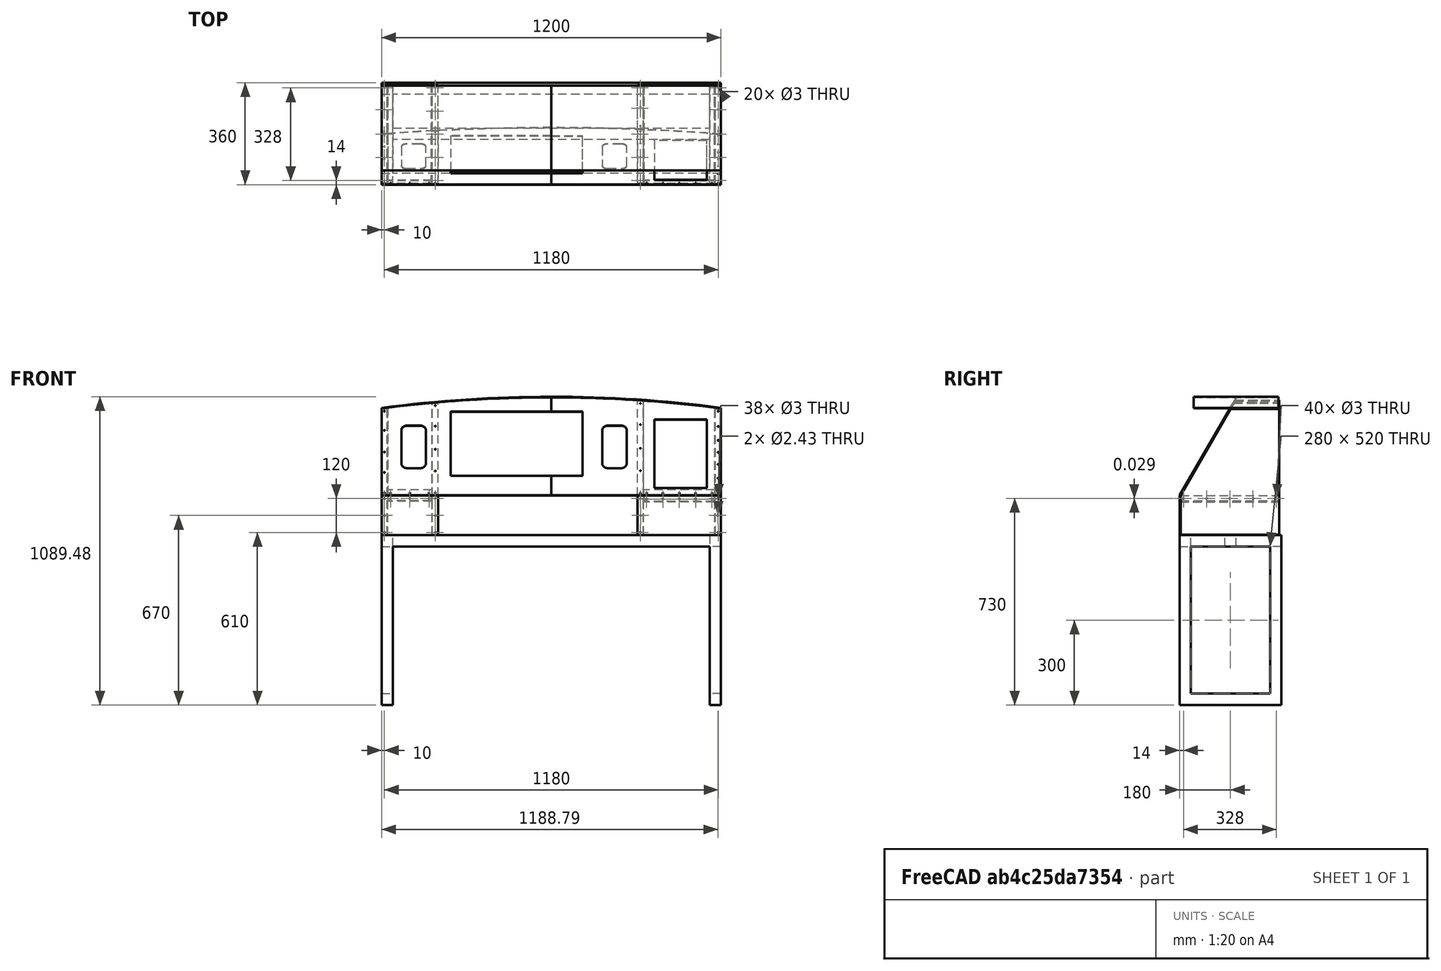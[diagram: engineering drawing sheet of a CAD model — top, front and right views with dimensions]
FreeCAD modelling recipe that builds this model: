
FCSTD DOCUMENT  (FreeCAD 1.0R39109 (Git))
Label: RecubrimientoSuperior
License: All rights reserved
LicenseURL: https://en.wikipedia.org/wiki/All_rights_reserved
objects: Sketcher::SketchObject×66, PartDesign::Pocket×43, PartDesign::Pad×23, PartDesign::SubShapeBinder×21, PartDesign::Body×13, PartDesign::Plane×3, App::DocumentObjectGroup×3, App::Part×3, Part::Part2DObjectPython×1
note: 368 computed .brp shape members not serialized (recipe doc carries the construction recipe); baked Part::Feature solids carry a one-line shape summary decoded from their .brp

FEATURE [Sketcher::SketchObject] Sketch
  ArcFitTolerance = 1e-06
  AttachmentSupport = -> [YZ_Plane001]
  FullyConstrained = true
  MakeInternals = false
  MapMode = 5
  Placement = pos=(0,0,0) rot=(0.57735,0.57735,0.57735;2.0944rad)
  sketch-geometry (4):
    g0: LineSegment StartX=2 StartY=0 StartZ=0 EndX=2 EndY=140 EndZ=0
    g1: LineSegment StartX=0 StartY=140 StartZ=0 EndX=0 EndY=0 EndZ=0
    g2: LineSegment StartX=0 StartY=0 StartZ=0 EndX=2 EndY=0 EndZ=0
    g3: LineSegment StartX=0 StartY=140 StartZ=0 EndX=2 EndY=140 EndZ=0
  constraints (11):
    c: Vertical(g0)
    c: Vertical(g1)
    c: Distance(g0,g1) = 2
    c: Distance(g1,g1) = 140
    c: Coincident(g1,g2)
    c: Coincident(g1,g-1)
    c: Coincident(g0,g2)
    c: PointOnObject(g0,g-1)
    c: Coincident(g3,g1)
    c: Coincident(g3,g0)
    c: Horizontal(g3)
FEATURE [PartDesign::Pad] Pad
  Direction = (1,0,0)
  Length = 200
  Length2 = 10
  Placement = pos=(0,0,0) rot=(1,1,1;2.0944rad)
  Profile = -> Sketch
  ReferenceAxis = -> Sketch [N_Axis]
  Refine = true
  Suppressed = false
  Type = 0
FEATURE [Sketcher::SketchObject] Sketch005
  ArcFitTolerance = 1e-06
  AttachmentSupport = -> [YZ_Plane002]
  FullyConstrained = true
  MakeInternals = false
  MapMode = 5
  Placement = pos=(0,0,0) rot=(0.57735,0.57735,0.57735;2.0944rad)
  sketch-geometry (4):
    g0: LineSegment StartX=0 StartY=0 StartZ=0 EndX=0 EndY=140 EndZ=0
    g1: LineSegment StartX=0 StartY=0 StartZ=0 EndX=2 EndY=0 EndZ=0
    g2: LineSegment StartX=2 StartY=0 StartZ=0 EndX=2 EndY=140 EndZ=0
    g3: LineSegment StartX=0 StartY=140 StartZ=0 EndX=2 EndY=140 EndZ=0
  constraints (11):
    c: Distance(g0) = 140
    c: Coincident(g0,g-1)
    c: PointOnObject(g0,g-2)
    c: Distance(g1) = 2
    c: Coincident(g1,g0)
    c: Vertical(g2)
    c: Coincident(g3,g0)
    c: Coincident(g3,g2)
    c: Horizontal(g3)
    c: Coincident(g2,g1)
    c: Horizontal(g1)
FEATURE [PartDesign::Pad] Pad002
  Direction = (1,0,0)
  Length = 295
  Length2 = 10
  Placement = pos=(0,0,0) rot=(1,1,1;2.0944rad)
  Profile = -> Sketch005
  ReferenceAxis = -> Sketch005 [N_Axis]
  Refine = true
  Suppressed = false
  Type = 0
FEATURE [Sketcher::SketchObject] Sketch009
  ArcFitTolerance = 1e-06
  AttachmentSupport = -> [XZ_Plane003]
  FullyConstrained = false
  MakeInternals = false
  MapMode = 5
  Placement = pos=(0,0,0) rot=(1,0,0;1.5708rad)
  sketch-geometry (31):
    g0: LineSegment StartX=-300 StartY=-200 StartZ=0 EndX=300 EndY=-200 EndZ=0
    g1: LineSegment StartX=300 StartY=-200 StartZ=0 EndX=300 EndY=-120 EndZ=0
    g2: LineSegment StartX=-300 StartY=154.794 StartZ=0 EndX=-300 EndY=-200 EndZ=0
    g3: GeomPoint [constr] X=0 Y=0 Z=0
    g4: LineSegment StartX=-230 StartY=65.1308 StartZ=0 EndX=-230 EndY=-68.8692 EndZ=0
    g5: LineSegment StartX=-210 StartY=-88.8692 StartZ=0 EndX=-163 EndY=-88.8692 EndZ=0
    g6: LineSegment StartX=-143 StartY=-68.8692 StartZ=0 EndX=-143 EndY=65.1308 EndZ=0
    g7: LineSegment StartX=-163 StartY=85.1308 StartZ=0 EndX=-210 EndY=85.1308 EndZ=0
    g8: ArcOfCircle CenterX=-210 CenterY=65.1308 CenterZ=0 NormalX=0 NormalY=0 NormalZ=1 AngleXU=0 Radius=20 StartAngle=1.5708 EndAngle=3.14159
    g9: ArcOfCircle CenterX=-210 CenterY=-68.8692 CenterZ=0 NormalX=0 NormalY=0 NormalZ=1 AngleXU=0 Radius=20 StartAngle=3.14159 EndAngle=4.71239
    g10: ArcOfCircle CenterX=-163 CenterY=-68.8692 CenterZ=0 NormalX=0 NormalY=0 NormalZ=1 AngleXU=0 Radius=20 StartAngle=4.71239 EndAngle=6.28319
    g11: ArcOfCircle CenterX=-163 CenterY=65.1308 CenterZ=0 NormalX=0 NormalY=0 NormalZ=1 AngleXU=0 Radius=20 StartAngle=0 EndAngle=1.5708
    g12: GeomPoint [constr] X=-230 Y=85.1308 Z=0
    g13: GeomPoint [constr] X=-143 Y=-88.8692 Z=0
    g14: LineSegment [constr] StartX=-300 StartY=-120 StartZ=0 EndX=-55 EndY=-120 EndZ=0
    g15: LineSegment [constr] StartX=-55 StartY=-200 StartZ=0 EndX=-55 EndY=-120 EndZ=0
    g16: LineSegment StartX=-55 StartY=-120 StartZ=0 EndX=300 EndY=-120 EndZ=0
    g17: LineSegment StartX=300 StartY=142 StartZ=0 EndX=-55 EndY=142 EndZ=0
    g18: LineSegment StartX=-55 StartY=142 StartZ=0 EndX=-55 EndY=-120 EndZ=0
    g19: LineSegment [constr] StartX=-300 StartY=150 StartZ=0 EndX=-300 EndY=105.005 EndZ=0
    g20: LineSegment [constr] StartX=-300.037 StartY=80 StartZ=0 EndX=-234.617 EndY=80 EndZ=0
    g21: LineSegment [constr] StartX=-234.617 StartY=80 StartZ=0 EndX=-234.617 EndY=175 EndZ=0
    g22: LineSegment [constr] StartX=-234.617 StartY=175 StartZ=0 EndX=-300 EndY=150 EndZ=0
    g23: LineSegment StartX=300 StartY=142 StartZ=0 EndX=300 EndY=200 EndZ=0
    g24: LineSegment [constr] StartX=122.5 StartY=-120 StartZ=0 EndX=122.5 EndY=-200 EndZ=0
    g25: LineSegment [constr] StartX=-300 StartY=154.794 StartZ=0 EndX=900 EndY=154.794 EndZ=0
    g26: ArcOfCircle CenterX=299.932 CenterY=-3803.45 CenterZ=0 NormalX=0 NormalY=0 NormalZ=1 AngleXU=0 Radius=4003.45 StartAngle=1.57078 EndAngle=1.72122
    g27: LineSegment [constr] StartX=-230 StartY=65.1308 StartZ=0 EndX=-143 EndY=65.1308 EndZ=0
    g28: LineSegment [constr] StartX=-230 StartY=-68.8692 StartZ=0 EndX=-143 EndY=-68.8692 EndZ=0
    g29: LineSegment [constr] StartX=-186.5 StartY=-68.8692 StartZ=0 EndX=-186.5 EndY=126.261 EndZ=0
    g30: LineSegment [constr] StartX=-300 StartY=15.0643 StartZ=0 EndX=-230 EndY=15.0643 EndZ=0
  constraints (78):
    c: Coincident(g0,g1)
    c: Coincident(g2,g0)
    c: Horizontal(g0)
    c: Vertical(g1)
    c: Vertical(g2)
    c: Symmetric(g23,g0,g3)
    c: Distance(g1,g2) = 600
    c: Distance(g0,g19) = 350
    c: Coincident(g3,g-1)
    c: Tangent(g4,g8) = -1.5708
    c: Tangent(g4,g9) = -1.5708
    c: Tangent(g5,g9) = -1.5708
    c: Tangent(g5,g10) = -1.5708
    c: Tangent(g6,g10) = -1.5708
    c: Tangent(g6,g11) = -1.5708
    c: Tangent(g7,g11) = -1.5708
    c: Tangent(g7,g8) = -1.5708
    c: Vertical(g4)
    c: Vertical(g6)
    c: Horizontal(g5)
    c: Horizontal(g7)
    c: Equal(g8,g9)
    c: Equal(g9,g10)
    c: Equal(g10,g11)
    c: PointOnObject(g12,g4)
    c: PointOnObject(g12,g7)
    c: PointOnObject(g13,g5)
    c: PointOnObject(g13,g6)
    c: Radius(g9) = 20
    c: Distance(g14) = 245
    c: PointOnObject(g14,g2)
    c: Horizontal(g14)
    c: Distance(g15) = 80
    c: PointOnObject(g15,g0)
    c: Vertical(g15)
    c: Coincident(g14,g15)
    c: Coincident(g17,g18)
    c: Coincident(g18,g16)
    c: Horizontal(g16)
    c: Horizontal(g17)
    c: Vertical(g18)
    c: Distance(g16,g17) = 262
    c: Coincident(g16,g14)
    c: Coincident(g20,g21)
    c: Coincident(g21,g22)
    c: Coincident(g22,g19)
    c: Vertical(g19)
    c: Vertical(g21)
    c: Horizontal(g20)
    c: Distance(g19,g21) = 70
    c: Distance(g20,g22) = 70
    c: PointOnObject(g17,g23)
    c: Coincident(g1,g16)
    c: PointOnObject(g23,g17)
    c: Symmetric(g16,g16,g24)
    c: PointOnObject(g24,g0)
    c: Vertical(g24)
    c: Vertical(g23)
    c: Distance(g25) = 1200
    c: PointOnObject(g25,g19)
    c: Horizontal(g25)
    c: Coincident(g26,g25)
    c: Coincident(g2,g25)
    c: Coincident(g23,g26)
    c: DistanceY(g0,g23) = 400
    c: Coincident(g27,g4)
    c: Coincident(g27,g6)
    c: Coincident(g28,g4)
    c: Coincident(g28,g6)
    c: Symmetric(g28,g28,g29)
    c: Vertical(g29)
    c: Distance(g30) = 70
    c: PointOnObject(g30,g2)
    c: Horizontal(g30)
    c: DistanceY(g5,g7) = 174
    c: DistanceX(g4,g6) = 87
    c: DistanceX(g17,g17) = 355
    c: PointOnObject(g30,g4)
FEATURE [PartDesign::SubShapeBinder] Binder
  BindCopyOnChange = 0
  BindMode = 2
  ClaimChildren = false
  Context = -> Part [Body003.Binder.]
  Fuse = false
  MakeFace = true
  OffsetFill = false
  OffsetIntersection = false
  OffsetJoinType = 0
  OffsetOpenResult = false
  PartialLoad = false
  Refine = true
  Relative = true
  _Version = 2
FEATURE [PartDesign::Pad] Pad003
  Direction = (0,-1,2e-16)
  Length = 2
  Length2 = 10
  Placement = pos=(0,0,0) rot=(1,0,0;1.5708rad)
  Profile = -> Sketch009
  ReferenceAxis = -> Sketch009 [N_Axis]
  Refine = true
  Reversed = true
  Suppressed = false
  Type = 0
FEATURE [Sketcher::SketchObject] Sketch012
  ArcFitTolerance = 1e-06
  AttachmentSupport = -> [Binder]
  ExternalGeometry = -> [Binder]
  FullyConstrained = true
  MakeInternals = false
  MapMode = 5
  Placement = pos=(0,86.1695,-49.75) rot=(1,0,0;1.0472rad)
  sketch-geometry (24):
    g0: LineSegment StartX=300 StartY=-176 StartZ=0 EndX=900 EndY=-176 EndZ=0
    g1: LineSegment StartX=900 StartY=-176 StartZ=0 EndX=900 EndY=178.794 EndZ=0
    g2: LineSegment StartX=300 StartY=-96 StartZ=0 EndX=410 EndY=-96 EndZ=0
    g3: LineSegment StartX=410 StartY=-96 StartZ=0 EndX=410 EndY=166 EndZ=0
    g4: LineSegment StartX=300 StartY=166 StartZ=0 EndX=410 EndY=166 EndZ=0
    g5: LineSegment [constr] StartX=-300 StartY=178.794 StartZ=0 EndX=900 EndY=178.794 EndZ=0
    g6: ArcOfCircle CenterX=299.932 CenterY=-3779.45 CenterZ=0 NormalX=0 NormalY=0 NormalZ=1 AngleXU=0 Radius=4003.47 StartAngle=1.42034 EndAngle=1.57078
    g7: LineSegment StartX=300 StartY=-96 StartZ=0 EndX=300 EndY=-176 EndZ=0
    g8: LineSegment StartX=500 StartY=-64.8692 StartZ=0 EndX=547 EndY=-64.8692 EndZ=0
    g9: LineSegment StartX=567 StartY=-44.8692 StartZ=0 EndX=567 EndY=89.1308 EndZ=0
    g10: LineSegment StartX=547 StartY=109.131 StartZ=0 EndX=500 EndY=109.131 EndZ=0
    g11: LineSegment StartX=480 StartY=89.1308 StartZ=0 EndX=480 EndY=-44.8692 EndZ=0
    g12: ArcOfCircle CenterX=500 CenterY=-44.8692 CenterZ=0 NormalX=0 NormalY=0 NormalZ=1 AngleXU=0 Radius=20 StartAngle=3.14159 EndAngle=4.71239
    g13: ArcOfCircle CenterX=547 CenterY=-44.8692 CenterZ=0 NormalX=0 NormalY=0 NormalZ=1 AngleXU=0 Radius=20 StartAngle=4.71239 EndAngle=6.28319
    g14: ArcOfCircle CenterX=547 CenterY=89.1308 CenterZ=0 NormalX=0 NormalY=0 NormalZ=1 AngleXU=0 Radius=20 StartAngle=0 EndAngle=1.5708
    g15: ArcOfCircle CenterX=500 CenterY=89.1308 CenterZ=0 NormalX=0 NormalY=0 NormalZ=1 AngleXU=0 Radius=20 StartAngle=1.5708 EndAngle=3.14159
    g16: GeomPoint [constr] X=480 Y=-64.8692 Z=0
    g17: GeomPoint [constr] X=567 Y=109.131 Z=0
    g18: LineSegment [constr] StartX=-143 StartY=-44.8692 StartZ=0 EndX=480 EndY=-44.8692 EndZ=0
    g19: LineSegment StartX=665 StartY=-146 StartZ=0 EndX=850 EndY=-146 EndZ=0
    g20: LineSegment StartX=850 StartY=-146 StartZ=0 EndX=850 EndY=134 EndZ=0
    g21: LineSegment StartX=850 StartY=134 StartZ=0 EndX=665 EndY=134 EndZ=0
    g22: LineSegment StartX=665 StartY=134 StartZ=0 EndX=665 EndY=-146 EndZ=0
    g23: LineSegment StartX=300 StartY=224.02 StartZ=0 EndX=300 EndY=166 EndZ=0
  constraints (61):
    c: Coincident(g0,g-3)
    c: Horizontal(g0)
    c: Coincident(g1,g0)
    c: Vertical(g1)
    c: Coincident(g2,g-7)
    c: Horizontal(g2)
    c: Coincident(g3,g2)
    c: Vertical(g3)
    c: Coincident(g4,g-5)
    c: Horizontal(g4)
    c: Coincident(g3,g4)
    c: DistanceX(g0,g0) = 600
    c: Coincident(g5,g-6)
    c: Coincident(g5,g1)
    c: Horizontal(g5)
    c: Coincident(g6,g-6)
    c: Coincident(g6,g1)
    c: Coincident(g7,g2)
    c: Coincident(g7,g0)
    c: DistanceX(g4,g4) = 110
    c: Tangent(g8,g12) = -1.5708
    c: Tangent(g8,g13) = -1.5708
    c: Tangent(g9,g13) = -1.5708
    c: Tangent(g9,g14) = -1.5708
    c: Tangent(g10,g14) = -1.5708
    c: Tangent(g10,g15) = -1.5708
    c: Tangent(g11,g15) = -1.5708
    c: Tangent(g11,g12) = -1.5708
    c: Horizontal(g8)
    c: Horizontal(g10)
    c: Vertical(g9)
    c: Vertical(g11)
    c: Equal(g12,g13)
    c: Equal(g13,g14)
    c: Equal(g14,g15)
    c: PointOnObject(g16,g8)
    c: PointOnObject(g16,g11)
    c: PointOnObject(g17,g9)
    c: PointOnObject(g17,g10)
    c: Equal(g15,g-8)
    c: Equal(g-10,g10)
    c: Equal(g-9,g11)
    c: Coincident(g18,g-9)
    c: Coincident(g18,g11)
    c: Horizontal(g18)
    c: DistanceX(g3,g11) = 70
    c: Coincident(g19,g20)
    c: Coincident(g20,g21)
    c: Coincident(g21,g22)
    c: Coincident(g22,g19)
    c: Horizontal(g19)
    c: Horizontal(g21)
    c: Vertical(g20)
    c: Vertical(g22)
    c: DistanceY(g22,g22) = 280
    c: DistanceX(g21,g21) = 185
    c: DistanceY(g0,g19) = 30
    c: DistanceX(g20,g1) = 50
    c: Coincident(g23,g6)
    c: Coincident(g23,g4)
    c: Vertical(g23)
FEATURE [PartDesign::Pad] Pad004
  Direction = (0,-0.866025,0.5)
  Length = 2
  Length2 = 10
  Profile = -> Sketch012
  ReferenceAxis = -> Sketch012 [N_Axis]
  Refine = true
  Reversed = true
  Suppressed = false
  Type = 0
FEATURE [PartDesign::SubShapeBinder] Binder002
  BindCopyOnChange = 0
  BindMode = 2
  ClaimChildren = false
  Context = -> Part [Body005.Binder002.]
  Fuse = false
  MakeFace = true
  OffsetFill = false
  OffsetIntersection = false
  OffsetJoinType = 0
  OffsetOpenResult = false
  PartialLoad = false
  Refine = true
  Relative = true
  _Version = 2
FEATURE [PartDesign::Plane] DatumPlane001
  AttachmentSupport = -> [XZ_Plane006,Binder002]
  Length = 664.107
  MapMode = 53
  Placement = pos=(0,-71.8202,-1.59e-14) rot=(1,0,0;1.5708rad)
  ResizeMode = 0
  Width = 235.347
FEATURE [Sketcher::SketchObject] Sketch014
  ArcFitTolerance = 1e-06
  AttachmentSupport = -> [DatumPlane001]
  ExternalGeometry = -> [Binder002]
  FullyConstrained = false
  MakeInternals = false
  MapMode = 5
  Placement = pos=(0,-71.8202,-1.59e-14) rot=(1,0,0;1.5708rad)
  sketch-geometry (4):
    g0: ArcOfCircle CenterX=299.094 CenterY=-4459.19 CenterZ=0 NormalX=0 NormalY=0 NormalZ=1 AngleXU=0 Radius=4603.43 StartAngle=1.5706 EndAngle=1.70131
    g1: LineSegment StartX=300 StartY=144.24 StartZ=0 EndX=300 EndY=146.24 EndZ=0
    g2: LineSegment StartX=-300 StartY=105.09 StartZ=0 EndX=-300 EndY=107.09 EndZ=0
    g3: ArcOfCircle CenterX=299.093 CenterY=-4457.17 CenterZ=0 NormalX=0 NormalY=0 NormalZ=1 AngleXU=0 Radius=4603.41 StartAngle=1.5706 EndAngle=1.70131
  constraints (10):
    c: Coincident(g0,g-5)
    c: Coincident(g0,g-4)
    c: Distance(g1) = 2
    c: Coincident(g1,g0)
    c: Vertical(g1)
    c: Distance(g2) = 2
    c: Coincident(g3,g2)
    c: Vertical(g2)
    c: Coincident(g3,g1)
    c: Coincident(g2,g0)
FEATURE [PartDesign::Pad] Pad005
  Direction = (0,-1,2e-16)
  Length = 300
  Length2 = 10
  Midplane = true
  Placement = pos=(0,-71.8202,-1.59e-14) rot=(1,0,0;1.5708rad)
  Profile = -> Sketch014
  ReferenceAxis = -> Sketch014 [N_Axis]
  Refine = true
  Suppressed = false
  Type = 0
FEATURE [PartDesign::Plane] DatumPlane002  label="Plano de refencia "
  AttachmentSupport = -> [Pad005]
  Length = 216.57
  MapMode = 5
  Placement = pos=(300,-71.8202,-1.59e-14) rot=(0.707107,0,0.707107;3.14159rad)
  ResizeMode = 0
  Width = 345.331
FEATURE [PartDesign::Body] Body005  label="LaminaSprPt1"
  AllowCompound = false
  Group = -> [Binder002,DatumPlane001,Sketch014,Pad005,DatumPlane002]
  Origin = -> Origin006
  Placement = pos=(0,270,0) rot=(0,0,1;0rad)
  Tip = -> Pad005
FEATURE [PartDesign::Plane] CopyDatumPlane001
  Length = 1867.38
  Placement = pos=(0,198.18,0) rot=(1,0,0;1.5708rad)
  ResizeMode = 0
  Width = 292.292
FEATURE [PartDesign::SubShapeBinder] Binder003
  BindCopyOnChange = 0
  BindMode = 2
  ClaimChildren = false
  Context = -> Part [Body006.Binder003.]
  Fuse = false
  MakeFace = true
  OffsetFill = false
  OffsetIntersection = false
  OffsetJoinType = 0
  OffsetOpenResult = false
  PartialLoad = false
  Refine = true
  Relative = true
  _Version = 2
FEATURE [Sketcher::SketchObject] Sketch015
  ArcFitTolerance = 1e-06
  AttachmentSupport = -> [CopyDatumPlane001]
  ExternalGeometry = -> [Binder003]
  FullyConstrained = false
  MakeInternals = false
  MapMode = 5
  Placement = pos=(0,198.18,0) rot=(1,0,0;1.5708rad)
  sketch-geometry (4):
    g0: ArcOfCircle CenterX=-1712.36 CenterY=-4462.69 CenterZ=0 NormalX=0 NormalY=0 NormalZ=1 AngleXU=0 Radius=4346.96 StartAngle=1.43642 EndAngle=1.57485
    g1: LineSegment StartX=-1130 StartY=-154.91 StartZ=0 EndX=-1130 EndY=-152.91 EndZ=0
    g2: ArcOfCircle CenterX=-1712.37 CenterY=-4460.9 CenterZ=0 NormalX=0 NormalY=0 NormalZ=1 AngleXU=0 Radius=4347.18 StartAngle=1.43643 EndAngle=1.57485
    g3: LineSegment StartX=-1730 StartY=-113.76 StartZ=0 EndX=-1730 EndY=-115.76 EndZ=0
  constraints (10):
    c: Coincident(g0,g-5)
    c: Coincident(g0,g-4)
    c: Distance(g1) = 2
    c: Coincident(g1,g0)
    c: Vertical(g1)
    c: Coincident(g3,g2)
    c: Coincident(g3,g0)
    c: Vertical(g3)
    c: Coincident(g2,g1)
    c: DistanceY(g3,g3) = 2
FEATURE [PartDesign::Pad] Pad006
  Direction = (0,-1,2e-16)
  Length = 300
  Length2 = 10
  Midplane = true
  Placement = pos=(0,198.18,0) rot=(1,0,0;1.5708rad)
  Profile = -> Sketch015
  ReferenceAxis = -> Sketch015 [N_Axis]
  Refine = true
  Suppressed = false
  Type = 0
FEATURE [PartDesign::Body] Body006  label="LaminaSprPt2"
  AllowCompound = false
  Group = -> [CopyDatumPlane001,Sketch015,Binder003,Pad006]
  Origin = -> Origin007
  Placement = pos=(2030,0,260) rot=(0,0,1;0rad)
  Tip = -> Pad006
FEATURE [Sketcher::SketchObject] Sketch019
  ArcFitTolerance = 1e-06
  AttachmentSupport = -> [Pad002]
  ExternalGeometry = -> [Pad002]
  FullyConstrained = false
  MakeInternals = false
  MapMode = 5
  Placement = pos=(0,0,0) rot=(0.57735,0.57735,-0.57735;2.0944rad)
  sketch-geometry (26):
    g0: LineSegment [constr] StartX=-3.28e-14 StartY=295 StartZ=0 EndX=-10 EndY=295 EndZ=0
    g1: LineSegment [constr] StartX=-10 StartY=295 StartZ=0 EndX=-10 EndY=285 EndZ=0
    g2: LineSegment [constr] StartX=-10 StartY=285 StartZ=0 EndX=-3.2e-14 EndY=285 EndZ=0
    g3: LineSegment [constr] StartX=-3.28e-14 StartY=285 StartZ=0 EndX=-3.28e-14 EndY=295 EndZ=0
    g4: LineSegment [constr] StartX=-140 StartY=295 StartZ=0 EndX=-140 EndY=285 EndZ=0
    g5: LineSegment [constr] StartX=-140 StartY=285 StartZ=0 EndX=-130 EndY=285 EndZ=0
    g6: LineSegment [constr] StartX=-130 StartY=285 StartZ=0 EndX=-130 EndY=295 EndZ=0
    g7: LineSegment [constr] StartX=-130 StartY=295 StartZ=0 EndX=-140 EndY=295 EndZ=0
    g8: LineSegment [constr] StartX=-70 StartY=295 StartZ=0 EndX=-70 EndY=0 EndZ=0
    g9: LineSegment [constr] StartX=0 StartY=147.5 StartZ=0 EndX=-140 EndY=147.5 EndZ=0
    g10: Circle CenterX=-130 CenterY=285 CenterZ=0 NormalX=0 NormalY=0 NormalZ=1 AngleXU=0 Radius=1.5
    g11: Circle CenterX=-10 CenterY=285 CenterZ=0 NormalX=0 NormalY=0 NormalZ=1 AngleXU=0 Radius=1.5
    g12: LineSegment [constr] StartX=-10 StartY=285 StartZ=0 EndX=-130 EndY=285 EndZ=0
    g13: Circle CenterX=-70 CenterY=283.786 CenterZ=0 NormalX=0 NormalY=0 NormalZ=1 AngleXU=0 Radius=1.21447
    g14: LineSegment [constr] StartX=0 StartY=0 StartZ=0 EndX=0 EndY=10 EndZ=0
    g15: LineSegment [constr] StartX=0 StartY=10 StartZ=0 EndX=-10 EndY=10 EndZ=0
    g16: LineSegment [constr] StartX=-10 StartY=10 StartZ=0 EndX=-10 EndY=0 EndZ=0
    g17: LineSegment [constr] StartX=-10 StartY=0 StartZ=0 EndX=0 EndY=0 EndZ=0
    g18: LineSegment [constr] StartX=-140 StartY=0 StartZ=0 EndX=-130 EndY=0 EndZ=0
    g19: LineSegment [constr] StartX=-130 StartY=0 StartZ=0 EndX=-130 EndY=10 EndZ=0
    g20: LineSegment [constr] StartX=-130 StartY=10 StartZ=0 EndX=-140 EndY=10 EndZ=0
    g21: LineSegment [constr] StartX=-140 StartY=10 StartZ=0 EndX=-140 EndY=0 EndZ=0
    g22: LineSegment [constr] StartX=-130 StartY=9.85879 StartZ=0 EndX=-10 EndY=9.85879 EndZ=0
    g23: Circle CenterX=-10 CenterY=10 CenterZ=0 NormalX=0 NormalY=0 NormalZ=1 AngleXU=0 Radius=1.5
    g24: Circle CenterX=-70 CenterY=11.3588 CenterZ=0 NormalX=0 NormalY=0 NormalZ=1 AngleXU=0 Radius=1.5
    g25: Circle CenterX=-130 CenterY=10 CenterZ=0 NormalX=0 NormalY=0 NormalZ=1 AngleXU=0 Radius=1.5
  constraints (56):
    c: Coincident(g0,g1)
    c: Coincident(g1,g2)
    c: Coincident(g2,g3)
    c: Coincident(g3,g0)
    c: Horizontal(g0)
    c: Horizontal(g2)
    c: Vertical(g1)
    c: Vertical(g3)
    c: Distance(g1,g3) = 10
    c: Distance(g0,g2) = 10
    c: Coincident(g0,g-3)
    c: Coincident(g4,g5)
    c: Coincident(g5,g6)
    c: Coincident(g6,g7)
    c: Coincident(g7,g4)
    c: Vertical(g4)
    c: Vertical(g6)
    c: Horizontal(g5)
    c: Horizontal(g7)
    c: Distance(g4,g6) = 10
    c: Distance(g5,g7) = 10
    c: Coincident(g4,g-4)
    c: PointOnObject(g8,g-1)
    c: Vertical(g8)
    c: Symmetric(g-6,g-6,g9)
    c: Symmetric(g-7,g-7,g9)
    c: Coincident(g11,g1)
    c: Coincident(g12,g1)
    c: Coincident(g12,g10)
    c: Horizontal(g12)
    c: Tangent(g13,g12)
    c: Coincident(g14,g15)
    c: Coincident(g15,g16)
    c: Coincident(g16,g17)
    c: Coincident(g17,g14)
    c: Vertical(g14)
    c: Vertical(g16)
    c: Horizontal(g15)
    c: Horizontal(g17)
    c: Distance(g14,g16) = 10
    c: Distance(g15,g17) = 10
    c: Coincident(g14,g-1)
    c: Coincident(g18,g19)
    c: Coincident(g19,g20)
    c: Coincident(g20,g21)
    c: Coincident(g21,g18)
    c: Horizontal(g18)
    c: Horizontal(g20)
    c: Vertical(g19)
    c: Vertical(g21)
    c: Distance(g19,g21) = 10
    c: Distance(g18,g20) = 10
    c: Coincident(g18,g-7)
    c: Diameter(g24) = 3
    c: PointOnObject(g24,g8)
    c: Tangent(g24,g22)
FEATURE [PartDesign::Pocket] Pocket008
  BaseFeature = -> Pad002
  Direction = (0,1,0)
  Length = 5
  Length2 = 5
  Placement = pos=(0,0,0) rot=(1,1,1;2.0944rad)
  Profile = -> Sketch019
  ReferenceAxis = -> Sketch019 [N_Axis]
  Refine = true
  Suppressed = false
  Type = 0
FEATURE [PartDesign::SubShapeBinder] Binder004
  BindCopyOnChange = 0
  BindMode = 2
  ClaimChildren = false
  Context = -> Part [Body004.Binder004.]
  Fuse = false
  MakeFace = true
  OffsetFill = false
  OffsetIntersection = false
  OffsetJoinType = 0
  OffsetOpenResult = false
  PartialLoad = false
  Refine = true
  Relative = true
  _Version = 2
FEATURE [Sketcher::SketchObject] Sketch020
  ArcFitTolerance = 1e-06
  AttachmentSupport = -> [Binder004]
  ExternalGeometry = -> [Binder004]
  FullyConstrained = false
  MakeInternals = false
  MapMode = 5
  Placement = pos=(-9e-16,-4.1,0) rot=(0,0.707107,0.707107;3.14159rad)
  sketch-geometry (10):
    g0: LineSegment [constr] StartX=-1180 StartY=-343.2 StartZ=0 EndX=-1160 EndY=-343.2 EndZ=0
    g1: LineSegment StartX=-1160 StartY=-341.2 StartZ=0 EndX=-1160 EndY=106.007 EndZ=0
    g2: LineSegment StartX=-1160 StartY=-343.2 StartZ=0 EndX=-1158 EndY=-343.2 EndZ=0
    g3: LineSegment StartX=-1158 StartY=-343.2 StartZ=0 EndX=-1158 EndY=108.007 EndZ=0
    g4: LineSegment StartX=-1158 StartY=108.007 StartZ=0 EndX=-1180 EndY=105.09 EndZ=0
    g5: LineSegment StartX=-1180 StartY=105.09 StartZ=0 EndX=-1180 EndY=103.09 EndZ=0
    g6: LineSegment StartX=-1180 StartY=103.09 StartZ=0 EndX=-1160 EndY=106.007 EndZ=0
    g7: LineSegment StartX=-1160 StartY=-343.2 StartZ=0 EndX=-1180 EndY=-343.2 EndZ=0
    g8: LineSegment StartX=-1180 StartY=-343.2 StartZ=0 EndX=-1180 EndY=-341.2 EndZ=0
    g9: LineSegment StartX=-1180 StartY=-341.2 StartZ=0 EndX=-1160 EndY=-341.2 EndZ=0
  constraints (26):
    c: Distance(g0) = 20
    c: Coincident(g0,g-3)
    c: Horizontal(g0)
    c: Vertical(g1)
    c: Distance(g2) = 2
    c: Coincident(g2,g0)
    c: Horizontal(g2)
    c: Coincident(g3,g2)
    c: PointOnObject(g3,g-5)
    c: Vertical(g3)
    c: Coincident(g4,g3)
    c: Coincident(g4,g-5)
    c: Distance(g5) = 2
    c: Coincident(g5,g4)
    c: Vertical(g5)
    c: Coincident(g6,g5)
    c: Coincident(g1,g6)
    c: DistanceY(g1,g3) = 2
    c: Coincident(g7,g0)
    c: Coincident(g7,g0)
    c: Distance(g8) = 2
    c: Coincident(g8,g0)
    c: Vertical(g8)
    c: Coincident(g9,g8)
    c: Horizontal(g9)
    c: Coincident(g1,g9)
FEATURE [PartDesign::Pad] Pad007
  Direction = (0,1,-2e-16)
  Length = 350
  Length2 = 10
  Profile = -> Sketch020
  ReferenceAxis = -> Sketch020 [N_Axis]
  Refine = true
  Suppressed = false
  Type = 0
FEATURE [Sketcher::SketchObject] Sketch021
  ArcFitTolerance = 1e-06
  AttachmentSupport = -> [Pad007]
  ExternalGeometry = -> [Binder004,Pad007]
  FullyConstrained = false
  MakeInternals = false
  MapMode = 5
  Placement = pos=(1160,0,0) rot=(0.57735,0.57735,0.57735;2.0944rad)
  sketch-geometry (3):
    g0: LineSegment StartX=-4.1 StartY=-203.2 StartZ=0 EndX=175.575 EndY=108.007 EndZ=0
    g1: LineSegment StartX=-4.1 StartY=108.007 StartZ=0 EndX=-4.1 EndY=-203.2 EndZ=0
    g2: LineSegment StartX=-4.1 StartY=108.007 StartZ=0 EndX=175.575 EndY=108.007 EndZ=0
  constraints (6):
    c: Angle(g-1,g0) = 1.0472
    c: Coincident(g0,g-4)
    c: Coincident(g1,g-5)
    c: Coincident(g1,g0)
    c: Coincident(g2,g1)
    c: Coincident(g0,g2)
FEATURE [PartDesign::Pocket] Pocket009
  BaseFeature = -> Pad007
  Direction = (-1,0,0)
  Length = 5
  Length2 = 5
  Midplane = true
  Profile = -> Sketch021
  ReferenceAxis = -> Sketch021 [N_Axis]
  Refine = true
  Suppressed = false
  Type = 1
FEATURE [Sketcher::SketchObject] Sketch022
  ArcFitTolerance = 1e-06
  AttachmentSupport = -> [Pocket009]
  ExternalGeometry = -> [Pocket009]
  FullyConstrained = true
  MakeInternals = false
  MapMode = 5
  Placement = pos=(1160,0,0) rot=(0.57735,0.57735,0.57735;2.0944rad)
  sketch-geometry (7):
    g0: LineSegment StartX=-4.1 StartY=-341.2 StartZ=0 EndX=-2.1 EndY=-341.2 EndZ=0
    g1: LineSegment StartX=-4.1 StartY=-341.2 StartZ=0 EndX=-4.1 EndY=-203.2 EndZ=0
    g2: LineSegment StartX=-4.1 StartY=-203.2 StartZ=0 EndX=172.736 EndY=103.09 EndZ=0
    g3: LineSegment StartX=-2.1 StartY=-341.2 StartZ=0 EndX=-2.1 EndY=-203.2 EndZ=0
    g4: LineSegment [constr] StartX=-4.1 StartY=-203.2 StartZ=0 EndX=-2.1 EndY=-203.2 EndZ=0
    g5: LineSegment StartX=-2.1 StartY=-203.2 StartZ=0 EndX=174.736 EndY=103.09 EndZ=0
    g6: LineSegment StartX=172.736 StartY=103.09 StartZ=0 EndX=174.736 EndY=103.09 EndZ=0
  constraints (17):
    c: Distance(g0) = 2
    c: Coincident(g0,g-5)
    c: Horizontal(g0)
    c: Coincident(g1,g0)
    c: Coincident(g1,g-5)
    c: Coincident(g2,g1)
    c: Coincident(g2,g-3)
    c: Coincident(g3,g0)
    c: Vertical(g3)
    c: Coincident(g4,g1)
    c: Coincident(g4,g3)
    c: Horizontal(g4)
    c: PointOnObject(g5,g-3)
    c: Coincident(g6,g2)
    c: Coincident(g6,g5)
    c: DistanceX(g6,g6) = 2
    c: Coincident(g5,g3)
FEATURE [PartDesign::Pad] Pad008
  BaseFeature = -> Pocket009
  Direction = (1,0,0)
  Length = 20
  Length2 = 10
  Profile = -> Sketch022
  ReferenceAxis = -> Sketch022 [N_Axis]
  Refine = true
  Suppressed = false
  Type = 0
FEATURE [Sketcher::SketchObject] Sketch023
  ArcFitTolerance = 1e-06
  AttachmentSupport = -> [Binder004]
  ExternalGeometry = -> [Binder004]
  FullyConstrained = true
  MakeInternals = false
  MapMode = 5
  Placement = pos=(-9e-16,-4.1,0) rot=(0,0.707107,0.707107;3.14159rad)
  sketch-geometry (3):
    g0: Circle CenterX=-1170 CenterY=-333.2 CenterZ=0 NormalX=0 NormalY=0 NormalZ=1 AngleXU=0 Radius=1.5
    g1: Circle CenterX=-1168.79 CenterY=-273.2 CenterZ=0 NormalX=0 NormalY=0 NormalZ=1 AngleXU=0 Radius=1.21447
    g2: Circle CenterX=-1170 CenterY=-213.2 CenterZ=0 NormalX=0 NormalY=0 NormalZ=1 AngleXU=0 Radius=1.5
  constraints (6):
    c: Coincident(g0,g-5)
    c: Equal(g0,g-5)
    c: Coincident(g1,g-4)
    c: Equal(g1,g-4)
    c: Coincident(g2,g-3)
    c: Equal(g2,g-3)
FEATURE [PartDesign::Pocket] Pocket010
  BaseFeature = -> Pad008
  Direction = (0,-1,2e-16)
  Length = 3
  Length2 = 5
  Profile = -> Sketch023
  ReferenceAxis = -> Sketch023 [N_Axis]
  Refine = true
  Reversed = true
  Suppressed = false
  Type = 0
FEATURE [Sketcher::SketchObject] Sketch024
  ArcFitTolerance = 1e-06
  AttachmentSupport = -> [Pocket010]
  ExternalGeometry = -> [Pocket010]
  FullyConstrained = false
  MakeInternals = false
  MapMode = 5
  Placement = pos=(-3.912e-13,84.9131,-49.0246) rot=(1,0,0;1.0472rad)
  sketch-geometry (45):
    g0: LineSegment [constr] StartX=1170 StartY=-186.687 StartZ=0 EndX=1180 EndY=-186.687 EndZ=0
    g1: LineSegment [constr] StartX=1170 StartY=-186.687 StartZ=0 EndX=1160 EndY=-186.687 EndZ=0
    g2: LineSegment [constr] StartX=1160 StartY=-186.687 StartZ=0 EndX=1160 EndY=175.647 EndZ=0
    g3: LineSegment [constr] StartX=1170 StartY=-186.687 StartZ=0 EndX=1170 EndY=-178.026 EndZ=0
    g4: LineSegment [constr] StartX=1170 StartY=-178.026 StartZ=0 EndX=1170 EndY=173.112 EndZ=0
    g5: LineSegment [constr] StartX=1170 StartY=173.112 StartZ=0 EndX=1170 EndY=153.112 EndZ=0
    g6: LineSegment [constr] StartX=1170 StartY=-178.06 StartZ=0 EndX=1180 EndY=-178.06 EndZ=0
    g7: LineSegment [constr] StartX=1180 StartY=-178.06 StartZ=0 EndX=1180 EndY=-168.06 EndZ=0
    g8: LineSegment [constr] StartX=1180 StartY=-168.06 StartZ=0 EndX=1170 EndY=-168.06 EndZ=0
    g9: LineSegment [constr] StartX=1170 StartY=-168.06 StartZ=0 EndX=1170 EndY=-178.06 EndZ=0
    g10: Circle CenterX=1170 CenterY=-168.06 CenterZ=0 NormalX=0 NormalY=0 NormalZ=1 AngleXU=0 Radius=1.5
    g11: LineSegment [constr] StartX=1170 StartY=-2.45712 StartZ=0 EndX=1180 EndY=-2.45712 EndZ=0
    g12: LineSegment [constr] StartX=1180 StartY=-2.45712 StartZ=0 EndX=1180 EndY=7.54288 EndZ=0
    g13: LineSegment [constr] StartX=1180 StartY=7.54288 StartZ=0 EndX=1170 EndY=7.54288 EndZ=0
    g14: LineSegment [constr] StartX=1170 StartY=7.54288 StartZ=0 EndX=1170 EndY=-2.45712 EndZ=0
    g15: Circle CenterX=1170 CenterY=-2.45712 CenterZ=0 NormalX=0 NormalY=0 NormalZ=1 AngleXU=0 Radius=1.5
    g16: LineSegment [constr] StartX=1170 StartY=173.112 StartZ=0 EndX=1170 EndY=163.112 EndZ=0
    g17: LineSegment [constr] StartX=1170 StartY=163.112 StartZ=0 EndX=1180 EndY=163.112 EndZ=0
    g18: LineSegment [constr] StartX=1180 StartY=163.112 StartZ=0 EndX=1180 EndY=173.112 EndZ=0
    g19: LineSegment [constr] StartX=1180 StartY=173.112 StartZ=0 EndX=1170 EndY=173.112 EndZ=0
    g20: Circle CenterX=1170 CenterY=165.291 CenterZ=0 NormalX=0 NormalY=0 NormalZ=1 AngleXU=0 Radius=1.5
    g21: LineSegment [constr] StartX=1297.09 StartY=68.0791 StartZ=0 EndX=1297.09 EndY=-37.9114 EndZ=0
    g22: LineSegment [constr] StartX=1297.09 StartY=15.0839 StartZ=0 EndX=1329.21 EndY=15.0839 EndZ=0
    g23: LineSegment [constr] StartX=1297.09 StartY=41.8939 StartZ=0 EndX=1329.2 EndY=41.8939 EndZ=0
    g24: LineSegment [constr] StartX=1297.09 StartY=-11.7261 StartZ=0 EndX=1329.2 EndY=-11.7261 EndZ=0
    g25: LineSegment [constr] StartX=1170 StartY=113.145 StartZ=0 EndX=1170 EndY=103.145 EndZ=0
    g26: LineSegment [constr] StartX=1170 StartY=103.145 StartZ=0 EndX=1180 EndY=103.145 EndZ=0
    g27: LineSegment [constr] StartX=1180 StartY=103.145 StartZ=0 EndX=1180 EndY=113.145 EndZ=0
    g28: LineSegment [constr] StartX=1180 StartY=113.145 StartZ=0 EndX=1170 EndY=113.145 EndZ=0
    g29: LineSegment [constr] StartX=1170 StartY=-51.3242 StartZ=0 EndX=1170 EndY=-61.3242 EndZ=0
    g30: LineSegment [constr] StartX=1170 StartY=-61.3242 StartZ=0 EndX=1180 EndY=-61.3242 EndZ=0
    g31: LineSegment [constr] StartX=1180 StartY=-61.3242 StartZ=0 EndX=1180 EndY=-51.3242 EndZ=0
    g32: LineSegment [constr] StartX=1180 StartY=-51.3242 StartZ=0 EndX=1170 EndY=-51.3242 EndZ=0
    g33: LineSegment [constr] StartX=1170 StartY=-118.06 StartZ=0 EndX=1180 EndY=-118.06 EndZ=0
    g34: LineSegment [constr] StartX=1180 StartY=-118.06 StartZ=0 EndX=1180 EndY=-108.06 EndZ=0
    g35: LineSegment [constr] StartX=1180 StartY=-108.06 StartZ=0 EndX=1170 EndY=-108.06 EndZ=0
    g36: LineSegment [constr] StartX=1170 StartY=-108.06 StartZ=0 EndX=1170 EndY=-118.06 EndZ=0
    g37: LineSegment [constr] StartX=1170 StartY=56.41 StartZ=0 EndX=1170 EndY=46.41 EndZ=0
    g38: LineSegment [constr] StartX=1170 StartY=46.41 StartZ=0 EndX=1180 EndY=46.41 EndZ=0
    g39: LineSegment [constr] StartX=1180 StartY=46.41 StartZ=0 EndX=1180 EndY=56.41 EndZ=0
    g40: LineSegment [constr] StartX=1180 StartY=56.41 StartZ=0 EndX=1170 EndY=56.41 EndZ=0
    g41: Circle CenterX=1170 CenterY=-108.06 CenterZ=0 NormalX=0 NormalY=0 NormalZ=1 AngleXU=0 Radius=1.5
    g42: Circle CenterX=1170 CenterY=-51.4132 CenterZ=0 NormalX=0 NormalY=0 NormalZ=1 AngleXU=0 Radius=1.5
    g43: Circle CenterX=1170 CenterY=46.41 CenterZ=0 NormalX=0 NormalY=0 NormalZ=1 AngleXU=0 Radius=1.5
    g44: Circle CenterX=1170 CenterY=103.145 CenterZ=0 NormalX=0 NormalY=0 NormalZ=1 AngleXU=0 Radius=1.5
  constraints (120):
    c: Coincident(g0,g-3)
    c: PointOnObject(g0,g-6)
    c: Horizontal(g0)
    c: Distance(g1) = 10
    c: Coincident(g1,g0)
    c: Horizontal(g1)
    c: Coincident(g2,g1)
    c: PointOnObject(g2,g-5)
    c: Vertical(g2)
    c: Coincident(g3,g0)
    c: PointOnObject(g3,g-4)
    c: Vertical(g3)
    c: Coincident(g4,g3)
    c: Vertical(g4)
    c: Distance(g5) = 20
    c: Coincident(g5,g4)
    c: PointOnObject(g5,g4)
    c: Coincident(g6,g7)
    c: Coincident(g7,g8)
    c: Coincident(g8,g9)
    c: Coincident(g9,g6)
    c: Horizontal(g6)
    c: Horizontal(g8)
    c: Vertical(g7)
    c: Vertical(g9)
    c: Distance(g7,g9) = 10
    c: Distance(g6,g8) = 10
    c: PointOnObject(g6,g3)
    c: Diameter(g10) = 3
    c: Coincident(g10,g8)
    c: Coincident(g11,g12)
    c: Coincident(g12,g13)
    c: Coincident(g13,g14)
    c: Coincident(g14,g11)
    c: Horizontal(g11)
    c: Horizontal(g13)
    c: Vertical(g12)
    c: Vertical(g14)
    c: Distance(g12,g14) = 10
    c: Distance(g11,g13) = 10
    c: Symmetric(g4,g4,g11)
    c: Diameter(g15) = 3
    c: Symmetric(g4,g4,g15)
    c: Coincident(g16,g17)
    c: Coincident(g17,g18)
    c: Coincident(g18,g19)
    c: Coincident(g19,g16)
    c: Vertical(g16)
    c: Vertical(g18)
    c: Horizontal(g17)
    c: Horizontal(g19)
    c: Distance(g16,g18) = 10
    c: Distance(g17,g19) = 10
    c: Coincident(g16,g4)
    c: Diameter(g20) = 3
    c: PointOnObject(g20,g4)
    c: Vertical(g21)
    c: Symmetric(g21,g21,g22)
    c: Horizontal(g22)
    c: PointOnObject(g23,g21)
    c: Horizontal(g23)
    c: PointOnObject(g24,g21)
    c: Horizontal(g24)
    c: Symmetric(g23,g24,g22)
    c: DistanceY(g22,g23) = 26.81
    c: Coincident(g25,g26)
    c: Coincident(g26,g27)
    c: Coincident(g27,g28)
    c: Coincident(g28,g25)
    c: Vertical(g25)
    c: Vertical(g27)
    c: Horizontal(g26)
    c: Horizontal(g28)
    c: Distance(g25,g27) = 10
    c: Distance(g26,g28) = 10
    c: PointOnObject(g25,g4)
    c: Coincident(g29,g30)
    c: Coincident(g30,g31)
    c: Coincident(g31,g32)
    c: Coincident(g32,g29)
    c: Vertical(g29)
    c: Vertical(g31)
    c: Horizontal(g30)
    c: Horizontal(g32)
    c: Distance(g29,g31) = 10
    c: Distance(g30,g32) = 10
    c: PointOnObject(g29,g4)
    c: Coincident(g33,g34)
    c: Coincident(g34,g35)
    c: Coincident(g35,g36)
    c: Coincident(g36,g33)
    c: Horizontal(g33)
    c: Horizontal(g35)
    c: Vertical(g34)
    c: Vertical(g36)
    c: Distance(g34,g36) = 10
    c: Distance(g33,g35) = 10
    c: Coincident(g37,g38)
    c: Coincident(g38,g39)
    c: Coincident(g39,g40)
    c: Coincident(g40,g37)
    c: Vertical(g37)
    c: Vertical(g39)
    c: Horizontal(g38)
    c: Horizontal(g40)
    c: Distance(g37,g39) = 10
    c: Distance(g38,g40) = 10
    c: Block(g11)
    c: Symmetric(g37,g29,g11)
    c: Symmetric(g35,g25,g11)
    c: Block(g8)
    c: DistanceY(g7,g33) = 50
    c: Diameter(g41) = 3
    c: Coincident(g41,g35)
    c: Diameter(g42) = 3
    c: PointOnObject(g42,g4)
    c: Diameter(g43) = 3
    c: Coincident(g43,g37)
    c: Diameter(g44) = 3
    c: Coincident(g44,g25)
FEATURE [PartDesign::Pocket] Pocket011
  BaseFeature = -> Pocket010
  Direction = (-4e-15,0.866026,-0.5)
  Length = 5
  Length2 = 5
  Profile = -> Sketch024
  ReferenceAxis = -> Sketch024 [N_Axis]
  Refine = true
  Suppressed = false
  Type = 0
FEATURE [Sketcher::SketchObject] Sketch025
  ArcFitTolerance = 1e-06
  AttachmentSupport = -> [Pocket011]
  ExternalGeometry = -> [Pocket011]
  FullyConstrained = true
  MakeInternals = false
  MapMode = 5
  Placement = pos=(34.0789,5.7e-14,257.027) rot=(0,1,0;0.13182rad)
  sketch-geometry (17):
    g0: LineSegment [constr] StartX=1155.95 StartY=345.9 StartZ=0 EndX=1145.95 EndY=345.9 EndZ=0
    g1: LineSegment [constr] StartX=1145.95 StartY=345.9 StartZ=0 EndX=1145.95 EndY=335.9 EndZ=0
    g2: LineSegment [constr] StartX=1145.95 StartY=335.9 StartZ=0 EndX=1155.95 EndY=335.9 EndZ=0
    g3: LineSegment [constr] StartX=1155.95 StartY=335.9 StartZ=0 EndX=1155.95 EndY=345.9 EndZ=0
    g4: LineSegment [constr] StartX=1155.95 StartY=173.891 StartZ=0 EndX=1155.95 EndY=183.891 EndZ=0
    g5: LineSegment [constr] StartX=1155.95 StartY=183.891 StartZ=0 EndX=1145.95 EndY=183.891 EndZ=0
    g6: LineSegment [constr] StartX=1145.95 StartY=183.891 StartZ=0 EndX=1145.95 EndY=173.891 EndZ=0
    g7: LineSegment [constr] StartX=1145.95 StartY=173.891 StartZ=0 EndX=1155.95 EndY=173.891 EndZ=0
    g8: LineSegment [constr] StartX=1155.95 StartY=259.896 StartZ=0 EndX=1155.95 EndY=269.896 EndZ=0
    g9: LineSegment [constr] StartX=1155.95 StartY=269.896 StartZ=0 EndX=1145.95 EndY=269.896 EndZ=0
    g10: LineSegment [constr] StartX=1145.95 StartY=269.896 StartZ=0 EndX=1145.95 EndY=259.896 EndZ=0
    g11: LineSegment [constr] StartX=1145.95 StartY=259.896 StartZ=0 EndX=1155.95 EndY=259.896 EndZ=0
    g12: LineSegment [constr] StartX=1145.95 StartY=335.9 StartZ=0 EndX=1145.95 EndY=269.896 EndZ=0
    g13: LineSegment [constr] StartX=1145.95 StartY=259.896 StartZ=0 EndX=1145.95 EndY=183.891 EndZ=0
    g14: Circle CenterX=1145.95 CenterY=183.891 CenterZ=0 NormalX=0 NormalY=0 NormalZ=1 AngleXU=0 Radius=1.5
    g15: Circle CenterX=1145.95 CenterY=259.896 CenterZ=0 NormalX=0 NormalY=0 NormalZ=1 AngleXU=0 Radius=1.5
    g16: Circle CenterX=1145.95 CenterY=335.9 CenterZ=0 NormalX=0 NormalY=0 NormalZ=1 AngleXU=0 Radius=1.5
  constraints (43):
    c: Coincident(g0,g1)
    c: Coincident(g1,g2)
    c: Coincident(g2,g3)
    c: Coincident(g3,g0)
    c: Horizontal(g0)
    c: Horizontal(g2)
    c: Vertical(g1)
    c: Vertical(g3)
    c: Distance(g1,g3) = 10
    c: Distance(g0,g2) = 10
    c: Coincident(g0,g-4)
    c: Coincident(g4,g5)
    c: Coincident(g5,g6)
    c: Coincident(g6,g7)
    c: Coincident(g7,g4)
    c: Vertical(g4)
    c: Vertical(g6)
    c: Horizontal(g5)
    c: Horizontal(g7)
    c: Distance(g4,g6) = 10
    c: Distance(g5,g7) = 10
    c: Coincident(g4,g-3)
    c: Coincident(g8,g9)
    c: Coincident(g9,g10)
    c: Coincident(g10,g11)
    c: Coincident(g11,g8)
    c: Vertical(g8)
    c: Vertical(g10)
    c: Horizontal(g9)
    c: Horizontal(g11)
    c: Distance(g8,g10) = 10
    c: Distance(g9,g11) = 10
    c: Symmetric(g-3,g-3,g8)
    c: Coincident(g12,g1)
    c: Coincident(g12,g9)
    c: Coincident(g13,g10)
    c: Coincident(g13,g5)
    c: Diameter(g14) = 3
    c: Coincident(g14,g5)
    c: Diameter(g15) = 3
    c: Coincident(g15,g10)
    c: Diameter(g16) = 3
    c: Coincident(g16,g1)
FEATURE [PartDesign::Pocket] Pocket012
  BaseFeature = -> Pocket011
  Direction = (-0.131439,0,-0.991324)
  Length = 5
  Length2 = 5
  Profile = -> Sketch025
  ReferenceAxis = -> Sketch025 [N_Axis]
  Refine = true
  Suppressed = false
  Type = 0
FEATURE [Sketcher::SketchObject] Sketch026
  ArcFitTolerance = 1e-06
  AttachmentSupport = -> [Pocket012]
  ExternalGeometry = -> [Pocket012]
  FullyConstrained = false
  MakeInternals = false
  MapMode = 5
  Placement = pos=(0,-7.51e-14,-341.2) rot=(0,0,1;0rad)
  sketch-geometry (27):
    g0: LineSegment [constr] StartX=1180 StartY=345.9 StartZ=0 EndX=1170 EndY=345.9 EndZ=0
    g1: LineSegment [constr] StartX=1170 StartY=345.9 StartZ=0 EndX=1170 EndY=335.9 EndZ=0
    g2: LineSegment [constr] StartX=1170 StartY=335.9 StartZ=0 EndX=1180 EndY=335.9 EndZ=0
    g3: LineSegment [constr] StartX=1180 StartY=335.9 StartZ=0 EndX=1180 EndY=345.9 EndZ=0
    g4: LineSegment [constr] StartX=1180 StartY=-2.1 StartZ=0 EndX=1180 EndY=7.9 EndZ=0
    g5: LineSegment [constr] StartX=1180 StartY=7.9 StartZ=0 EndX=1170 EndY=7.9 EndZ=0
    g6: LineSegment [constr] StartX=1170 StartY=7.9 StartZ=0 EndX=1170 EndY=-2.1 EndZ=0
    g7: LineSegment [constr] StartX=1170 StartY=-2.1 StartZ=0 EndX=1180 EndY=-2.1 EndZ=0
    g8: LineSegment [constr] StartX=1180 StartY=171.9 StartZ=0 EndX=1180 EndY=181.9 EndZ=0
    g9: LineSegment [constr] StartX=1180 StartY=181.9 StartZ=0 EndX=1170 EndY=181.9 EndZ=0
    g10: LineSegment [constr] StartX=1170 StartY=181.9 StartZ=0 EndX=1170 EndY=171.9 EndZ=0
    g11: LineSegment [constr] StartX=1170 StartY=171.9 StartZ=0 EndX=1180 EndY=171.9 EndZ=0
    g12: LineSegment [constr] StartX=1170 StartY=181.9 StartZ=0 EndX=1170 EndY=335.9 EndZ=0
    g13: LineSegment [constr] StartX=1170 StartY=258.9 StartZ=0 EndX=1180 EndY=258.9 EndZ=0
    g14: LineSegment [constr] StartX=1180 StartY=258.9 StartZ=0 EndX=1180 EndY=268.9 EndZ=0
    g15: LineSegment [constr] StartX=1180 StartY=268.9 StartZ=0 EndX=1170 EndY=268.9 EndZ=0
    g16: LineSegment [constr] StartX=1170 StartY=268.9 StartZ=0 EndX=1170 EndY=258.9 EndZ=0
    g17: LineSegment [constr] StartX=1170 StartY=171.9 StartZ=0 EndX=1170 EndY=7.9 EndZ=0
    g18: LineSegment [constr] StartX=1170 StartY=89.9 StartZ=0 EndX=1180 EndY=89.9 EndZ=0
    g19: LineSegment [constr] StartX=1180 StartY=89.9 StartZ=0 EndX=1180 EndY=99.9 EndZ=0
    g20: LineSegment [constr] StartX=1180 StartY=99.9 StartZ=0 EndX=1170 EndY=99.9 EndZ=0
    g21: LineSegment [constr] StartX=1170 StartY=99.9 StartZ=0 EndX=1170 EndY=89.9 EndZ=0
    g22: Circle CenterX=1170 CenterY=335.9 CenterZ=0 NormalX=0 NormalY=0 NormalZ=1 AngleXU=0 Radius=1.5
    g23: Circle CenterX=1170 CenterY=258.9 CenterZ=0 NormalX=0 NormalY=0 NormalZ=1 AngleXU=0 Radius=1.5
    g24: Circle CenterX=1170 CenterY=171.9 CenterZ=0 NormalX=0 NormalY=0 NormalZ=1 AngleXU=0 Radius=1.5
    g25: Circle CenterX=1170 CenterY=89.9 CenterZ=0 NormalX=0 NormalY=0 NormalZ=1 AngleXU=0 Radius=1.5
    g26: Circle CenterX=1170 CenterY=7.9 CenterZ=0 NormalX=0 NormalY=0 NormalZ=1 AngleXU=0 Radius=1.5
  constraints (59):
    c: Coincident(g0,g1)
    c: Coincident(g1,g2)
    c: Coincident(g2,g3)
    c: Coincident(g3,g0)
    c: Horizontal(g0)
    c: Horizontal(g2)
    c: Vertical(g1)
    c: Vertical(g3)
    c: Distance(g1,g3) = 10
    c: Distance(g0,g2) = 10
    c: Coincident(g0,g-3)
    c: Coincident(g4,g5)
    c: Coincident(g5,g6)
    c: Coincident(g6,g7)
    c: Coincident(g7,g4)
    c: Vertical(g4)
    c: Vertical(g6)
    c: Horizontal(g5)
    c: Horizontal(g7)
    c: Distance(g4,g6) = 10
    c: Distance(g5,g7) = 10
    c: Coincident(g4,g-3)
    c: Coincident(g8,g9)
    c: Coincident(g9,g10)
    c: Coincident(g10,g11)
    c: Coincident(g11,g8)
    c: Vertical(g8)
    c: Vertical(g10)
    c: Horizontal(g9)
    c: Horizontal(g11)
    c: Distance(g8,g10) = 10
    c: Distance(g9,g11) = 10
    c: Symmetric(g-3,g-3,g8)
    c: Coincident(g12,g9)
    c: Coincident(g12,g1)
    c: Coincident(g13,g14)
    c: Coincident(g14,g15)
    c: Coincident(g15,g16)
    c: Coincident(g16,g13)
    c: Horizontal(g13)
    c: Horizontal(g15)
    c: Vertical(g14)
    c: Vertical(g16)
    c: Distance(g13,g15) = 10
    c: Symmetric(g12,g12,g13)
    c: PointOnObject(g14,g-3)
    c: Coincident(g17,g10)
    c: Coincident(g17,g5)
    c: Coincident(g18,g19)
    c: Coincident(g19,g20)
    c: Coincident(g20,g21)
    c: Coincident(g21,g18)
    c: Horizontal(g18)
    c: Horizontal(g20)
    c: Vertical(g19)
    c: Vertical(g21)
    c: Distance(g18,g20) = 10
    c: Symmetric(g17,g17,g18)
    c: PointOnObject(g19,g-3)
FEATURE [PartDesign::Pocket] Pocket013
  BaseFeature = -> Pocket012
  Direction = (0,0,-1)
  Length = 5
  Length2 = 5
  Profile = -> Sketch026
  ReferenceAxis = -> Sketch026 [N_Axis]
  Refine = true
  Suppressed = false
  Type = 0
FEATURE [PartDesign::SubShapeBinder] Binder005
  BindCopyOnChange = 0
  BindMode = 2
  ClaimChildren = false
  Context = -> Part [Body003.Binder005.]
  Fuse = false
  MakeFace = true
  OffsetFill = false
  OffsetIntersection = false
  OffsetJoinType = 0
  OffsetOpenResult = false
  PartialLoad = false
  Refine = true
  Relative = true
  _Version = 2
FEATURE [Sketcher::SketchObject] Sketch027
  ArcFitTolerance = 1e-06
  AttachmentSupport = -> [Pad004]
  ExternalGeometry = -> [Binder005]
  FullyConstrained = false
  MakeInternals = false
  MapMode = 5
  Placement = pos=(0,87.9016,-50.75) rot=(0,0.866025,0.5;3.14159rad)
  sketch-geometry (7):
    g0: Circle CenterX=-890 CenterY=167.291 CenterZ=0 NormalX=0 NormalY=0 NormalZ=1 AngleXU=0 Radius=1.5
    g1: Circle CenterX=-890 CenterY=105.145 CenterZ=0 NormalX=0 NormalY=0 NormalZ=1 AngleXU=0 Radius=1.5
    g2: Circle CenterX=-890 CenterY=48.4101 CenterZ=0 NormalX=0 NormalY=0 NormalZ=1 AngleXU=0 Radius=1.5
    g3: Circle CenterX=-890 CenterY=-0.457073 CenterZ=0 NormalX=0 NormalY=0 NormalZ=1 AngleXU=0 Radius=1.5
    g4: Circle CenterX=-890 CenterY=-49.4131 CenterZ=0 NormalX=0 NormalY=0 NormalZ=1 AngleXU=0 Radius=1.5
    g5: Circle CenterX=-890 CenterY=-106.06 CenterZ=0 NormalX=0 NormalY=0 NormalZ=1 AngleXU=0 Radius=1.5
    g6: Circle CenterX=-890 CenterY=-166.06 CenterZ=0 NormalX=0 NormalY=0 NormalZ=1 AngleXU=0 Radius=1.5
  constraints (7):
    c: Coincident(g0,g-3)
    c: Coincident(g1,g-4)
    c: Coincident(g2,g-5)
    c: Coincident(g3,g-6)
    c: Coincident(g4,g-7)
    c: Coincident(g5,g-8)
    c: Coincident(g6,g-9)
FEATURE [PartDesign::Pocket] Pocket014
  BaseFeature = -> Pad004
  Direction = (0,-0.866025,0.5)
  Length = 5
  Length2 = 5
  Profile = -> Sketch027
  ReferenceAxis = -> Sketch027 [N_Axis]
  Refine = true
  Suppressed = false
  Type = 0
FEATURE [PartDesign::SubShapeBinder] Binder006
  BindCopyOnChange = 0
  BindMode = 2
  ClaimChildren = false
  Context = -> Part [Body007.Binder006.]
  Fuse = false
  MakeFace = true
  OffsetFill = false
  OffsetIntersection = false
  OffsetJoinType = 0
  OffsetOpenResult = false
  PartialLoad = false
  Refine = true
  Relative = true
  _Version = 2
FEATURE [Sketcher::SketchObject] Sketch028
  ArcFitTolerance = 1e-06
  AttachmentSupport = -> [Binder006]
  ExternalGeometry = -> [Binder006]
  FullyConstrained = true
  MakeInternals = false
  MapMode = 5
  Placement = pos=(0,-0.1,0) rot=(0,0.707107,0.707107;3.14159rad)
  sketch-geometry (8):
    g0: LineSegment StartX=-627 StartY=-343.2 StartZ=0 EndX=-627 EndY=133.254 EndZ=0
    g1: LineSegment StartX=-625 StartY=-341.2 StartZ=0 EndX=-625 EndY=131.254 EndZ=0
    g2: LineSegment StartX=-627 StartY=133.254 StartZ=0 EndX=-605.052 EndY=134.764 EndZ=0
    g3: LineSegment StartX=-605.052 StartY=134.764 StartZ=0 EndX=-605.052 EndY=132.764 EndZ=0
    g4: LineSegment StartX=-605.052 StartY=132.764 StartZ=0 EndX=-625 EndY=131.254 EndZ=0
    g5: LineSegment StartX=-605 StartY=-343.2 StartZ=0 EndX=-627 EndY=-343.2 EndZ=0
    g6: LineSegment StartX=-605 StartY=-343.2 StartZ=0 EndX=-605 EndY=-341.2 EndZ=0
    g7: LineSegment StartX=-605 StartY=-341.2 StartZ=0 EndX=-625 EndY=-341.2 EndZ=0
  constraints (23):
    c: Vertical(g0)
    c: Vertical(g1)
    c: PointOnObject(g0,g-4)
    c: Distance(g2) = 22
    c: Coincident(g2,g0)
    c: PointOnObject(g2,g-4)
    c: Distance(g3) = 2
    c: Coincident(g3,g2)
    c: Vertical(g3)
    c: Coincident(g4,g3)
    c: Coincident(g1,g4)
    c: DistanceY(g1,g0) = 2
    c: Coincident(g5,g-3)
    c: Horizontal(g5)
    c: Distance(g6) = 2
    c: Coincident(g6,g5)
    c: Vertical(g6)
    c: Coincident(g7,g6)
    c: Horizontal(g7)
    c: Coincident(g7,g1)
    c: Coincident(g5,g0)
    c: DistanceX(g0,g1) = 2
    c: DistanceX(g7,g7) = 20
FEATURE [PartDesign::Pad] Pad009
  Direction = (0,1,-2e-16)
  Length = 350
  Length2 = 10
  Profile = -> Sketch028
  ReferenceAxis = -> Sketch028 [N_Axis]
  Refine = true
  Suppressed = false
  Type = 0
FEATURE [Sketcher::SketchObject] Sketch029
  ArcFitTolerance = 1e-06
  AttachmentSupport = -> [Pad009]
  ExternalGeometry = -> [Binder006,Pad009]
  FullyConstrained = true
  MakeInternals = false
  MapMode = 5
  Placement = pos=(627,0,0) rot=(0.57735,0.57735,0.57735;2.0944rad)
  sketch-geometry (3):
    g0: LineSegment StartX=-0.1 StartY=-203.2 StartZ=0 EndX=195.023 EndY=134.764 EndZ=0
    g1: LineSegment StartX=195.023 StartY=134.764 StartZ=0 EndX=-0.1 EndY=134.764 EndZ=0
    g2: LineSegment StartX=-0.1 StartY=134.764 StartZ=0 EndX=-0.1 EndY=-203.2 EndZ=0
  constraints (8):
    c: Angle(g-1,g0) = 1.0472
    c: Coincident(g0,g-3)
    c: PointOnObject(g0,g-4)
    c: Coincident(g1,g0)
    c: Horizontal(g1)
    c: Coincident(g2,g1)
    c: Coincident(g2,g0)
    c: Vertical(g2)
FEATURE [PartDesign::Pocket] Pocket015
  BaseFeature = -> Pad009
  Direction = (-1,0,0)
  Length = 5
  Length2 = 5
  Profile = -> Sketch029
  ReferenceAxis = -> Sketch029 [N_Axis]
  Refine = true
  Suppressed = false
  Type = 1
FEATURE [Sketcher::SketchObject] Sketch030
  ArcFitTolerance = 1e-06
  AttachmentSupport = -> [Pocket015]
  ExternalGeometry = -> [Pocket015]
  FullyConstrained = true
  MakeInternals = false
  MapMode = 5
  Placement = pos=(625,0,0) rot=(0.57735,-0.57735,-0.57735;2.0944rad)
  sketch-geometry (7):
    g0: LineSegment StartX=0.1 StartY=-341.2 StartZ=0 EndX=0.1 EndY=-203.2 EndZ=0
    g1: LineSegment StartX=0.1 StartY=-203.2 StartZ=0 EndX=-192.997 EndY=131.254 EndZ=0
    g2: LineSegment StartX=-192.997 StartY=131.254 StartZ=0 EndX=-194.997 EndY=131.254 EndZ=0
    g3: LineSegment StartX=-194.997 StartY=131.254 StartZ=0 EndX=-1.9 EndY=-203.2 EndZ=0
    g4: LineSegment StartX=0.1 StartY=-341.2 StartZ=0 EndX=-1.9 EndY=-341.2 EndZ=0
    g5: LineSegment StartX=-1.9 StartY=-341.2 StartZ=0 EndX=-1.9 EndY=-203.2 EndZ=0
    g6: LineSegment [constr] StartX=-1.9 StartY=-203.2 StartZ=0 EndX=0.1 EndY=-203.2 EndZ=0
  constraints (17):
    c: Coincident(g0,g-3)
    c: Coincident(g0,g-4)
    c: Coincident(g1,g0)
    c: Coincident(g1,g-4)
    c: Distance(g2) = 2
    c: Coincident(g2,g1)
    c: Horizontal(g2)
    c: Coincident(g3,g2)
    c: Distance(g4) = 2
    c: Coincident(g4,g0)
    c: Horizontal(g4)
    c: Coincident(g5,g4)
    c: Coincident(g5,g3)
    c: Vertical(g5)
    c: Coincident(g6,g3)
    c: Coincident(g6,g0)
    c: Horizontal(g6)
FEATURE [PartDesign::Pad] Pad010
  BaseFeature = -> Pocket015
  Direction = (-1,0,0)
  Length = 20
  Length2 = 10
  Profile = -> Sketch030
  ReferenceAxis = -> Sketch030 [N_Axis]
  Refine = true
  Suppressed = false
  Type = 0
FEATURE [Sketcher::SketchObject] Sketch031
  ArcFitTolerance = 1e-06
  AttachmentSupport = -> [Binder006]
  ExternalGeometry = -> [Binder006]
  FullyConstrained = true
  MakeInternals = false
  MapMode = 5
  Placement = pos=(0,-0.1,0) rot=(0,0.707107,0.707107;3.14159rad)
  sketch-geometry (3):
    g0: Circle CenterX=-615 CenterY=-213.2 CenterZ=0 NormalX=0 NormalY=0 NormalZ=1 AngleXU=0 Radius=1.5
    g1: Circle CenterX=-616.359 CenterY=-273.2 CenterZ=0 NormalX=0 NormalY=0 NormalZ=1 AngleXU=0 Radius=1.5
    g2: Circle CenterX=-615 CenterY=-333.2 CenterZ=0 NormalX=0 NormalY=0 NormalZ=1 AngleXU=0 Radius=1.5
  constraints (6):
    c: Coincident(g0,g-3)
    c: Equal(g0,g-3)
    c: Coincident(g1,g-4)
    c: Equal(g1,g-4)
    c: Coincident(g2,g-5)
    c: Equal(g2,g-5)
FEATURE [PartDesign::Pocket] Pocket016
  BaseFeature = -> Pad010
  Direction = (0,-1,2e-16)
  Length = 5
  Length2 = 5
  Profile = -> Sketch031
  ReferenceAxis = -> Sketch031 [N_Axis]
  Refine = true
  Reversed = true
  Suppressed = false
  Type = 0
FEATURE [Sketcher::SketchObject] Sketch032
  ArcFitTolerance = 1e-06
  AttachmentSupport = -> [Pocket016]
  ExternalGeometry = -> [Pocket016]
  FullyConstrained = false
  MakeInternals = false
  MapMode = 5
  Placement = pos=(1.797e-13,87.9131,-50.7566) rot=(1,0,0;1.0472rad)
  sketch-geometry (26):
    g0: LineSegment [constr] StartX=605 StartY=-176.026 StartZ=0 EndX=615 EndY=-176.026 EndZ=0
    g1: LineSegment [constr] StartX=615 StartY=-176.026 StartZ=0 EndX=615 EndY=-166.026 EndZ=0
    g2: LineSegment [constr] StartX=615 StartY=-166.026 StartZ=0 EndX=605 EndY=-166.026 EndZ=0
    g3: LineSegment [constr] StartX=605 StartY=-166.026 StartZ=0 EndX=605 EndY=-176.026 EndZ=0
    g4: LineSegment [constr] StartX=605 StartY=210.167 StartZ=0 EndX=605 EndY=200.167 EndZ=0
    g5: LineSegment [constr] StartX=605 StartY=200.167 StartZ=0 EndX=615 EndY=200.167 EndZ=0
    g6: LineSegment [constr] StartX=615 StartY=200.167 StartZ=0 EndX=615 EndY=210.167 EndZ=0
    g7: LineSegment [constr] StartX=615 StartY=210.167 StartZ=0 EndX=605 EndY=210.167 EndZ=0
    g8: LineSegment [constr] StartX=605 StartY=17.0704 StartZ=0 EndX=615 EndY=17.0704 EndZ=0
    g9: LineSegment [constr] StartX=615 StartY=17.0704 StartZ=0 EndX=615 EndY=27.0704 EndZ=0
    g10: LineSegment [constr] StartX=615 StartY=27.0704 StartZ=0 EndX=605 EndY=27.0704 EndZ=0
    g11: LineSegment [constr] StartX=605 StartY=27.0704 StartZ=0 EndX=605 EndY=17.0704 EndZ=0
    g12: LineSegment [constr] StartX=615 StartY=-74.478 StartZ=0 EndX=605 EndY=-74.478 EndZ=0
    g13: LineSegment [constr] StartX=615 StartY=113.619 StartZ=0 EndX=615 EndY=123.619 EndZ=0
    g14: LineSegment [constr] StartX=615 StartY=123.619 StartZ=0 EndX=605 EndY=123.619 EndZ=0
    g15: LineSegment [constr] StartX=605 StartY=123.619 StartZ=0 EndX=605 EndY=113.619 EndZ=0
    g16: LineSegment [constr] StartX=605 StartY=113.619 StartZ=0 EndX=615 EndY=113.619 EndZ=0
    g17: LineSegment [constr] StartX=615 StartY=113.619 StartZ=0 EndX=615 EndY=200.167 EndZ=0
    g18: LineSegment [constr] StartX=615 StartY=113.619 StartZ=0 EndX=615 EndY=17.0704 EndZ=0
    g19: LineSegment [constr] StartX=615 StartY=-166.026 StartZ=0 EndX=615 EndY=-74.478 EndZ=0
    g20: LineSegment [constr] StartX=615 StartY=17.0704 StartZ=0 EndX=615 EndY=-74.478 EndZ=0
    g21: Circle CenterX=615 CenterY=-166.026 CenterZ=0 NormalX=0 NormalY=0 NormalZ=1 AngleXU=0 Radius=1.5
    g22: Circle CenterX=615 CenterY=17.0704 CenterZ=0 NormalX=0 NormalY=0 NormalZ=1 AngleXU=0 Radius=1.5
    g23: Circle CenterX=615 CenterY=113.619 CenterZ=0 NormalX=0 NormalY=0 NormalZ=1 AngleXU=0 Radius=1.5
    g24: Circle CenterX=615 CenterY=200.167 CenterZ=0 NormalX=0 NormalY=0 NormalZ=1 AngleXU=0 Radius=1.5
    g25: Circle CenterX=615 CenterY=-74.478 CenterZ=0 NormalX=0 NormalY=0 NormalZ=1 AngleXU=0 Radius=1.5
FEATURE [PartDesign::Pocket] Pocket017
  BaseFeature = -> Pocket016
  Direction = (1.3e-15,0.866026,-0.5)
  Length = 5
  Length2 = 5
  Profile = -> Sketch032
  ReferenceAxis = -> Sketch032 [N_Axis]
  Refine = true
  Suppressed = false
  Type = 0
FEATURE [Sketcher::SketchObject] Sketch033
  ArcFitTolerance = 1e-06
  AttachmentSupport = -> [Pocket017]
  ExternalGeometry = -> [Pocket017]
  FullyConstrained = false
  MakeInternals = false
  MapMode = 5
  Placement = pos=(0,-7.51e-14,-341.2) rot=(0,0,1;0rad)
  sketch-geometry (28):
    g0: LineSegment [constr] StartX=615 StartY=349.9 StartZ=0 EndX=615 EndY=1.9 EndZ=0
    g1: LineSegment [constr] StartX=615 StartY=175.9 StartZ=0 EndX=605 EndY=175.9 EndZ=0
    g2: LineSegment [constr] StartX=605 StartY=175.9 StartZ=0 EndX=605 EndY=185.9 EndZ=0
    g3: LineSegment [constr] StartX=605 StartY=185.9 StartZ=0 EndX=615 EndY=185.9 EndZ=0
    g4: LineSegment [constr] StartX=615 StartY=185.9 StartZ=0 EndX=615 EndY=175.9 EndZ=0
    g5: LineSegment [constr] StartX=605 StartY=185.9 StartZ=0 EndX=605 EndY=349.9 EndZ=0
    g6: LineSegment [constr] StartX=605 StartY=267.9 StartZ=0 EndX=615 EndY=267.9 EndZ=0
    g7: LineSegment [constr] StartX=615 StartY=267.9 StartZ=0 EndX=615 EndY=277.9 EndZ=0
    g8: LineSegment [constr] StartX=615 StartY=277.9 StartZ=0 EndX=605 EndY=277.9 EndZ=0
    g9: LineSegment [constr] StartX=605 StartY=277.9 StartZ=0 EndX=605 EndY=267.9 EndZ=0
    g10: LineSegment [constr] StartX=605 StartY=349.9 StartZ=0 EndX=605 EndY=339.9 EndZ=0
    g11: LineSegment [constr] StartX=605 StartY=339.9 StartZ=0 EndX=615 EndY=339.9 EndZ=0
    g12: LineSegment [constr] StartX=615 StartY=339.9 StartZ=0 EndX=615 EndY=349.9 EndZ=0
    g13: LineSegment [constr] StartX=615 StartY=349.9 StartZ=0 EndX=605 EndY=349.9 EndZ=0
    g14: LineSegment [constr] StartX=615 StartY=1.9 StartZ=0 EndX=615 EndY=11.9 EndZ=0
    g15: LineSegment [constr] StartX=615 StartY=11.9 StartZ=0 EndX=605 EndY=11.9 EndZ=0
    g16: LineSegment [constr] StartX=605 StartY=11.9 StartZ=0 EndX=605 EndY=1.9 EndZ=0
    g17: LineSegment [constr] StartX=605 StartY=1.9 StartZ=0 EndX=615 EndY=1.9 EndZ=0
    g18: LineSegment [constr] StartX=605 StartY=175.9 StartZ=0 EndX=605 EndY=11.9 EndZ=0
    g19: LineSegment [constr] StartX=605 StartY=93.9 StartZ=0 EndX=615 EndY=93.9 EndZ=0
    g20: LineSegment [constr] StartX=615 StartY=93.9 StartZ=0 EndX=615 EndY=103.9 EndZ=0
    g21: LineSegment [constr] StartX=615 StartY=103.9 StartZ=0 EndX=605 EndY=103.9 EndZ=0
    g22: LineSegment [constr] StartX=605 StartY=103.9 StartZ=0 EndX=605 EndY=93.9 EndZ=0
    g23: Circle CenterX=615 CenterY=11.9 CenterZ=0 NormalX=0 NormalY=0 NormalZ=1 AngleXU=0 Radius=1.5
    g24: Circle CenterX=615 CenterY=93.9 CenterZ=0 NormalX=0 NormalY=0 NormalZ=1 AngleXU=0 Radius=1.5
    g25: Circle CenterX=615 CenterY=175.9 CenterZ=0 NormalX=0 NormalY=0 NormalZ=1 AngleXU=0 Radius=1.5
    g26: Circle CenterX=615 CenterY=267.9 CenterZ=0 NormalX=0 NormalY=0 NormalZ=1 AngleXU=0 Radius=1.5
    g27: Circle CenterX=615 CenterY=339.9 CenterZ=0 NormalX=0 NormalY=0 NormalZ=1 AngleXU=0 Radius=1.5
  constraints (59):
    c: Symmetric(g-4,g-4,g0)
    c: Symmetric(g-3,g-3,g0)
    c: Coincident(g1,g2)
    c: Coincident(g2,g3)
    c: Coincident(g3,g4)
    c: Coincident(g4,g1)
    c: Horizontal(g1)
    c: Horizontal(g3)
    c: Vertical(g2)
    c: Vertical(g4)
    c: Symmetric(g0,g0,g1)
    c: DistanceY(g2,g2) = 10
    c: DistanceX(g3,g3) = 10
    c: Coincident(g5,g2)
    c: Coincident(g5,g-4)
    c: Coincident(g6,g7)
    c: Coincident(g7,g8)
    c: Coincident(g8,g9)
    c: Coincident(g9,g6)
    c: Horizontal(g6)
    c: Horizontal(g8)
    c: Vertical(g7)
    c: Vertical(g9)
    c: Distance(g6,g8) = 10
    c: Symmetric(g5,g5,g6)
    c: Coincident(g10,g11)
    c: Coincident(g11,g12)
    c: Coincident(g12,g13)
    c: Coincident(g13,g10)
    c: Vertical(g10)
    c: Vertical(g12)
    c: Horizontal(g11)
    c: Horizontal(g13)
    c: Distance(g11,g13) = 10
    c: Coincident(g10,g5)
    c: Coincident(g14,g15)
    c: Coincident(g15,g16)
    c: Coincident(g16,g17)
    c: Coincident(g17,g14)
    c: Vertical(g14)
    c: Vertical(g16)
    c: Horizontal(g15)
    c: Horizontal(g17)
    c: Distance(g14,g16) = 10
    c: Distance(g15,g17) = 10
    c: Coincident(g14,g0)
    c: Coincident(g18,g1)
    c: Coincident(g18,g15)
    c: Coincident(g19,g20)
    c: Coincident(g20,g21)
    c: Coincident(g21,g22)
    c: Coincident(g22,g19)
    c: Horizontal(g19)
    c: Horizontal(g21)
    c: Vertical(g20)
    c: Vertical(g22)
    c: Distance(g19,g21) = 10
    c: Symmetric(g18,g18,g19)
    c: Coincident(g25,g1)
FEATURE [PartDesign::SubShapeBinder] Binder007
  BindCopyOnChange = 0
  BindMode = 2
  ClaimChildren = false
  Context = -> Part [Body003.Binder007.]
  Fuse = false
  MakeFace = true
  OffsetFill = false
  OffsetIntersection = false
  OffsetJoinType = 0
  OffsetOpenResult = false
  PartialLoad = false
  Refine = true
  Relative = true
  _Version = 2
FEATURE [Sketcher::SketchObject] Sketch034
  ArcFitTolerance = 1e-06
  AttachmentSupport = -> [Binder007]
  ExternalGeometry = -> [Binder007]
  FullyConstrained = true
  MakeInternals = false
  MapMode = 5
  Placement = pos=(1.797e-13,87.9131,-50.7566) rot=(1,0,0;1.0472rad)
  sketch-geometry (5):
    g0: Circle CenterX=615 CenterY=-166.026 CenterZ=0 NormalX=0 NormalY=0 NormalZ=1 AngleXU=0 Radius=1.5
    g1: Circle CenterX=615 CenterY=-74.478 CenterZ=0 NormalX=0 NormalY=0 NormalZ=1 AngleXU=0 Radius=1.5
    g2: Circle CenterX=615 CenterY=17.0704 CenterZ=0 NormalX=0 NormalY=0 NormalZ=1 AngleXU=0 Radius=1.5
    g3: Circle CenterX=615 CenterY=113.619 CenterZ=0 NormalX=0 NormalY=0 NormalZ=1 AngleXU=0 Radius=1.5
    g4: Circle CenterX=615 CenterY=200.167 CenterZ=0 NormalX=0 NormalY=0 NormalZ=1 AngleXU=0 Radius=1.5
  constraints (10):
    c: Coincident(g0,g-7)
    c: Equal(g0,g-7)
    c: Coincident(g1,g-6)
    c: Equal(g1,g-6)
    c: Coincident(g2,g-5)
    c: Equal(g2,g-5)
    c: Coincident(g3,g-4)
    c: Equal(g3,g-4)
    c: Coincident(g4,g-3)
    c: Equal(g4,g-3)
FEATURE [PartDesign::Pocket] Pocket019
  BaseFeature = -> Pocket014
  Direction = (1.3e-15,0.866026,-0.5)
  Length = 5
  Length2 = 5
  Profile = -> Sketch034
  ReferenceAxis = -> Sketch034 [N_Axis]
  Refine = true
  Reversed = true
  Suppressed = false
  Type = 0
FEATURE [PartDesign::Pocket] Pocket018
  BaseFeature = -> Pocket017
  Direction = (0,0,-1)
  Length = 5
  Length2 = 5
  Profile = -> Sketch033
  ReferenceAxis = -> Sketch033 [N_Axis]
  Refine = true
  Suppressed = false
  Type = 0
FEATURE [Sketcher::SketchObject] Sketch035
  ArcFitTolerance = 1e-06
  AttachmentSupport = -> [Pocket018]
  ExternalGeometry = -> [Pocket018]
  FullyConstrained = false
  MakeInternals = false
  MapMode = 5
  Placement = pos=(12.0795,3.87e-14,175.563) rot=(0,1,0;0.068696rad)
  sketch-geometry (16):
    g0: LineSegment [constr] StartX=594.374 StartY=195.023 StartZ=0 EndX=604.374 EndY=195.023 EndZ=0
    g1: LineSegment [constr] StartX=604.374 StartY=195.023 StartZ=0 EndX=604.374 EndY=205.023 EndZ=0
    g2: LineSegment [constr] StartX=604.374 StartY=205.023 StartZ=0 EndX=594.374 EndY=205.023 EndZ=0
    g3: LineSegment [constr] StartX=594.374 StartY=205.023 StartZ=0 EndX=594.374 EndY=195.023 EndZ=0
    g4: LineSegment [constr] StartX=594.374 StartY=349.9 StartZ=0 EndX=594.374 EndY=339.9 EndZ=0
    g5: LineSegment [constr] StartX=594.374 StartY=339.9 StartZ=0 EndX=604.374 EndY=339.9 EndZ=0
    g6: LineSegment [constr] StartX=604.374 StartY=339.9 StartZ=0 EndX=604.374 EndY=349.9 EndZ=0
    g7: LineSegment [constr] StartX=604.374 StartY=349.9 StartZ=0 EndX=594.374 EndY=349.9 EndZ=0
    g8: LineSegment [constr] StartX=604.374 StartY=339.9 StartZ=0 EndX=604.374 EndY=205.023 EndZ=0
    g9: LineSegment [constr] StartX=604.374 StartY=272.462 StartZ=0 EndX=604.374 EndY=282.462 EndZ=0
    g10: LineSegment [constr] StartX=604.374 StartY=282.462 StartZ=0 EndX=594.374 EndY=282.462 EndZ=0
    g11: LineSegment [constr] StartX=594.374 StartY=282.462 StartZ=0 EndX=594.374 EndY=272.462 EndZ=0
    g12: LineSegment [constr] StartX=594.374 StartY=272.462 StartZ=0 EndX=604.374 EndY=272.462 EndZ=0
    g13: Circle CenterX=604.374 CenterY=272.462 CenterZ=0 NormalX=0 NormalY=0 NormalZ=1 AngleXU=0 Radius=1.5
    g14: Circle CenterX=604.374 CenterY=339.9 CenterZ=0 NormalX=0 NormalY=0 NormalZ=1 AngleXU=0 Radius=1.5
    g15: Circle CenterX=604.374 CenterY=205.023 CenterZ=0 NormalX=0 NormalY=0 NormalZ=1 AngleXU=0 Radius=1.5
  constraints (40):
    c: Coincident(g0,g1)
    c: Coincident(g1,g2)
    c: Coincident(g2,g3)
    c: Coincident(g3,g0)
    c: Horizontal(g0)
    c: Horizontal(g2)
    c: Vertical(g1)
    c: Vertical(g3)
    c: Distance(g1,g3) = 10
    c: Distance(g0,g2) = 10
    c: Coincident(g0,g-5)
    c: Coincident(g4,g5)
    c: Coincident(g5,g6)
    c: Coincident(g6,g7)
    c: Coincident(g7,g4)
    c: Vertical(g4)
    c: Vertical(g6)
    c: Horizontal(g5)
    c: Horizontal(g7)
    c: Distance(g4,g6) = 10
    c: Distance(g5,g7) = 10
    c: Coincident(g4,g-6)
    c: Coincident(g8,g5)
    c: Coincident(g8,g1)
    c: Coincident(g9,g10)
    c: Coincident(g10,g11)
    c: Coincident(g11,g12)
    c: Coincident(g12,g9)
    c: Vertical(g9)
    c: Vertical(g11)
    c: Horizontal(g10)
    c: Horizontal(g12)
    c: Distance(g9,g11) = 10
    c: Distance(g10,g12) = 10
    c: Symmetric(g8,g8,g9)
    c: Diameter(g13) = 3
    c: Coincident(g13,g9)
    c: Diameter(g14) = 3
    c: Coincident(g14,g5)
    c: Coincident(g15,g1)
FEATURE [PartDesign::Pocket] Pocket020
  BaseFeature = -> Pocket018
  Direction = (-0.0686421,0,-0.997641)
  Length = 5
  Length2 = 5
  Profile = -> Sketch035
  ReferenceAxis = -> Sketch035 [N_Axis]
  Refine = true
  Suppressed = false
  Type = 0
FEATURE [PartDesign::SubShapeBinder] Binder010  label="Binder009"
  BindCopyOnChange = 0
  BindMode = 2
  ClaimChildren = false
  Context = -> Part [Body008.Binder009.]
  Fuse = false
  MakeFace = true
  OffsetFill = false
  OffsetIntersection = false
  OffsetJoinType = 0
  OffsetOpenResult = false
  PartialLoad = false
  Refine = true
  Relative = true
  _Version = 2
FEATURE [Sketcher::SketchObject] Sketch036
  ArcFitTolerance = 1e-06
  AttachmentSupport = -> [Binder010]
  ExternalGeometry = -> [Binder010]
  FullyConstrained = false
  MakeInternals = false
  MapMode = 5
  Placement = pos=(0,-0.1,0) rot=(0,0.707107,0.707107;3.14159rad)
  sketch-geometry (8):
    g0: LineSegment [constr] StartX=-627 StartY=-239.145 StartZ=0 EndX=-627 EndY=-203.17 EndZ=0
    g1: LineSegment [constr] StartX=-627 StartY=-203.17 StartZ=0 EndX=-655.447 EndY=-203.17 EndZ=0
    g2: LineSegment [constr] StartX=-878 StartY=-203.17 StartZ=0 EndX=-878 EndY=-225.17 EndZ=0
    g3: LineSegment [constr] StartX=-878 StartY=-203.17 StartZ=0 EndX=-789.259 EndY=-203.17 EndZ=0
    g4: LineSegment StartX=-878 StartY=-225.17 StartZ=0 EndX=-627 EndY=-225.17 EndZ=0
    g5: LineSegment StartX=-878 StartY=-183.17 StartZ=0 EndX=-627 EndY=-183.17 EndZ=0
    g6: LineSegment StartX=-627 StartY=-225.17 StartZ=0 EndX=-627 EndY=-183.17 EndZ=0
    g7: LineSegment StartX=-878 StartY=-183.17 StartZ=0 EndX=-878 EndY=-225.17 EndZ=0
  constraints (17):
    c: Coincident(g3,g2)
    c: DistanceY(g2,g2) = 22
    c: PointOnObject(g2,g-3)
    c: PointOnObject(g3,g-4)
    c: Horizontal(g3)
    c: Vertical(g2)
    c: Coincident(g4,g2)
    c: PointOnObject(g4,g0)
    c: Horizontal(g4)
    c: PointOnObject(g5,g-3)
    c: PointOnObject(g5,g-5)
    c: Horizontal(g5)
    c: Coincident(g6,g4)
    c: Coincident(g6,g5)
    c: Vertical(g6)
    c: Coincident(g7,g5)
    c: Coincident(g7,g2)
FEATURE [PartDesign::Pad] Pad011
  Direction = (0,1,-2e-16)
  Length = 350
  Length2 = 10
  Profile = -> Sketch036
  ReferenceAxis = -> Sketch036 [N_Axis]
  Refine = true
  Suppressed = false
  Type = 0
FEATURE [Sketcher::SketchObject] Sketch037
  ArcFitTolerance = 1e-06
  AttachmentSupport = -> [Pad011]
  ExternalGeometry = -> [Pad011,Binder010]
  FullyConstrained = false
  MakeInternals = false
  MapMode = 5
  Placement = pos=(878,0,0) rot=(0.57735,0.57735,0.57735;2.0944rad)
  sketch-geometry (3):
    g0: LineSegment StartX=-0.1 StartY=-183.17 StartZ=0 EndX=11.464 EndY=-183.17 EndZ=0
    g1: LineSegment StartX=-0.1 StartY=-203.2 StartZ=0 EndX=-0.1 EndY=-183.17 EndZ=0
    g2: LineSegment StartX=-0.1 StartY=-203.2 StartZ=0 EndX=11.464 EndY=-183.17 EndZ=0
  constraints (6):
    c: Coincident(g0,g-3)
    c: PointOnObject(g0,g-3)
    c: Coincident(g1,g-4)
    c: Coincident(g1,g0)
    c: Coincident(g2,g1)
    c: PointOnObject(g2,g0)
FEATURE [PartDesign::Pocket] Pocket021
  BaseFeature = -> Pad011
  Direction = (-1,0,0)
  Length = 5
  Length2 = 5
  Profile = -> Sketch037
  ReferenceAxis = -> Sketch037 [N_Axis]
  Refine = true
  Suppressed = false
  Type = 1
FEATURE [Sketcher::SketchObject] Sketch038
  ArcFitTolerance = 1e-06
  AttachmentSupport = -> [Pocket021]
  ExternalGeometry = -> [Pocket021]
  FullyConstrained = false
  MakeInternals = false
  MapMode = 5
  Placement = pos=(878,0,0) rot=(0.57735,0.57735,0.57735;2.0944rad)
  sketch-geometry (6):
    g0: LineSegment StartX=13.464 StartY=-183.17 StartZ=0 EndX=1.9 EndY=-203.2 EndZ=0
    g1: LineSegment StartX=1.9 StartY=-203.2 StartZ=0 EndX=1.9 EndY=-223.17 EndZ=0
    g2: LineSegment StartX=1.9 StartY=-223.17 StartZ=0 EndX=349.9 EndY=-223.17 EndZ=0
    g3: LineSegment [constr] StartX=1.9 StartY=-203.2 StartZ=0 EndX=-0.1 EndY=-203.2 EndZ=0
    g4: LineSegment StartX=349.9 StartY=-223.17 StartZ=0 EndX=349.9 EndY=-183.17 EndZ=0
    g5: LineSegment StartX=349.9 StartY=-183.17 StartZ=0 EndX=13.464 EndY=-183.17 EndZ=0
  constraints (15):
    c: Coincident(g1,g0)
    c: Vertical(g1)
    c: Coincident(g2,g1)
    c: Horizontal(g2)
    c: Coincident(g3,g0)
    c: Horizontal(g3)
    c: DistanceX(g3,g3) = 2
    c: DistanceX(g-3,g0) = 2
    c: DistanceY(g-4,g1) = 2
    c: Coincident(g4,g2)
    c: Coincident(g4,g-5)
    c: Vertical(g4)
    c: Coincident(g5,g4)
    c: Coincident(g5,g0)
    c: Horizontal(g5)
FEATURE [PartDesign::Pocket] Pocket022
  BaseFeature = -> Pocket021
  Direction = (-1,0,0)
  Length = 5
  Length2 = 5
  Profile = -> Sketch038
  ReferenceAxis = -> Sketch038 [N_Axis]
  Refine = true
  Suppressed = false
  Type = 1
FEATURE [Sketcher::SketchObject] Sketch039
  ArcFitTolerance = 1e-06
  AttachmentSupport = -> [Pocket022]
  ExternalGeometry = -> [Pocket022]
  FullyConstrained = false
  MakeInternals = false
  MapMode = 5
  Placement = pos=(0,0,-223.17) rot=(0,0,1;0rad)
  sketch-geometry (16):
    g0: LineSegment StartX=878 StartY=349.9 StartZ=0 EndX=876 EndY=349.9 EndZ=0
    g1: LineSegment StartX=878 StartY=1.9 StartZ=0 EndX=878 EndY=349.9 EndZ=0
    g2: LineSegment StartX=627 StartY=349.9 StartZ=0 EndX=627 EndY=1.9 EndZ=0
    g3: LineSegment StartX=627 StartY=349.9 StartZ=0 EndX=629 EndY=349.9 EndZ=0
    g4: LineSegment [constr] StartX=627 StartY=1.9 StartZ=0 EndX=629 EndY=1.9 EndZ=0
    g5: LineSegment [constr] StartX=629 StartY=1.9 StartZ=0 EndX=629 EndY=3.9 EndZ=0
    g6: LineSegment [constr] StartX=629 StartY=3.9 StartZ=0 EndX=627 EndY=3.9 EndZ=0
    g7: LineSegment [constr] StartX=627 StartY=3.9 StartZ=0 EndX=627 EndY=1.9 EndZ=0
    g8: LineSegment [constr] StartX=878 StartY=1.9 StartZ=0 EndX=878 EndY=3.9 EndZ=0
    g9: LineSegment [constr] StartX=878 StartY=3.9 StartZ=0 EndX=876 EndY=3.9 EndZ=0
    g10: LineSegment [constr] StartX=876 StartY=3.9 StartZ=0 EndX=876 EndY=1.9 EndZ=0
    g11: LineSegment [constr] StartX=876 StartY=1.9 StartZ=0 EndX=878 EndY=1.9 EndZ=0
    g12: LineSegment StartX=627 StartY=1.9 StartZ=0 EndX=629 EndY=1.9 EndZ=0
    g13: LineSegment StartX=629 StartY=1.9 StartZ=0 EndX=629 EndY=349.9 EndZ=0
    g14: LineSegment StartX=878 StartY=1.9 StartZ=0 EndX=876 EndY=1.9 EndZ=0
    g15: LineSegment StartX=876 StartY=1.9 StartZ=0 EndX=876 EndY=349.9 EndZ=0
  constraints (37):
    c: Distance(g0) = 2
    c: Coincident(g0,g-4)
    c: Horizontal(g0)
    c: Coincident(g1,g-5)
    c: Coincident(g1,g0)
    c: Coincident(g2,g-3)
    c: Distance(g3) = 2
    c: Coincident(g3,g2)
    c: Horizontal(g3)
    c: Coincident(g4,g5)
    c: Coincident(g5,g6)
    c: Coincident(g6,g7)
    c: Coincident(g7,g4)
    c: Horizontal(g4)
    c: Horizontal(g6)
    c: Vertical(g7)
    c: Distance(g4,g6) = 2
    c: Coincident(g8,g9)
    c: Coincident(g9,g10)
    c: Coincident(g10,g11)
    c: Coincident(g11,g8)
    c: Vertical(g8)
    c: Vertical(g10)
    c: Horizontal(g9)
    c: Horizontal(g11)
    c: Distance(g8,g10) = 2
    c: Coincident(g8,g1)
    c: Coincident(g12,g2)
    c: Coincident(g12,g4)
    c: Horizontal(g12)
    c: Coincident(g13,g4)
    c: Coincident(g13,g3)
    c: Vertical(g13)
    c: Coincident(g14,g1)
    c: Coincident(g14,g10)
    c: Coincident(g15,g10)
    c: Coincident(g15,g0)
FEATURE [PartDesign::Pad] Pad012
  BaseFeature = -> Pocket022
  Direction = (0,0,1)
  Length = 20
  Length2 = 10
  Profile = -> Sketch039
  ReferenceAxis = -> Sketch039 [N_Axis]
  Refine = true
  Suppressed = false
  Type = 0
FEATURE [Sketcher::SketchObject] Sketch040
  ArcFitTolerance = 1e-06
  AttachmentSupport = -> [Pad]
  ExternalGeometry = -> [Pad]
  FullyConstrained = false
  MakeInternals = false
  MapMode = 5
  Placement = pos=(0,0,0) rot=(0.57735,0.57735,-0.57735;2.0944rad)
  sketch-geometry (32):
    g0: LineSegment [constr] StartX=-140 StartY=0 StartZ=0 EndX=0 EndY=0 EndZ=0
    g1: LineSegment [constr] StartX=-140 StartY=200 StartZ=0 EndX=0 EndY=200 EndZ=0
    g2: LineSegment [constr] StartX=0 StartY=0 StartZ=0 EndX=0 EndY=10 EndZ=0
    g3: LineSegment [constr] StartX=0 StartY=10 StartZ=0 EndX=-10 EndY=10 EndZ=0
    g4: LineSegment [constr] StartX=-10 StartY=10 StartZ=0 EndX=-10 EndY=0 EndZ=0
    g5: LineSegment [constr] StartX=-10 StartY=0 StartZ=0 EndX=0 EndY=0 EndZ=0
    g6: LineSegment [constr] StartX=-140 StartY=0 StartZ=0 EndX=-130 EndY=0 EndZ=0
    g7: LineSegment [constr] StartX=-130 StartY=0 StartZ=0 EndX=-130 EndY=10 EndZ=0
    g8: LineSegment [constr] StartX=-130 StartY=10 StartZ=0 EndX=-140 EndY=10 EndZ=0
    g9: LineSegment [constr] StartX=-140 StartY=10 StartZ=0 EndX=-140 EndY=0 EndZ=0
    g10: LineSegment [constr] StartX=-140 StartY=200 StartZ=0 EndX=-140 EndY=190 EndZ=0
    g11: LineSegment [constr] StartX=-140 StartY=190 StartZ=0 EndX=-130 EndY=190 EndZ=0
    g12: LineSegment [constr] StartX=-130 StartY=190 StartZ=0 EndX=-130 EndY=200 EndZ=0
    g13: LineSegment [constr] StartX=-130 StartY=200 StartZ=0 EndX=-140 EndY=200 EndZ=0
    g14: LineSegment [constr] StartX=0 StartY=200 StartZ=0 EndX=-10 EndY=200 EndZ=0
    g15: LineSegment [constr] StartX=-10 StartY=200 StartZ=0 EndX=-10 EndY=190 EndZ=0
    g16: LineSegment [constr] StartX=-10 StartY=190 StartZ=0 EndX=0 EndY=190 EndZ=0
    g17: LineSegment [constr] StartX=0 StartY=190 StartZ=0 EndX=0 EndY=200 EndZ=0
    g18: LineSegment [constr] StartX=-70 StartY=200 StartZ=0 EndX=-80 EndY=200 EndZ=0
    g19: LineSegment [constr] StartX=-80 StartY=200 StartZ=0 EndX=-80 EndY=190 EndZ=0
    g20: LineSegment [constr] StartX=-80 StartY=190 StartZ=0 EndX=-70 EndY=190 EndZ=0
    g21: LineSegment [constr] StartX=-70 StartY=190 StartZ=0 EndX=-70 EndY=200 EndZ=0
    g22: LineSegment [constr] StartX=-70 StartY=0 StartZ=0 EndX=-70 EndY=10 EndZ=0
    g23: LineSegment [constr] StartX=-70 StartY=10 StartZ=0 EndX=-80 EndY=10 EndZ=0
    g24: LineSegment [constr] StartX=-80 StartY=10 StartZ=0 EndX=-80 EndY=0 EndZ=0
    g25: LineSegment [constr] StartX=-80 StartY=0 StartZ=0 EndX=-70 EndY=0 EndZ=0
    g26: Circle CenterX=-130 CenterY=190 CenterZ=0 NormalX=0 NormalY=0 NormalZ=1 AngleXU=0 Radius=1.5
    g27: Circle CenterX=-70 CenterY=190 CenterZ=0 NormalX=0 NormalY=0 NormalZ=1 AngleXU=0 Radius=1.5
    g28: Circle CenterX=-10 CenterY=190 CenterZ=0 NormalX=0 NormalY=0 NormalZ=1 AngleXU=0 Radius=1.5
    g29: Circle CenterX=-10 CenterY=10 CenterZ=0 NormalX=0 NormalY=0 NormalZ=1 AngleXU=0 Radius=1.5
    g30: Circle CenterX=-70 CenterY=10 CenterZ=0 NormalX=0 NormalY=0 NormalZ=1 AngleXU=0 Radius=1.5
    g31: Circle CenterX=-130 CenterY=10 CenterZ=0 NormalX=0 NormalY=0 NormalZ=1 AngleXU=0 Radius=1.5
  constraints (71):
    c: Coincident(g0,g-5)
    c: Coincident(g0,g-1)
    c: Coincident(g1,g-4)
    c: Coincident(g1,g-3)
    c: Coincident(g2,g3)
    c: Coincident(g3,g4)
    c: Coincident(g4,g5)
    c: Coincident(g5,g2)
    c: Vertical(g2)
    c: Vertical(g4)
    c: Horizontal(g3)
    c: Horizontal(g5)
    c: Distance(g2,g4) = 10
    c: Distance(g3,g5) = 10
    c: Coincident(g2,g0)
    c: Coincident(g6,g7)
    c: Coincident(g7,g8)
    c: Coincident(g8,g9)
    c: Coincident(g9,g6)
    c: Horizontal(g6)
    c: Horizontal(g8)
    c: Vertical(g7)
    c: Vertical(g9)
    c: Distance(g7,g9) = 10
    c: Distance(g6,g8) = 10
    c: Coincident(g6,g0)
    c: Coincident(g10,g11)
    c: Coincident(g11,g12)
    c: Coincident(g12,g13)
    c: Coincident(g13,g10)
    c: Vertical(g10)
    c: Vertical(g12)
    c: Horizontal(g11)
    c: Horizontal(g13)
    c: Distance(g10,g12) = 10
    c: Distance(g11,g13) = 10
    c: Coincident(g10,g1)
    c: Coincident(g14,g15)
    c: Coincident(g15,g16)
    c: Coincident(g16,g17)
    c: Coincident(g17,g14)
    c: Horizontal(g14)
    c: Horizontal(g16)
    c: Vertical(g15)
    c: Vertical(g17)
    c: Distance(g15,g17) = 10
    c: Distance(g14,g16) = 10
    c: Coincident(g14,g1)
    c: Coincident(g18,g19)
    c: Coincident(g19,g20)
    c: Coincident(g20,g21)
    c: Coincident(g21,g18)
    c: Horizontal(g18)
    c: Horizontal(g20)
    c: Vertical(g19)
    c: Vertical(g21)
    c: Distance(g19,g21) = 10
    c: Distance(g18,g20) = 10
    c: Symmetric(g1,g1,g18)
    c: Coincident(g22,g23)
    c: Coincident(g23,g24)
    c: Coincident(g24,g25)
    c: Coincident(g25,g22)
    c: Vertical(g22)
    c: Vertical(g24)
    c: Horizontal(g23)
    c: Horizontal(g25)
    c: Distance(g22,g24) = 10
    c: Distance(g23,g25) = 10
    c: Symmetric(g0,g0,g22)
    c: Coincident(g26,g11)
FEATURE [PartDesign::Pocket] Pocket
  BaseFeature = -> Pad
  Direction = (0,1,0)
  Length = 5
  Length2 = 5
  Placement = pos=(0,0,0) rot=(1,1,1;2.0944rad)
  Profile = -> Sketch040
  ReferenceAxis = -> Sketch040 [N_Axis]
  Refine = true
  Suppressed = false
  Type = 0
FEATURE [PartDesign::SubShapeBinder] Binder012
  BindCopyOnChange = 0
  BindMode = 2
  ClaimChildren = false
  Context = -> Part [Body009.Binder012.]
  Fuse = false
  MakeFace = true
  OffsetFill = false
  OffsetIntersection = false
  OffsetJoinType = 0
  OffsetOpenResult = false
  PartialLoad = false
  Refine = true
  Relative = true
  _Version = 2
FEATURE [Sketcher::SketchObject] Sketch041
  ArcFitTolerance = 1e-06
  AttachmentSupport = -> [Binder012]
  ExternalGeometry = -> [Binder012]
  FullyConstrained = true
  MakeInternals = false
  MapMode = 5
  Placement = pos=(0,-0.1,0) rot=(0,0.707107,0.707107;3.14159rad)
  sketch-geometry (8):
    g0: LineSegment StartX=278 StartY=-343.2 StartZ=0 EndX=278 EndY=107.924 EndZ=0
    g1: LineSegment StartX=278 StartY=107.924 StartZ=0 EndX=300 EndY=105.09 EndZ=0
    g2: LineSegment StartX=300 StartY=-343.2 StartZ=0 EndX=278 EndY=-343.2 EndZ=0
    g3: LineSegment StartX=300 StartY=-343.2 StartZ=0 EndX=300 EndY=-341.2 EndZ=0
    g4: LineSegment StartX=300 StartY=-341.2 StartZ=0 EndX=280 EndY=-341.2 EndZ=0
    g5: LineSegment StartX=280 StartY=-341.2 StartZ=0 EndX=280 EndY=105.924 EndZ=0
    g6: LineSegment StartX=300 StartY=105.09 StartZ=0 EndX=300 EndY=103.09 EndZ=0
    g7: LineSegment StartX=300 StartY=103.09 StartZ=0 EndX=280 EndY=105.924 EndZ=0
  constraints (22):
    c: PointOnObject(g0,g-4)
    c: Vertical(g0)
    c: Coincident(g1,g0)
    c: Coincident(g1,g-4)
    c: Distance(g2) = 22
    c: Coincident(g2,g-3)
    c: Horizontal(g2)
    c: Coincident(g0,g2)
    c: Distance(g3) = 2
    c: Coincident(g3,g2)
    c: Vertical(g3)
    c: Distance(g4) = 20
    c: Coincident(g4,g3)
    c: Horizontal(g4)
    c: Coincident(g5,g4)
    c: Vertical(g5)
    c: Coincident(g6,g1)
    c: Vertical(g6)
    c: Coincident(g7,g6)
    c: Coincident(g7,g5)
    c: DistanceY(g6,g6) = 2
    c: DistanceY(g5,g0) = 2
FEATURE [PartDesign::Pad] Pad013
  Direction = (0,1,-2e-16)
  Length = 350
  Length2 = 10
  Profile = -> Sketch041
  ReferenceAxis = -> Sketch041 [N_Axis]
  Refine = true
  Suppressed = false
  Type = 0
FEATURE [Sketcher::SketchObject] Sketch042
  ArcFitTolerance = 1e-06
  AttachmentSupport = -> [Pad013]
  ExternalGeometry = -> [Binder012,Pad013]
  FullyConstrained = true
  MakeInternals = false
  MapMode = 5
  Placement = pos=(-280,0,0) rot=(0.57735,-0.57735,-0.57735;2.0944rad)
  sketch-geometry (3):
    g0: LineSegment StartX=0.1 StartY=-203.2 StartZ=0 EndX=-179.527 EndY=107.924 EndZ=0
    g1: LineSegment StartX=0.1 StartY=107.924 StartZ=0 EndX=-179.527 EndY=107.924 EndZ=0
    g2: LineSegment StartX=0.1 StartY=107.924 StartZ=0 EndX=0.1 EndY=-203.2 EndZ=0
  constraints (7):
    c: PointOnObject(g-5,g0)
    c: Coincident(g0,g-3)
    c: Coincident(g1,g-4)
    c: Coincident(g2,g1)
    c: Coincident(g2,g0)
    c: PointOnObject(g0,g-4)
    c: Coincident(g1,g0)
FEATURE [PartDesign::Pocket] Pocket023
  BaseFeature = -> Pad013
  Direction = (1,0,0)
  Length = 5
  Length2 = 5
  Midplane = true
  Profile = -> Sketch042
  ReferenceAxis = -> Sketch042 [N_Axis]
  Refine = true
  Suppressed = false
  Type = 1
FEATURE [Sketcher::SketchObject] Sketch043
  ArcFitTolerance = 1e-06
  AttachmentSupport = -> [Pocket023]
  ExternalGeometry = -> [Pocket023]
  FullyConstrained = true
  MakeInternals = false
  MapMode = 5
  Placement = pos=(-280,0,0) rot=(0.57735,-0.57735,-0.57735;2.0944rad)
  sketch-geometry (7):
    g0: LineSegment StartX=-176.737 StartY=103.09 StartZ=0 EndX=0.1 EndY=-203.2 EndZ=0
    g1: LineSegment StartX=0.1 StartY=-203.2 StartZ=0 EndX=0.1 EndY=-341.2 EndZ=0
    g2: LineSegment StartX=0.1 StartY=-341.2 StartZ=0 EndX=-1.9 EndY=-341.2 EndZ=0
    g3: LineSegment StartX=-1.9 StartY=-341.2 StartZ=0 EndX=-1.9 EndY=-203.2 EndZ=0
    g4: LineSegment StartX=-1.9 StartY=-203.2 StartZ=0 EndX=-178.737 EndY=103.09 EndZ=0
    g5: LineSegment StartX=-178.737 StartY=103.09 StartZ=0 EndX=-176.737 EndY=103.09 EndZ=0
    g6: LineSegment [constr] StartX=-1.9 StartY=-203.2 StartZ=0 EndX=0.1 EndY=-203.2 EndZ=0
  constraints (17):
    c: Coincident(g0,g-3)
    c: Coincident(g0,g-5)
    c: Coincident(g1,g0)
    c: Coincident(g1,g-4)
    c: Distance(g2) = 2
    c: Coincident(g2,g1)
    c: Horizontal(g2)
    c: Coincident(g3,g2)
    c: Vertical(g3)
    c: Coincident(g4,g3)
    c: PointOnObject(g4,g-3)
    c: Coincident(g5,g4)
    c: Coincident(g5,g0)
    c: DistanceX(g5,g5) = 2
    c: Coincident(g6,g3)
    c: Coincident(g6,g0)
    c: Horizontal(g6)
FEATURE [PartDesign::Pad] Pad014
  BaseFeature = -> Pocket023
  Direction = (-1,0,0)
  Length = 20
  Length2 = 10
  Profile = -> Sketch043
  ReferenceAxis = -> Sketch043 [N_Axis]
  Refine = true
  Suppressed = false
  Type = 0
FEATURE [PartDesign::SubShapeBinder] Binder013
  BindCopyOnChange = 0
  BindMode = 2
  ClaimChildren = false
  Context = -> Part [Body010.Binder013.]
  Fuse = false
  MakeFace = true
  OffsetFill = false
  OffsetIntersection = false
  OffsetJoinType = 0
  OffsetOpenResult = false
  PartialLoad = false
  Refine = true
  Relative = true
  _Version = 2
FEATURE [Sketcher::SketchObject] Sketch044
  ArcFitTolerance = 1e-06
  AttachmentSupport = -> [Binder013]
  ExternalGeometry = -> [Binder013]
  FullyConstrained = true
  MakeInternals = false
  MapMode = 5
  Placement = pos=(0,-0.1,0) rot=(0,0.707107,0.707107;3.14159rad)
  sketch-geometry (9):
    g0: LineSegment StartX=100 StartY=-343.2 StartZ=0 EndX=100 EndY=-341.2 EndZ=0
    g1: LineSegment StartX=100 StartY=-341.2 StartZ=0 EndX=120 EndY=-341.2 EndZ=0
    g2: LineSegment StartX=120 StartY=-341.2 StartZ=0 EndX=120 EndY=122.94 EndZ=0
    g3: LineSegment StartX=100 StartY=-343.2 StartZ=0 EndX=122 EndY=-343.2 EndZ=0
    g4: LineSegment StartX=122 StartY=-343.2 StartZ=0 EndX=122 EndY=124.94 EndZ=0
    g5: LineSegment [constr] StartX=100 StartY=-341.2 StartZ=0 EndX=100 EndY=126.907 EndZ=0
    g6: LineSegment StartX=122 StartY=124.94 StartZ=0 EndX=100 EndY=126.907 EndZ=0
    g7: LineSegment StartX=100 StartY=126.907 StartZ=0 EndX=100 EndY=124.907 EndZ=0
    g8: LineSegment StartX=100 StartY=124.907 StartZ=0 EndX=120 EndY=122.94 EndZ=0
  constraints (25):
    c: Distance(g0) = 2
    c: Coincident(g0,g-3)
    c: Vertical(g0)
    c: Distance(g1) = 20
    c: Coincident(g1,g0)
    c: Horizontal(g1)
    c: Coincident(g2,g1)
    c: Vertical(g2)
    c: Distance(g3) = 22
    c: Coincident(g3,g0)
    c: Horizontal(g3)
    c: Coincident(g4,g3)
    c: PointOnObject(g4,g-4)
    c: Vertical(g4)
    c: Coincident(g5,g0)
    c: PointOnObject(g5,g-4)
    c: Vertical(g5)
    c: Coincident(g6,g4)
    c: Coincident(g6,g5)
    c: Distance(g7) = 2
    c: Coincident(g7,g5)
    c: PointOnObject(g7,g5)
    c: Coincident(g8,g7)
    c: Coincident(g2,g8)
    c: DistanceY(g2,g4) = 2
FEATURE [PartDesign::Pad] Pad015
  Direction = (0,1,-2e-16)
  Length = 350
  Length2 = 10
  Profile = -> Sketch044
  ReferenceAxis = -> Sketch044 [N_Axis]
  Refine = true
  Suppressed = false
  Type = 0
FEATURE [Sketcher::SketchObject] Sketch045
  ArcFitTolerance = 1e-06
  AttachmentSupport = -> [Pad015]
  ExternalGeometry = -> [Pad015]
  FullyConstrained = false
  MakeInternals = false
  MapMode = 5
  Placement = pos=(-120,0,0) rot=(0.57735,0.57735,0.57735;2.0944rad)
  sketch-geometry (3):
    g0: LineSegment StartX=-0.1 StartY=-203.2 StartZ=0 EndX=190.488 EndY=126.907 EndZ=0
    g1: LineSegment StartX=-0.1 StartY=126.907 StartZ=0 EndX=190.488 EndY=126.907 EndZ=0
    g2: LineSegment StartX=-0.1 StartY=126.907 StartZ=0 EndX=-0.1 EndY=-203.2 EndZ=0
  constraints (6):
    c: Coincident(g0,g-3)
    c: PointOnObject(g-3,g0)
    c: Coincident(g1,g-4)
    c: Coincident(g2,g1)
    c: Coincident(g2,g0)
    c: Coincident(g0,g1)
FEATURE [PartDesign::Pocket] Pocket024
  BaseFeature = -> Pad015
  Direction = (-1,0,0)
  Length = 5
  Length2 = 5
  Midplane = true
  Profile = -> Sketch045
  ReferenceAxis = -> Sketch045 [N_Axis]
  Refine = true
  Suppressed = false
  Type = 1
FEATURE [Sketcher::SketchObject] Sketch046
  ArcFitTolerance = 1e-06
  AttachmentSupport = -> [Pocket024]
  ExternalGeometry = -> [Pocket024]
  FullyConstrained = true
  MakeInternals = false
  MapMode = 5
  Placement = pos=(-120,0,0) rot=(0.57735,0.57735,0.57735;2.0944rad)
  sketch-geometry (7):
    g0: LineSegment StartX=188.197 StartY=122.94 StartZ=0 EndX=190.197 EndY=122.94 EndZ=0
    g1: LineSegment StartX=188.197 StartY=122.94 StartZ=0 EndX=-0.1 EndY=-203.2 EndZ=0
    g2: LineSegment StartX=-0.1 StartY=-203.2 StartZ=0 EndX=-0.1 EndY=-341.2 EndZ=0
    g3: LineSegment StartX=-0.1 StartY=-341.2 StartZ=0 EndX=1.9 EndY=-341.2 EndZ=0
    g4: LineSegment StartX=1.9 StartY=-341.2 StartZ=0 EndX=1.9 EndY=-203.2 EndZ=0
    g5: LineSegment StartX=1.9 StartY=-203.2 StartZ=0 EndX=190.197 EndY=122.94 EndZ=0
    g6: LineSegment [constr] StartX=-0.1 StartY=-203.2 StartZ=0 EndX=1.9 EndY=-203.2 EndZ=0
  constraints (17):
    c: Distance(g0) = 2
    c: Coincident(g0,g-7)
    c: PointOnObject(g0,g-7)
    c: Coincident(g1,g0)
    c: Coincident(g1,g-4)
    c: Coincident(g2,g1)
    c: Coincident(g2,g-4)
    c: Distance(g3) = 2
    c: Coincident(g3,g2)
    c: Horizontal(g3)
    c: Coincident(g4,g3)
    c: Vertical(g4)
    c: Coincident(g5,g4)
    c: Coincident(g5,g0)
    c: Coincident(g6,g1)
    c: Coincident(g6,g4)
    c: Horizontal(g6)
FEATURE [PartDesign::Pad] Pad016
  BaseFeature = -> Pocket024
  Direction = (1,0,0)
  Length = 20
  Length2 = 10
  Profile = -> Sketch046
  ReferenceAxis = -> Sketch046 [N_Axis]
  Refine = true
  Suppressed = false
  Type = 0
FEATURE [Sketcher::SketchObject] Sketch047
  ArcFitTolerance = 1e-06
  AttachmentSupport = -> [Pad014]
  ExternalGeometry = -> [Pad014]
  FullyConstrained = false
  MakeInternals = false
  MapMode = 5
  Placement = pos=(0,-7.51e-14,-341.2) rot=(0,0,1;0rad)
  sketch-geometry (28):
    g0: LineSegment [constr] StartX=-300 StartY=1.9 StartZ=0 EndX=-290 EndY=1.9 EndZ=0
    g1: LineSegment [constr] StartX=-290 StartY=1.9 StartZ=0 EndX=-290 EndY=11.9 EndZ=0
    g2: LineSegment [constr] StartX=-290 StartY=11.9 StartZ=0 EndX=-300 EndY=11.9 EndZ=0
    g3: LineSegment [constr] StartX=-300 StartY=11.9 StartZ=0 EndX=-300 EndY=1.9 EndZ=0
    g4: LineSegment [constr] StartX=-300 StartY=1.9 StartZ=0 EndX=-300 EndY=349.9 EndZ=0
    g5: LineSegment [constr] StartX=-300 StartY=349.9 StartZ=0 EndX=-300 EndY=339.9 EndZ=0
    g6: LineSegment [constr] StartX=-300 StartY=339.9 StartZ=0 EndX=-290 EndY=339.9 EndZ=0
    g7: LineSegment [constr] StartX=-290 StartY=339.9 StartZ=0 EndX=-290 EndY=349.9 EndZ=0
    g8: LineSegment [constr] StartX=-290 StartY=349.9 StartZ=0 EndX=-300 EndY=349.9 EndZ=0
    g9: LineSegment [constr] StartX=-300 StartY=175.9 StartZ=0 EndX=-290 EndY=175.9 EndZ=0
    g10: LineSegment [constr] StartX=-290 StartY=175.9 StartZ=0 EndX=-290 EndY=185.9 EndZ=0
    g11: LineSegment [constr] StartX=-290 StartY=185.9 StartZ=0 EndX=-300 EndY=185.9 EndZ=0
    g12: LineSegment [constr] StartX=-300 StartY=185.9 StartZ=0 EndX=-300 EndY=175.9 EndZ=0
    g13: LineSegment [constr] StartX=-290 StartY=339.9 StartZ=0 EndX=-290 EndY=185.9 EndZ=0
    g14: LineSegment [constr] StartX=-290 StartY=11.9 StartZ=0 EndX=-290 EndY=175.9 EndZ=0
    g15: LineSegment [constr] StartX=-290 StartY=93.9 StartZ=0 EndX=-290 EndY=103.9 EndZ=0
    g16: LineSegment [constr] StartX=-290 StartY=103.9 StartZ=0 EndX=-300 EndY=103.9 EndZ=0
    g17: LineSegment [constr] StartX=-300 StartY=103.9 StartZ=0 EndX=-300 EndY=93.9 EndZ=0
    g18: LineSegment [constr] StartX=-300 StartY=93.9 StartZ=0 EndX=-290 EndY=93.9 EndZ=0
    g19: LineSegment [constr] StartX=-290 StartY=262.9 StartZ=0 EndX=-290 EndY=272.9 EndZ=0
    g20: LineSegment [constr] StartX=-290 StartY=272.9 StartZ=0 EndX=-300 EndY=272.9 EndZ=0
    g21: LineSegment [constr] StartX=-300 StartY=272.9 StartZ=0 EndX=-300 EndY=262.9 EndZ=0
    g22: LineSegment [constr] StartX=-300 StartY=262.9 StartZ=0 EndX=-290 EndY=262.9 EndZ=0
    g23: Circle CenterX=-290 CenterY=339.9 CenterZ=0 NormalX=0 NormalY=0 NormalZ=1 AngleXU=0 Radius=1.5
    g24: Circle CenterX=-290 CenterY=262.9 CenterZ=0 NormalX=0 NormalY=0 NormalZ=1 AngleXU=0 Radius=1.5
    g25: Circle CenterX=-290 CenterY=175.9 CenterZ=0 NormalX=0 NormalY=0 NormalZ=1 AngleXU=0 Radius=1.5
    g26: Circle CenterX=-290 CenterY=93.9 CenterZ=0 NormalX=0 NormalY=0 NormalZ=1 AngleXU=0 Radius=1.5
    g27: Circle CenterX=-290 CenterY=11.9 CenterZ=0 NormalX=0 NormalY=0 NormalZ=1 AngleXU=0 Radius=1.5
  constraints (61):
    c: Coincident(g0,g1)
    c: Coincident(g1,g2)
    c: Coincident(g2,g3)
    c: Coincident(g3,g0)
    c: Horizontal(g0)
    c: Horizontal(g2)
    c: Vertical(g1)
    c: Vertical(g3)
    c: Distance(g1,g3) = 10
    c: Distance(g0,g2) = 10
    c: Coincident(g0,g-4)
    c: Coincident(g4,g0)
    c: Coincident(g4,g-3)
    c: Coincident(g5,g6)
    c: Coincident(g6,g7)
    c: Coincident(g7,g8)
    c: Coincident(g8,g5)
    c: Vertical(g5)
    c: Vertical(g7)
    c: Horizontal(g6)
    c: Horizontal(g8)
    c: Distance(g5,g7) = 10
    c: Distance(g6,g8) = 10
    c: Coincident(g5,g4)
    c: Coincident(g9,g10)
    c: Coincident(g10,g11)
    c: Coincident(g11,g12)
    c: Coincident(g12,g9)
    c: Horizontal(g9)
    c: Horizontal(g11)
    c: Vertical(g10)
    c: Vertical(g12)
    c: Distance(g10,g12) = 10
    c: Distance(g9,g11) = 10
    c: Symmetric(g4,g4,g9)
    c: Coincident(g13,g6)
    c: Coincident(g13,g10)
    c: Coincident(g14,g1)
    c: Coincident(g14,g9)
    c: Coincident(g15,g16)
    c: Coincident(g16,g17)
    c: Coincident(g17,g18)
    c: Coincident(g18,g15)
    c: Vertical(g15)
    c: Vertical(g17)
    c: Horizontal(g16)
    c: Horizontal(g18)
    c: Distance(g16,g18) = 10
    c: Symmetric(g14,g14,g15)
    c: PointOnObject(g16,g4)
    c: Coincident(g19,g20)
    c: Coincident(g20,g21)
    c: Coincident(g21,g22)
    c: Coincident(g22,g19)
    c: Vertical(g19)
    c: Vertical(g21)
    c: Horizontal(g20)
    c: Horizontal(g22)
    c: Distance(g20,g22) = 10
    c: Symmetric(g13,g13,g19)
    c: Coincident(g23,g6)
FEATURE [PartDesign::Pocket] Pocket025
  BaseFeature = -> Pad014
  Direction = (0,0,-1)
  Length = 5
  Length2 = 5
  Profile = -> Sketch047
  ReferenceAxis = -> Sketch047 [N_Axis]
  Refine = true
  Suppressed = false
  Type = 0
FEATURE [Sketcher::SketchObject] Sketch048
  ArcFitTolerance = 1e-06
  AttachmentSupport = -> [Pocket025]
  ExternalGeometry = -> [Pocket025]
  FullyConstrained = true
  MakeInternals = false
  MapMode = 5
  Placement = pos=(-20.2233,3.17e-14,142.731) rot=(0.997525,0,0.070317;3.14159rad)
  sketch-geometry (16):
    g0: LineSegment [constr] StartX=-282.571 StartY=-349.9 StartZ=0 EndX=-272.571 EndY=-349.9 EndZ=0
    g1: LineSegment [constr] StartX=-272.571 StartY=-349.9 StartZ=0 EndX=-272.571 EndY=-339.9 EndZ=0
    g2: LineSegment [constr] StartX=-272.571 StartY=-339.9 StartZ=0 EndX=-282.571 EndY=-339.9 EndZ=0
    g3: LineSegment [constr] StartX=-282.571 StartY=-339.9 StartZ=0 EndX=-282.571 EndY=-349.9 EndZ=0
    g4: LineSegment [constr] StartX=-282.571 StartY=-349.9 StartZ=0 EndX=-282.571 EndY=-176.737 EndZ=0
    g5: LineSegment [constr] StartX=-282.571 StartY=-176.737 StartZ=0 EndX=-282.571 EndY=-186.737 EndZ=0
    g6: LineSegment [constr] StartX=-282.571 StartY=-186.737 StartZ=0 EndX=-272.571 EndY=-186.737 EndZ=0
    g7: LineSegment [constr] StartX=-272.571 StartY=-186.737 StartZ=0 EndX=-272.571 EndY=-176.737 EndZ=0
    g8: LineSegment [constr] StartX=-272.571 StartY=-176.737 StartZ=0 EndX=-282.571 EndY=-176.737 EndZ=0
    g9: LineSegment [constr] StartX=-282.571 StartY=-263.318 StartZ=0 EndX=-272.571 EndY=-263.318 EndZ=0
    g10: LineSegment [constr] StartX=-272.571 StartY=-263.318 StartZ=0 EndX=-272.571 EndY=-253.318 EndZ=0
    g11: LineSegment [constr] StartX=-272.571 StartY=-253.318 StartZ=0 EndX=-282.571 EndY=-253.318 EndZ=0
    g12: LineSegment [constr] StartX=-282.571 StartY=-253.318 StartZ=0 EndX=-282.571 EndY=-263.318 EndZ=0
    g13: Circle CenterX=-272.571 CenterY=-263.318 CenterZ=0 NormalX=0 NormalY=0 NormalZ=1 AngleXU=0 Radius=1.5
    g14: Circle CenterX=-272.571 CenterY=-186.737 CenterZ=0 NormalX=0 NormalY=0 NormalZ=1 AngleXU=0 Radius=1.5
    g15: Circle CenterX=-272.571 CenterY=-339.9 CenterZ=0 NormalX=0 NormalY=0 NormalZ=1 AngleXU=0 Radius=1.5
  constraints (41):
    c: Coincident(g0,g1)
    c: Coincident(g1,g2)
    c: Coincident(g2,g3)
    c: Coincident(g3,g0)
    c: Horizontal(g0)
    c: Horizontal(g2)
    c: Vertical(g1)
    c: Vertical(g3)
    c: Distance(g1,g3) = 10
    c: Distance(g0,g2) = 10
    c: Coincident(g0,g-3)
    c: Coincident(g4,g0)
    c: Coincident(g4,g-5)
    c: Coincident(g5,g6)
    c: Coincident(g6,g7)
    c: Coincident(g7,g8)
    c: Coincident(g8,g5)
    c: Vertical(g5)
    c: Vertical(g7)
    c: Horizontal(g6)
    c: Horizontal(g8)
    c: Distance(g5,g7) = 10
    c: Distance(g6,g8) = 10
    c: Coincident(g5,g4)
    c: Coincident(g9,g10)
    c: Coincident(g10,g11)
    c: Coincident(g11,g12)
    c: Coincident(g12,g9)
    c: Horizontal(g9)
    c: Horizontal(g11)
    c: Vertical(g10)
    c: Vertical(g12)
    c: Distance(g10,g12) = 10
    c: Distance(g9,g11) = 10
    c: Symmetric(g4,g4,g9)
    c: Diameter(g13) = 3
    c: Coincident(g13,g9)
    c: Diameter(g14) = 3
    c: Coincident(g14,g6)
    c: Diameter(g15) = 3
    c: Coincident(g15,g1)
FEATURE [PartDesign::Pocket] Pocket026
  BaseFeature = -> Pocket025
  Direction = (-0.140287,0,0.990111)
  Length = 5
  Length2 = 5
  Profile = -> Sketch048
  ReferenceAxis = -> Sketch048 [N_Axis]
  Refine = true
  Suppressed = false
  Type = 0
FEATURE [Sketcher::SketchObject] Sketch049
  ArcFitTolerance = 1e-06
  AttachmentSupport = -> [Pocket026]
  ExternalGeometry = -> [Pocket026]
  FullyConstrained = false
  MakeInternals = false
  MapMode = 5
  Placement = pos=(3.888e-13,87.9132,-50.7567) rot=(1,0,0;1.0472rad)
  sketch-geometry (28):
    g0: LineSegment [constr] StartX=-300 StartY=-176.026 StartZ=0 EndX=-300 EndY=177.647 EndZ=0
    g1: LineSegment [constr] StartX=-300 StartY=-176.026 StartZ=0 EndX=-290 EndY=-176.026 EndZ=0
    g2: LineSegment [constr] StartX=-290 StartY=-176.026 StartZ=0 EndX=-290 EndY=-166.026 EndZ=0
    g3: LineSegment [constr] StartX=-290 StartY=-166.026 StartZ=0 EndX=-300 EndY=-166.026 EndZ=0
    g4: LineSegment [constr] StartX=-300 StartY=-166.026 StartZ=0 EndX=-300 EndY=-176.026 EndZ=0
    g5: LineSegment [constr] StartX=-300 StartY=177.647 StartZ=0 EndX=-300 EndY=167.647 EndZ=0
    g6: LineSegment [constr] StartX=-300 StartY=167.647 StartZ=0 EndX=-290 EndY=167.647 EndZ=0
    g7: LineSegment [constr] StartX=-290 StartY=167.647 StartZ=0 EndX=-290 EndY=177.647 EndZ=0
    g8: LineSegment [constr] StartX=-290 StartY=177.647 StartZ=0 EndX=-300 EndY=177.647 EndZ=0
    g9: LineSegment [constr] StartX=-300 StartY=0.810216 StartZ=0 EndX=-290 EndY=0.810216 EndZ=0
    g10: LineSegment [constr] StartX=-290 StartY=0.810216 StartZ=0 EndX=-290 EndY=10.8102 EndZ=0
    g11: LineSegment [constr] StartX=-290 StartY=10.8102 StartZ=0 EndX=-300 EndY=10.8102 EndZ=0
    g12: LineSegment [constr] StartX=-300 StartY=10.8102 StartZ=0 EndX=-300 EndY=0.810216 EndZ=0
    g13: LineSegment [constr] StartX=-290 StartY=167.647 StartZ=0 EndX=-290 EndY=10.8102 EndZ=0
    g14: LineSegment [constr] StartX=-290 StartY=0.810216 StartZ=0 EndX=-290 EndY=-166.026 EndZ=0
    g15: LineSegment [constr] StartX=-290 StartY=-82.6081 StartZ=0 EndX=-290 EndY=-72.6081 EndZ=0
    g16: LineSegment [constr] StartX=-290 StartY=-72.6081 StartZ=0 EndX=-300 EndY=-72.6081 EndZ=0
    g17: LineSegment [constr] StartX=-300 StartY=-72.6081 StartZ=0 EndX=-300 EndY=-82.6081 EndZ=0
    g18: LineSegment [constr] StartX=-300 StartY=-82.6081 StartZ=0 EndX=-290 EndY=-82.6081 EndZ=0
    g19: LineSegment [constr] StartX=-290 StartY=89.2285 StartZ=0 EndX=-290 EndY=99.2285 EndZ=0
    g20: LineSegment [constr] StartX=-290 StartY=99.2285 StartZ=0 EndX=-300 EndY=99.2285 EndZ=0
    g21: LineSegment [constr] StartX=-300 StartY=99.2285 StartZ=0 EndX=-300 EndY=89.2285 EndZ=0
    g22: LineSegment [constr] StartX=-300 StartY=89.2285 StartZ=0 EndX=-290 EndY=89.2285 EndZ=0
    g23: Circle CenterX=-290 CenterY=167.647 CenterZ=0 NormalX=0 NormalY=0 NormalZ=1 AngleXU=0 Radius=1.5
    g24: Circle CenterX=-290 CenterY=89.2285 CenterZ=0 NormalX=0 NormalY=0 NormalZ=1 AngleXU=0 Radius=1.5
    g25: Circle CenterX=-290 CenterY=0.810216 CenterZ=0 NormalX=0 NormalY=0 NormalZ=1 AngleXU=0 Radius=1.5
    g26: Circle CenterX=-290 CenterY=-82.6081 CenterZ=0 NormalX=0 NormalY=0 NormalZ=1 AngleXU=0 Radius=1.5
    g27: Circle CenterX=-290 CenterY=-166.026 CenterZ=0 NormalX=0 NormalY=0 NormalZ=1 AngleXU=0 Radius=1.5
  constraints (62):
    c: Coincident(g0,g-3)
    c: Coincident(g0,g-4)
    c: Coincident(g1,g2)
    c: Coincident(g2,g3)
    c: Coincident(g3,g4)
    c: Coincident(g4,g1)
    c: Horizontal(g1)
    c: Horizontal(g3)
    c: Vertical(g2)
    c: Vertical(g4)
    c: Distance(g2,g4) = 10
    c: Distance(g1,g3) = 10
    c: Coincident(g1,g0)
    c: Coincident(g5,g6)
    c: Coincident(g6,g7)
    c: Coincident(g7,g8)
    c: Coincident(g8,g5)
    c: Vertical(g5)
    c: Vertical(g7)
    c: Horizontal(g6)
    c: Horizontal(g8)
    c: Distance(g5,g7) = 10
    c: Distance(g6,g8) = 10
    c: Coincident(g5,g0)
    c: Coincident(g9,g10)
    c: Coincident(g10,g11)
    c: Coincident(g11,g12)
    c: Coincident(g12,g9)
    c: Horizontal(g9)
    c: Horizontal(g11)
    c: Vertical(g10)
    c: Vertical(g12)
    c: Distance(g10,g12) = 10
    c: Distance(g9,g11) = 10
    c: Symmetric(g0,g0,g9)
    c: Coincident(g13,g6)
    c: Coincident(g13,g10)
    c: Coincident(g14,g9)
    c: Coincident(g14,g2)
    c: Coincident(g15,g16)
    c: Coincident(g16,g17)
    c: Coincident(g17,g18)
    c: Coincident(g18,g15)
    c: Vertical(g15)
    c: Vertical(g17)
    c: Horizontal(g16)
    c: Horizontal(g18)
    c: Distance(g16,g18) = 10
    c: Symmetric(g14,g14,g15)
    c: PointOnObject(g16,g0)
    c: Coincident(g19,g20)
    c: Coincident(g20,g21)
    c: Coincident(g21,g22)
    c: Coincident(g22,g19)
    c: Vertical(g19)
    c: Vertical(g21)
    c: Horizontal(g20)
    c: Horizontal(g22)
    c: Distance(g20,g22) = 10
    c: Symmetric(g13,g13,g19)
    c: PointOnObject(g20,g0)
    c: Coincident(g23,g6)
FEATURE [PartDesign::Pocket] Pocket027
  BaseFeature = -> Pocket026
  Direction = (3.8e-15,0.866025,-0.5)
  Length = 5
  Length2 = 5
  Profile = -> Sketch049
  ReferenceAxis = -> Sketch049 [N_Axis]
  Refine = true
  Suppressed = false
  Type = 0
FEATURE [Sketcher::SketchObject] Sketch050
  ArcFitTolerance = 1e-06
  AttachmentSupport = -> [Pocket027]
  ExternalGeometry = -> [Binder012]
  FullyConstrained = true
  MakeInternals = false
  MapMode = 5
  Placement = pos=(0,1.9,0) rot=(0,0.707107,0.707107;3.14159rad)
  sketch-geometry (3):
    g0: Circle CenterX=290 CenterY=-213.2 CenterZ=0 NormalX=0 NormalY=0 NormalZ=1 AngleXU=0 Radius=1.5
    g1: Circle CenterX=290 CenterY=-273.2 CenterZ=0 NormalX=0 NormalY=0 NormalZ=1 AngleXU=0 Radius=1.5
    g2: Circle CenterX=290 CenterY=-333.2 CenterZ=0 NormalX=0 NormalY=0 NormalZ=1 AngleXU=0 Radius=1.5
  constraints (6):
    c: Coincident(g0,g-3)
    c: Equal(g0,g-3)
    c: Coincident(g1,g-4)
    c: Equal(g1,g-4)
    c: Coincident(g2,g-5)
    c: Equal(g2,g-5)
FEATURE [PartDesign::Pocket] Pocket028
  BaseFeature = -> Pocket027
  Direction = (0,-1,2e-16)
  Length = 5
  Length2 = 5
  Profile = -> Sketch050
  ReferenceAxis = -> Sketch050 [N_Axis]
  Refine = true
  Suppressed = false
  Type = 0
FEATURE [Sketcher::SketchObject] Sketch051
  ArcFitTolerance = 1e-06
  AttachmentSupport = -> [Pad016]
  ExternalGeometry = -> [Pad016]
  FullyConstrained = false
  MakeInternals = false
  MapMode = 5
  Placement = pos=(-3.472e-13,87.9132,-50.7567) rot=(1,0,0;1.0472rad)
  sketch-geometry (28):
    g0: LineSegment [constr] StartX=-100 StartY=-176.026 StartZ=0 EndX=-100 EndY=200.567 EndZ=0
    g1: LineSegment [constr] StartX=-100 StartY=-176.026 StartZ=0 EndX=-100 EndY=-166.026 EndZ=0
    g2: LineSegment [constr] StartX=-100 StartY=-166.026 StartZ=0 EndX=-110 EndY=-166.026 EndZ=0
    g3: LineSegment [constr] StartX=-110 StartY=-166.026 StartZ=0 EndX=-110 EndY=-176.026 EndZ=0
    g4: LineSegment [constr] StartX=-110 StartY=-176.026 StartZ=0 EndX=-100 EndY=-176.026 EndZ=0
    g5: LineSegment [constr] StartX=-100 StartY=12.2705 StartZ=0 EndX=-100 EndY=22.2705 EndZ=0
    g6: LineSegment [constr] StartX=-100 StartY=22.2705 StartZ=0 EndX=-110 EndY=22.2705 EndZ=0
    g7: LineSegment [constr] StartX=-110 StartY=22.2705 StartZ=0 EndX=-110 EndY=12.2705 EndZ=0
    g8: LineSegment [constr] StartX=-110 StartY=12.2705 StartZ=0 EndX=-100 EndY=12.2705 EndZ=0
    g9: LineSegment [constr] StartX=-100 StartY=200.567 StartZ=0 EndX=-110 EndY=200.567 EndZ=0
    g10: LineSegment [constr] StartX=-110 StartY=200.567 StartZ=0 EndX=-110 EndY=190.567 EndZ=0
    g11: LineSegment [constr] StartX=-110 StartY=190.567 StartZ=0 EndX=-100 EndY=190.567 EndZ=0
    g12: LineSegment [constr] StartX=-100 StartY=190.567 StartZ=0 EndX=-100 EndY=200.567 EndZ=0
    g13: LineSegment [constr] StartX=-110 StartY=190.567 StartZ=0 EndX=-110 EndY=22.2705 EndZ=0
    g14: LineSegment [constr] StartX=-110 StartY=12.2705 StartZ=0 EndX=-110 EndY=-166.026 EndZ=0
    g15: LineSegment [constr] StartX=-110 StartY=-76.8779 StartZ=0 EndX=-100 EndY=-76.8779 EndZ=0
    g16: LineSegment [constr] StartX=-100 StartY=-76.8779 StartZ=0 EndX=-100 EndY=-66.8779 EndZ=0
    g17: LineSegment [constr] StartX=-100 StartY=-66.8779 StartZ=0 EndX=-110 EndY=-66.8779 EndZ=0
    g18: LineSegment [constr] StartX=-110 StartY=-66.8779 StartZ=0 EndX=-110 EndY=-76.8779 EndZ=0
    g19: LineSegment [constr] StartX=-110 StartY=106.419 StartZ=0 EndX=-100 EndY=106.419 EndZ=0
    g20: LineSegment [constr] StartX=-100 StartY=106.419 StartZ=0 EndX=-100 EndY=116.419 EndZ=0
    g21: LineSegment [constr] StartX=-100 StartY=116.419 StartZ=0 EndX=-110 EndY=116.419 EndZ=0
    g22: LineSegment [constr] StartX=-110 StartY=116.419 StartZ=0 EndX=-110 EndY=106.419 EndZ=0
    g23: Circle CenterX=-110 CenterY=190.567 CenterZ=0 NormalX=0 NormalY=0 NormalZ=1 AngleXU=0 Radius=1.5
    g24: Circle CenterX=-110 CenterY=106.419 CenterZ=0 NormalX=0 NormalY=0 NormalZ=1 AngleXU=0 Radius=1.5
    g25: Circle CenterX=-110 CenterY=12.2705 CenterZ=0 NormalX=0 NormalY=0 NormalZ=1 AngleXU=0 Radius=1.5
    g26: Circle CenterX=-110 CenterY=-76.8779 CenterZ=0 NormalX=0 NormalY=0 NormalZ=1 AngleXU=0 Radius=1.5
    g27: Circle CenterX=-110 CenterY=-166.026 CenterZ=0 NormalX=0 NormalY=0 NormalZ=1 AngleXU=0 Radius=1.5
  constraints (64):
    c: Coincident(g0,g-4)
    c: Coincident(g0,g-3)
    c: Coincident(g1,g2)
    c: Coincident(g2,g3)
    c: Coincident(g3,g4)
    c: Coincident(g4,g1)
    c: Vertical(g1)
    c: Vertical(g3)
    c: Horizontal(g2)
    c: Horizontal(g4)
    c: Distance(g1,g3) = 10
    c: Distance(g2,g4) = 10
    c: Coincident(g1,g0)
    c: Coincident(g5,g6)
    c: Coincident(g6,g7)
    c: Coincident(g7,g8)
    c: Coincident(g8,g5)
    c: Vertical(g5)
    c: Vertical(g7)
    c: Horizontal(g6)
    c: Horizontal(g8)
    c: Distance(g5,g7) = 10
    c: Distance(g6,g8) = 10
    c: Symmetric(g0,g0,g5)
    c: Coincident(g9,g10)
    c: Coincident(g10,g11)
    c: Coincident(g11,g12)
    c: Coincident(g12,g9)
    c: Horizontal(g9)
    c: Horizontal(g11)
    c: Vertical(g10)
    c: Vertical(g12)
    c: Distance(g10,g12) = 10
    c: Distance(g9,g11) = 10
    c: Coincident(g9,g0)
    c: Coincident(g13,g10)
    c: Coincident(g13,g6)
    c: Coincident(g14,g7)
    c: Coincident(g14,g2)
    c: Coincident(g15,g16)
    c: Coincident(g16,g17)
    c: Coincident(g17,g18)
    c: Coincident(g18,g15)
    c: Horizontal(g15)
    c: Horizontal(g17)
    c: Vertical(g16)
    c: Vertical(g18)
    c: Distance(g15,g17) = 10
    c: Symmetric(g14,g14,g15)
    c: PointOnObject(g16,g0)
    c: Coincident(g19,g20)
    c: Coincident(g20,g21)
    c: Coincident(g21,g22)
    c: Coincident(g22,g19)
    c: Horizontal(g19)
    c: Horizontal(g21)
    c: Vertical(g20)
    c: Vertical(g22)
    c: Distance(g19,g21) = 10
    c: Symmetric(g13,g13,g19)
    c: PointOnObject(g20,g0)
    c: Coincident(g23,g10)
    c: Coincident(g25,g7)
    c: Coincident(g27,g2)
FEATURE [PartDesign::Pocket] Pocket029
  BaseFeature = -> Pad016
  Direction = (-3.4e-15,0.866025,-0.5)
  Length = 5
  Length2 = 5
  Profile = -> Sketch051
  ReferenceAxis = -> Sketch051 [N_Axis]
  Refine = true
  Suppressed = false
  Type = 0
FEATURE [Sketcher::SketchObject] Sketch052
  ArcFitTolerance = 1e-06
  AttachmentSupport = -> [Pocket029]
  ExternalGeometry = -> [Binder013]
  FullyConstrained = true
  MakeInternals = false
  MapMode = 5
  Placement = pos=(9e-16,-0.1,1e-16) rot=(1,0,0;1.5708rad)
  sketch-geometry (3):
    g0: Circle CenterX=-110 CenterY=-333.2 CenterZ=0 NormalX=0 NormalY=0 NormalZ=1 AngleXU=0 Radius=1.5
    g1: Circle CenterX=-110 CenterY=-273.2 CenterZ=0 NormalX=0 NormalY=0 NormalZ=1 AngleXU=0 Radius=1.5
    g2: Circle CenterX=-110 CenterY=-213.2 CenterZ=0 NormalX=0 NormalY=0 NormalZ=1 AngleXU=0 Radius=1.5
  constraints (6):
    c: Coincident(g0,g-5)
    c: Equal(g0,g-5)
    c: Coincident(g1,g-4)
    c: Equal(g1,g-4)
    c: Coincident(g2,g-3)
    c: Equal(g2,g-3)
FEATURE [PartDesign::Pocket] Pocket030
  BaseFeature = -> Pocket029
  Direction = (-8.6e-15,1,-2e-16)
  Length = 5
  Length2 = 5
  Profile = -> Sketch052
  ReferenceAxis = -> Sketch052 [N_Axis]
  Refine = true
  Suppressed = false
  Type = 0
FEATURE [Sketcher::SketchObject] Sketch053
  ArcFitTolerance = 1e-06
  AttachmentSupport = -> [Pocket030]
  ExternalGeometry = -> [Pocket030]
  FullyConstrained = false
  MakeInternals = false
  MapMode = 5
  Placement = pos=(0,-7.51e-14,-341.2) rot=(0,0,1;0rad)
  sketch-geometry (28):
    g0: LineSegment [constr] StartX=-100 StartY=349.9 StartZ=0 EndX=-100 EndY=1.9 EndZ=0
    g1: LineSegment [constr] StartX=-100 StartY=1.9 StartZ=0 EndX=-100 EndY=11.9 EndZ=0
    g2: LineSegment [constr] StartX=-100 StartY=11.9 StartZ=0 EndX=-110 EndY=11.9 EndZ=0
    g3: LineSegment [constr] StartX=-110 StartY=11.9 StartZ=0 EndX=-110 EndY=1.9 EndZ=0
    g4: LineSegment [constr] StartX=-110 StartY=1.9 StartZ=0 EndX=-100 EndY=1.9 EndZ=0
    g5: LineSegment [constr] StartX=-100 StartY=349.9 StartZ=0 EndX=-110 EndY=349.9 EndZ=0
    g6: LineSegment [constr] StartX=-110 StartY=349.9 StartZ=0 EndX=-110 EndY=339.9 EndZ=0
    g7: LineSegment [constr] StartX=-110 StartY=339.9 StartZ=0 EndX=-100 EndY=339.9 EndZ=0
    g8: LineSegment [constr] StartX=-100 StartY=339.9 StartZ=0 EndX=-100 EndY=349.9 EndZ=0
    g9: LineSegment [constr] StartX=-100 StartY=175.9 StartZ=0 EndX=-100 EndY=185.9 EndZ=0
    g10: LineSegment [constr] StartX=-100 StartY=185.9 StartZ=0 EndX=-110 EndY=185.9 EndZ=0
    g11: LineSegment [constr] StartX=-110 StartY=185.9 StartZ=0 EndX=-110 EndY=175.9 EndZ=0
    g12: LineSegment [constr] StartX=-110 StartY=175.9 StartZ=0 EndX=-100 EndY=175.9 EndZ=0
    g13: LineSegment [constr] StartX=-110 StartY=175.9 StartZ=0 EndX=-110 EndY=11.9 EndZ=0
    g14: LineSegment [constr] StartX=-110 StartY=93.9 StartZ=0 EndX=-100 EndY=93.9 EndZ=0
    g15: LineSegment [constr] StartX=-100 StartY=93.9 StartZ=0 EndX=-100 EndY=103.9 EndZ=0
    g16: LineSegment [constr] StartX=-100 StartY=103.9 StartZ=0 EndX=-110 EndY=103.9 EndZ=0
    g17: LineSegment [constr] StartX=-110 StartY=103.9 StartZ=0 EndX=-110 EndY=93.9 EndZ=0
    g18: Circle CenterX=-110 CenterY=339.9 CenterZ=0 NormalX=0 NormalY=0 NormalZ=1 AngleXU=0 Radius=1.5
    g19: Circle CenterX=-110 CenterY=175.9 CenterZ=0 NormalX=0 NormalY=0 NormalZ=1 AngleXU=0 Radius=1.5
    g20: Circle CenterX=-110 CenterY=93.9 CenterZ=0 NormalX=0 NormalY=0 NormalZ=1 AngleXU=0 Radius=1.5
    g21: Circle CenterX=-110 CenterY=11.9 CenterZ=0 NormalX=0 NormalY=0 NormalZ=1 AngleXU=0 Radius=1.5
    g22: LineSegment [constr] StartX=-110 StartY=339.9 StartZ=0 EndX=-110 EndY=175.9 EndZ=0
    g23: LineSegment [constr] StartX=-110 StartY=257.9 StartZ=0 EndX=-100 EndY=257.9 EndZ=0
    g24: LineSegment [constr] StartX=-100 StartY=257.9 StartZ=0 EndX=-100 EndY=267.9 EndZ=0
    g25: LineSegment [constr] StartX=-100 StartY=267.9 StartZ=0 EndX=-110 EndY=267.9 EndZ=0
    g26: LineSegment [constr] StartX=-110 StartY=267.9 StartZ=0 EndX=-110 EndY=257.9 EndZ=0
    g27: Circle CenterX=-110 CenterY=257.9 CenterZ=0 NormalX=0 NormalY=0 NormalZ=1 AngleXU=0 Radius=1.5
  constraints (61):
    c: Coincident(g0,g-4)
    c: Coincident(g0,g-3)
    c: Coincident(g1,g2)
    c: Coincident(g2,g3)
    c: Coincident(g3,g4)
    c: Coincident(g4,g1)
    c: Vertical(g1)
    c: Vertical(g3)
    c: Horizontal(g2)
    c: Horizontal(g4)
    c: Distance(g1,g3) = 10
    c: Distance(g2,g4) = 10
    c: Coincident(g1,g0)
    c: Coincident(g5,g6)
    c: Coincident(g6,g7)
    c: Coincident(g7,g8)
    c: Coincident(g8,g5)
    c: Horizontal(g5)
    c: Horizontal(g7)
    c: Vertical(g6)
    c: Vertical(g8)
    c: Distance(g6,g8) = 10
    c: Distance(g5,g7) = 10
    c: Coincident(g5,g0)
    c: Coincident(g9,g10)
    c: Coincident(g10,g11)
    c: Coincident(g11,g12)
    c: Coincident(g12,g9)
    c: Vertical(g9)
    c: Vertical(g11)
    c: Horizontal(g10)
    c: Horizontal(g12)
    c: Distance(g9,g11) = 10
    c: Distance(g10,g12) = 10
    c: Symmetric(g0,g0,g9)
    c: Coincident(g13,g11)
    c: Coincident(g13,g2)
    c: Coincident(g14,g15)
    c: Coincident(g15,g16)
    c: Coincident(g16,g17)
    c: Coincident(g17,g14)
    c: Horizontal(g14)
    c: Horizontal(g16)
    c: Vertical(g15)
    c: Vertical(g17)
    c: Distance(g14,g16) = 10
    c: Symmetric(g13,g13,g14)
    c: PointOnObject(g15,g0)
    c: Coincident(g18,g6)
    c: Coincident(g22,g6)
    c: Coincident(g22,g19)
    c: Vertical(g22)
    c: Coincident(g23,g24)
    c: Coincident(g24,g25)
    c: Coincident(g25,g26)
    c: Coincident(g26,g23)
    c: Horizontal(g23)
    c: Horizontal(g25)
    c: Vertical(g24)
    c: Vertical(g26)
    c: Distance(g24,g26) = 10
FEATURE [PartDesign::Pocket] Pocket031
  BaseFeature = -> Pocket030
  Direction = (0,0,-1)
  Length = 5
  Length2 = 5
  Profile = -> Sketch053
  ReferenceAxis = -> Sketch053 [N_Axis]
  Refine = true
  Suppressed = false
  Type = 0
FEATURE [Sketcher::SketchObject] Sketch054
  ArcFitTolerance = 1e-06
  AttachmentSupport = -> [Pocket031]
  ExternalGeometry = -> [Pocket031]
  FullyConstrained = false
  MakeInternals = false
  MapMode = 5
  Placement = pos=(-12.0542,2.98e-14,134.773) rot=(0,-1,0;0.089203rad)
  sketch-geometry (15):
    g0: LineSegment [constr] StartX=-88.2969 StartY=349.9 StartZ=0 EndX=-98.2969 EndY=349.9 EndZ=0
    g1: LineSegment [constr] StartX=-98.2969 StartY=349.9 StartZ=0 EndX=-98.2969 EndY=339.9 EndZ=0
    g2: LineSegment [constr] StartX=-98.2969 StartY=339.9 StartZ=0 EndX=-88.2969 EndY=339.9 EndZ=0
    g3: LineSegment [constr] StartX=-88.2969 StartY=339.9 StartZ=0 EndX=-88.2969 EndY=349.9 EndZ=0
    g4: LineSegment [constr] StartX=-88.2969 StartY=190.488 StartZ=0 EndX=-88.2969 EndY=200.488 EndZ=0
    g5: LineSegment [constr] StartX=-88.2969 StartY=200.488 StartZ=0 EndX=-98.2969 EndY=200.488 EndZ=0
    g6: LineSegment [constr] StartX=-98.2969 StartY=200.488 StartZ=0 EndX=-98.2969 EndY=190.488 EndZ=0
    g7: LineSegment [constr] StartX=-98.2969 StartY=190.488 StartZ=0 EndX=-88.2969 EndY=190.488 EndZ=0
    g8: LineSegment [constr] StartX=-88.2969 StartY=270.194 StartZ=0 EndX=-88.2969 EndY=280.194 EndZ=0
    g9: LineSegment [constr] StartX=-88.2969 StartY=280.194 StartZ=0 EndX=-98.2969 EndY=280.194 EndZ=0
    g10: LineSegment [constr] StartX=-98.2969 StartY=280.194 StartZ=0 EndX=-98.2969 EndY=270.194 EndZ=0
    g11: LineSegment [constr] StartX=-98.2969 StartY=270.194 StartZ=0 EndX=-88.2969 EndY=270.194 EndZ=0
    g12: Circle CenterX=-98.2969 CenterY=200.488 CenterZ=0 NormalX=0 NormalY=0 NormalZ=1 AngleXU=0 Radius=1.5
    g13: Circle CenterX=-98.2969 CenterY=270.194 CenterZ=0 NormalX=0 NormalY=0 NormalZ=1 AngleXU=0 Radius=1.5
    g14: Circle CenterX=-98.2969 CenterY=339.9 CenterZ=0 NormalX=0 NormalY=0 NormalZ=1 AngleXU=0 Radius=1.5
  constraints (30):
    c: Coincident(g0,g1)
    c: Coincident(g1,g2)
    c: Coincident(g2,g3)
    c: Coincident(g3,g0)
    c: Horizontal(g0)
    c: Horizontal(g2)
    c: Vertical(g1)
    c: Vertical(g3)
    c: Distance(g1,g3) = 10
    c: Distance(g0,g2) = 10
    c: Coincident(g4,g5)
    c: Coincident(g5,g6)
    c: Coincident(g6,g7)
    c: Coincident(g7,g4)
    c: Vertical(g4)
    c: Vertical(g6)
    c: Horizontal(g5)
    c: Horizontal(g7)
    c: Distance(g4,g6) = 10
    c: Distance(g5,g7) = 10
    c: Coincident(g8,g9)
    c: Coincident(g9,g10)
    c: Coincident(g10,g11)
    c: Coincident(g11,g8)
    c: Vertical(g8)
    c: Vertical(g10)
    c: Horizontal(g9)
    c: Horizontal(g11)
    c: Distance(g8,g10) = 10
    c: Distance(g9,g11) = 10
FEATURE [PartDesign::Pocket] Pocket032
  BaseFeature = -> Pocket031
  Direction = (0.0890849,0,-0.996024)
  Length = 5
  Length2 = 5
  Profile = -> Sketch054
  ReferenceAxis = -> Sketch054 [N_Axis]
  Refine = true
  Suppressed = false
  Type = 0
FEATURE [Sketcher::SketchObject] Sketch055
  ArcFitTolerance = 1e-06
  AttachmentSupport = -> [Pocket031]
  ExternalGeometry = -> [Pocket031]
  FullyConstrained = false
  MakeInternals = false
  MapMode = 5
  Placement = pos=(-12.0542,2.98e-14,134.773) rot=(0,-1,0;0.089203rad)
  sketch-geometry (18):
    g0: LineSegment [constr] StartX=-88.2969 StartY=349.9 StartZ=0 EndX=-88.2969 EndY=190.488 EndZ=0
    g1: LineSegment [constr] StartX=-88.2969 StartY=190.488 StartZ=0 EndX=-88.2969 EndY=200.488 EndZ=0
    g2: LineSegment [constr] StartX=-88.2969 StartY=200.488 StartZ=0 EndX=-98.2969 EndY=200.488 EndZ=0
    g3: LineSegment [constr] StartX=-98.2969 StartY=200.488 StartZ=0 EndX=-98.2969 EndY=190.488 EndZ=0
    g4: LineSegment [constr] StartX=-98.2969 StartY=190.488 StartZ=0 EndX=-88.2969 EndY=190.488 EndZ=0
    g5: LineSegment [constr] StartX=-88.2969 StartY=349.9 StartZ=0 EndX=-98.2969 EndY=349.9 EndZ=0
    g6: LineSegment [constr] StartX=-98.2969 StartY=349.9 StartZ=0 EndX=-98.2969 EndY=339.9 EndZ=0
    g7: LineSegment [constr] StartX=-98.2969 StartY=339.9 StartZ=0 EndX=-88.2969 EndY=339.9 EndZ=0
    g8: LineSegment [constr] StartX=-88.2969 StartY=339.9 StartZ=0 EndX=-88.2969 EndY=349.9 EndZ=0
    g9: LineSegment [constr] StartX=-88.2969 StartY=270.194 StartZ=0 EndX=-88.2969 EndY=280.194 EndZ=0
    g10: LineSegment [constr] StartX=-88.2969 StartY=280.194 StartZ=0 EndX=-98.2969 EndY=280.194 EndZ=0
    g11: LineSegment [constr] StartX=-98.2969 StartY=280.194 StartZ=0 EndX=-98.2969 EndY=270.194 EndZ=0
    g12: LineSegment [constr] StartX=-98.2969 StartY=270.194 StartZ=0 EndX=-88.2969 EndY=270.194 EndZ=0
    g13: LineSegment [constr] StartX=-98.2969 StartY=270.194 StartZ=0 EndX=-98.2969 EndY=339.9 EndZ=0
    g14: LineSegment [constr] StartX=-98.2969 StartY=270.194 StartZ=0 EndX=-98.2969 EndY=200.488 EndZ=0
    g15: Circle CenterX=-98.2969 CenterY=200.488 CenterZ=0 NormalX=0 NormalY=0 NormalZ=1 AngleXU=0 Radius=1.5
    g16: Circle CenterX=-98.2969 CenterY=339.9 CenterZ=0 NormalX=0 NormalY=0 NormalZ=1 AngleXU=0 Radius=1.5
    g17: Circle CenterX=-98.2969 CenterY=270.194 CenterZ=0 NormalX=0 NormalY=0 NormalZ=1 AngleXU=0 Radius=1.5
  constraints (40):
    c: Coincident(g0,g-4)
    c: Coincident(g0,g-3)
    c: Coincident(g1,g2)
    c: Coincident(g2,g3)
    c: Coincident(g3,g4)
    c: Coincident(g4,g1)
    c: Vertical(g1)
    c: Vertical(g3)
    c: Horizontal(g2)
    c: Horizontal(g4)
    c: Distance(g1,g3) = 10
    c: Distance(g2,g4) = 10
    c: Coincident(g1,g0)
    c: Coincident(g5,g6)
    c: Coincident(g6,g7)
    c: Coincident(g7,g8)
    c: Coincident(g8,g5)
    c: Horizontal(g5)
    c: Horizontal(g7)
    c: Vertical(g6)
    c: Vertical(g8)
    c: Distance(g6,g8) = 10
    c: Distance(g5,g7) = 10
    c: Coincident(g5,g0)
    c: Coincident(g9,g10)
    c: Coincident(g10,g11)
    c: Coincident(g11,g12)
    c: Coincident(g12,g9)
    c: Vertical(g9)
    c: Vertical(g11)
    c: Horizontal(g10)
    c: Horizontal(g12)
    c: Distance(g9,g11) = 10
    c: Distance(g10,g12) = 10
    c: Symmetric(g0,g0,g9)
    c: Coincident(g13,g11)
    c: Coincident(g13,g6)
    c: Coincident(g14,g11)
    c: Coincident(g14,g2)
    c: Coincident(g15,g2)
FEATURE [PartDesign::Pocket] Pocket033
  BaseFeature = -> Pocket032
  Direction = (0.0890849,0,-0.996024)
  Length = 5
  Length2 = 5
  Profile = -> Sketch055
  ReferenceAxis = -> Sketch055 [N_Axis]
  Refine = true
  Suppressed = false
  Type = 0
FEATURE [PartDesign::SubShapeBinder] Binder014
  BindCopyOnChange = 0
  BindMode = 2
  ClaimChildren = false
  Context = -> Part [Body002.Binder014.]
  Fuse = false
  MakeFace = true
  OffsetFill = false
  OffsetIntersection = false
  OffsetJoinType = 0
  OffsetOpenResult = false
  PartialLoad = false
  Refine = true
  Relative = true
  _Version = 2
FEATURE [Sketcher::SketchObject] Sketch056
  ArcFitTolerance = 1e-06
  AttachmentSupport = -> [Binder014]
  ExternalGeometry = -> [Binder014]
  FullyConstrained = true
  MakeInternals = false
  MapMode = 5
  Placement = pos=(0,3.73205,0) rot=(0,0.707107,0.707107;3.14159rad)
  sketch-geometry (10):
    g0: Circle CenterX=290 CenterY=-190 CenterZ=0 NormalX=0 NormalY=0 NormalZ=1 AngleXU=0 Radius=1.5
    g1: Circle CenterX=110 CenterY=-190 CenterZ=0 NormalX=0 NormalY=0 NormalZ=1 AngleXU=0 Radius=1.5
    g2: Circle CenterX=110 CenterY=-100.852 CenterZ=0 NormalX=0 NormalY=0 NormalZ=1 AngleXU=0 Radius=1.5
    g3: Circle CenterX=110 CenterY=-11.7032 CenterZ=0 NormalX=0 NormalY=0 NormalZ=1 AngleXU=0 Radius=1.5
    g4: Circle CenterX=110 CenterY=82.4453 CenterZ=0 NormalX=0 NormalY=0 NormalZ=1 AngleXU=0 Radius=1.5
    g5: Circle CenterX=110 CenterY=166.594 CenterZ=0 NormalX=0 NormalY=0 NormalZ=1 AngleXU=0 Radius=1.5
    g6: Circle CenterX=290 CenterY=143.673 CenterZ=0 NormalX=0 NormalY=0 NormalZ=1 AngleXU=0 Radius=1.5
    g7: Circle CenterX=290 CenterY=65.2549 CenterZ=0 NormalX=0 NormalY=0 NormalZ=1 AngleXU=0 Radius=1.5
    g8: Circle CenterX=290 CenterY=-23.1634 CenterZ=0 NormalX=0 NormalY=0 NormalZ=1 AngleXU=0 Radius=1.5
    g9: Circle CenterX=290 CenterY=-106.582 CenterZ=0 NormalX=0 NormalY=0 NormalZ=1 AngleXU=0 Radius=1.5
  constraints (20):
    c: Coincident(g0,g-10)
    c: Equal(g0,g-10)
    c: Coincident(g1,g-11)
    c: Equal(g1,g-11)
    c: Coincident(g2,g-12)
    c: Equal(g2,g-12)
    c: Coincident(g3,g-7)
    c: Equal(g3,g-7)
    c: Coincident(g4,g-4)
    c: Equal(g4,g-4)
    c: Coincident(g5,g-3)
    c: Equal(g5,g-3)
    c: Coincident(g6,g-6)
    c: Equal(g6,g-6)
    c: Coincident(g7,g-5)
    c: Equal(g7,g-5)
    c: Coincident(g8,g-8)
    c: Equal(g8,g-8)
    c: Coincident(g9,g-9)
    c: Equal(g9,g-9)
FEATURE [PartDesign::Pocket] Pocket034
  BaseFeature = -> Pad003
  Direction = (0,-1,2e-16)
  Length = 5
  Length2 = 5
  Placement = pos=(0,0,0) rot=(1,0,0;1.5708rad)
  Profile = -> Sketch056
  ReferenceAxis = -> Sketch056 [N_Axis]
  Refine = true
  Suppressed = false
  Type = 0
FEATURE [PartDesign::SubShapeBinder] Binder015
  BindCopyOnChange = 0
  BindMode = 2
  ClaimChildren = false
  Context = -> Part [Body011.Binder015.]
  Fuse = false
  MakeFace = true
  OffsetFill = false
  OffsetIntersection = false
  OffsetJoinType = 0
  OffsetOpenResult = false
  PartialLoad = false
  Refine = true
  Relative = true
  _Version = 2
FEATURE [Sketcher::SketchObject] Sketch057
  ArcFitTolerance = 1e-06
  AttachmentSupport = -> [Binder015]
  ExternalGeometry = -> [Binder015]
  FullyConstrained = true
  MakeInternals = false
  MapMode = 5
  Placement = pos=(0,-0.1,0) rot=(0,0.707107,0.707107;3.14159rad)
  sketch-geometry (5):
    g0: LineSegment StartX=122 StartY=-223.2 StartZ=0 EndX=278 EndY=-223.2 EndZ=0
    g1: LineSegment StartX=278 StartY=-223.2 StartZ=0 EndX=278 EndY=-183.2 EndZ=0
    g2: LineSegment StartX=278 StartY=-183.2 StartZ=0 EndX=122 EndY=-183.2 EndZ=0
    g3: LineSegment StartX=122 StartY=-183.2 StartZ=0 EndX=122 EndY=-223.2 EndZ=0
    g4: GeomPoint [constr] X=200 Y=-203.2 Z=0
  constraints (12):
    c: Coincident(g0,g1)
    c: Coincident(g1,g2)
    c: Coincident(g2,g3)
    c: Coincident(g3,g0)
    c: Horizontal(g0)
    c: Horizontal(g2)
    c: Vertical(g1)
    c: Vertical(g3)
    c: Symmetric(g2,g0,g4)
    c: Distance(g0,g2) = 40
    c: Symmetric(g-5,g-5,g4)
    c: PointOnObject(g1,g-4)
FEATURE [PartDesign::Pad] Pad017
  Direction = (0,1,-2e-16)
  Length = 350
  Length2 = 10
  Profile = -> Sketch057
  ReferenceAxis = -> Sketch057 [N_Axis]
  Refine = true
  Suppressed = false
  Type = 0
FEATURE [Sketcher::SketchObject] Sketch058
  ArcFitTolerance = 1e-06
  AttachmentSupport = -> [Binder015]
  ExternalGeometry = -> [Binder015,Pad017]
  FullyConstrained = false
  MakeInternals = false
  MapMode = 5
  Placement = pos=(-122,0,0) rot=(0.57735,-0.57735,-0.57735;2.0944rad)
  sketch-geometry (9):
    g0: LineSegment [constr] StartX=0.1 StartY=-203.2 StartZ=0 EndX=-1.9 EndY=-203.2 EndZ=0
    g1: LineSegment StartX=-13.447 StartY=-183.2 StartZ=0 EndX=-1.9 EndY=-203.2 EndZ=0
    g2: LineSegment StartX=-1.9 StartY=-203.2 StartZ=0 EndX=-1.9 EndY=-221.2 EndZ=0
    g3: LineSegment StartX=-1.9 StartY=-221.2 StartZ=0 EndX=-349.9 EndY=-221.2 EndZ=0
    g4: LineSegment StartX=-13.447 StartY=-183.2 StartZ=0 EndX=-349.9 EndY=-183.2 EndZ=0
    g5: LineSegment StartX=-349.9 StartY=-221.2 StartZ=0 EndX=-349.9 EndY=-183.2 EndZ=0
    g6: LineSegment StartX=0.1 StartY=-183.2 StartZ=0 EndX=-11.447 EndY=-183.2 EndZ=0
    g7: LineSegment StartX=0.1 StartY=-183.2 StartZ=0 EndX=0.1 EndY=-203.2 EndZ=0
    g8: LineSegment StartX=0.1 StartY=-203.2 StartZ=0 EndX=-11.447 EndY=-183.2 EndZ=0
  constraints (22):
    c: PointOnObject(g6,g-3)
    c: Distance(g0) = 2
    c: Coincident(g0,g-3)
    c: Horizontal(g0)
    c: Coincident(g1,g0)
    c: Coincident(g2,g0)
    c: Vertical(g2)
    c: Coincident(g3,g2)
    c: Horizontal(g3)
    c: Horizontal(g4)
    c: Coincident(g5,g3)
    c: Vertical(g5)
    c: Coincident(g5,g4)
    c: Coincident(g6,g-4)
    c: Horizontal(g6)
    c: Coincident(g7,g6)
    c: Coincident(g7,g0)
    c: Coincident(g8,g0)
    c: Coincident(g4,g1)
    c: PointOnObject(g1,g-5)
    c: DistanceX(g1,g6) = 2
    c: Coincident(g8,g6)
FEATURE [PartDesign::Pocket] Pocket035
  BaseFeature = -> Pad017
  Direction = (1,0,0)
  Length = 5
  Length2 = 5
  Profile = -> Sketch058
  ReferenceAxis = -> Sketch058 [N_Axis]
  Refine = true
  Reversed = true
  Suppressed = false
  Type = 1
FEATURE [Sketcher::SketchObject] Sketch059
  ArcFitTolerance = 1e-06
  AttachmentSupport = -> [Pocket035]
  ExternalGeometry = -> [Pocket035]
  FullyConstrained = false
  MakeInternals = false
  MapMode = 5
  Placement = pos=(0,87.9132,-50.7567) rot=(1,0,0;1.0472rad)
  sketch-geometry (16):
    g0: LineSegment [constr] StartX=-278 StartY=-176.026 StartZ=0 EndX=-268 EndY=-176.026 EndZ=0
    g1: LineSegment [constr] StartX=-268 StartY=-176.026 StartZ=0 EndX=-268 EndY=-166.026 EndZ=0
    g2: LineSegment [constr] StartX=-268 StartY=-166.026 StartZ=0 EndX=-278 EndY=-166.026 EndZ=0
    g3: LineSegment [constr] StartX=-278 StartY=-166.026 StartZ=0 EndX=-278 EndY=-176.026 EndZ=0
    g4: LineSegment [constr] StartX=-122 StartY=-176.026 StartZ=0 EndX=-122 EndY=-166.026 EndZ=0
    g5: LineSegment [constr] StartX=-122 StartY=-166.026 StartZ=0 EndX=-132 EndY=-166.026 EndZ=0
    g6: LineSegment [constr] StartX=-132 StartY=-166.026 StartZ=0 EndX=-132 EndY=-176.026 EndZ=0
    g7: LineSegment [constr] StartX=-132 StartY=-176.026 StartZ=0 EndX=-122 EndY=-176.026 EndZ=0
    g8: LineSegment [constr] StartX=-268 StartY=-176.026 StartZ=0 EndX=-132 EndY=-176.026 EndZ=0
    g9: LineSegment [constr] StartX=-200 StartY=-176.026 StartZ=0 EndX=-190 EndY=-176.026 EndZ=0
    g10: LineSegment [constr] StartX=-190 StartY=-176.026 StartZ=0 EndX=-190 EndY=-166.026 EndZ=0
    g11: LineSegment [constr] StartX=-190 StartY=-166.026 StartZ=0 EndX=-200 EndY=-166.026 EndZ=0
    g12: LineSegment [constr] StartX=-200 StartY=-166.026 StartZ=0 EndX=-200 EndY=-176.026 EndZ=0
    g13: Circle CenterX=-200 CenterY=-166.026 CenterZ=0 NormalX=0 NormalY=0 NormalZ=1 AngleXU=0 Radius=1.5
    g14: Circle CenterX=-268 CenterY=-166.026 CenterZ=0 NormalX=0 NormalY=0 NormalZ=1 AngleXU=0 Radius=1.5
    g15: Circle CenterX=-132 CenterY=-166.026 CenterZ=0 NormalX=0 NormalY=0 NormalZ=1 AngleXU=0 Radius=1.5
  constraints (35):
    c: Coincident(g0,g1)
    c: Coincident(g1,g2)
    c: Coincident(g2,g3)
    c: Coincident(g3,g0)
    c: Horizontal(g0)
    c: Horizontal(g2)
    c: Vertical(g1)
    c: Vertical(g3)
    c: Distance(g1,g3) = 10
    c: Distance(g0,g2) = 10
    c: Coincident(g0,g-3)
    c: Coincident(g4,g5)
    c: Coincident(g5,g6)
    c: Coincident(g6,g7)
    c: Coincident(g7,g4)
    c: Vertical(g4)
    c: Vertical(g6)
    c: Horizontal(g5)
    c: Horizontal(g7)
    c: Distance(g4,g6) = 10
    c: Distance(g5,g7) = 10
    c: Coincident(g4,g-4)
    c: Coincident(g8,g0)
    c: Coincident(g8,g6)
    c: Coincident(g9,g10)
    c: Coincident(g10,g11)
    c: Coincident(g11,g12)
    c: Coincident(g12,g9)
    c: Horizontal(g9)
    c: Horizontal(g11)
    c: Vertical(g10)
    c: Vertical(g12)
    c: Distance(g10,g12) = 10
    c: Distance(g9,g11) = 10
    c: Symmetric(g8,g8,g9)
FEATURE [PartDesign::Pocket] Pocket036
  BaseFeature = -> Pocket035
  Direction = (0,0.866025,-0.5)
  Length = 5
  Length2 = 5
  Profile = -> Sketch059
  ReferenceAxis = -> Sketch059 [N_Axis]
  Refine = true
  Suppressed = false
  Type = 0
FEATURE [Sketcher::SketchObject] Sketch060
  ArcFitTolerance = 1e-06
  AttachmentSupport = -> [Pocket036]
  ExternalGeometry = -> [Pocket036]
  FullyConstrained = false
  MakeInternals = false
  MapMode = 5
  Placement = pos=(0,-0.1,0) rot=(1,0,0;1.5708rad)
  sketch-geometry (16):
    g0: LineSegment [constr] StartX=-122 StartY=-223.2 StartZ=0 EndX=-122 EndY=-213.2 EndZ=0
    g1: LineSegment [constr] StartX=-122 StartY=-213.2 StartZ=0 EndX=-132 EndY=-213.2 EndZ=0
    g2: LineSegment [constr] StartX=-132 StartY=-213.2 StartZ=0 EndX=-132 EndY=-223.2 EndZ=0
    g3: LineSegment [constr] StartX=-132 StartY=-223.2 StartZ=0 EndX=-122 EndY=-223.2 EndZ=0
    g4: LineSegment [constr] StartX=-278 StartY=-223.2 StartZ=0 EndX=-268 EndY=-223.2 EndZ=0
    g5: LineSegment [constr] StartX=-268 StartY=-223.2 StartZ=0 EndX=-268 EndY=-213.2 EndZ=0
    g6: LineSegment [constr] StartX=-268 StartY=-213.2 StartZ=0 EndX=-278 EndY=-213.2 EndZ=0
    g7: LineSegment [constr] StartX=-278 StartY=-213.2 StartZ=0 EndX=-278 EndY=-223.2 EndZ=0
    g8: LineSegment [constr] StartX=-268 StartY=-223.2 StartZ=0 EndX=-132 EndY=-223.2 EndZ=0
    g9: LineSegment [constr] StartX=-200 StartY=-223.2 StartZ=0 EndX=-190 EndY=-223.2 EndZ=0
    g10: LineSegment [constr] StartX=-190 StartY=-223.2 StartZ=0 EndX=-190 EndY=-213.2 EndZ=0
    g11: LineSegment [constr] StartX=-190 StartY=-213.2 StartZ=0 EndX=-200 EndY=-213.2 EndZ=0
    g12: LineSegment [constr] StartX=-200 StartY=-213.2 StartZ=0 EndX=-200 EndY=-223.2 EndZ=0
    g13: Circle CenterX=-200 CenterY=-213.2 CenterZ=0 NormalX=0 NormalY=0 NormalZ=1 AngleXU=0 Radius=1.5
    g14: Circle CenterX=-268 CenterY=-213.2 CenterZ=0 NormalX=0 NormalY=0 NormalZ=1 AngleXU=0 Radius=1.5
    g15: Circle CenterX=-132 CenterY=-213.2 CenterZ=0 NormalX=0 NormalY=0 NormalZ=1 AngleXU=0 Radius=1.5
  constraints (36):
    c: Coincident(g0,g1)
    c: Coincident(g1,g2)
    c: Coincident(g2,g3)
    c: Coincident(g3,g0)
    c: Vertical(g0)
    c: Vertical(g2)
    c: Horizontal(g1)
    c: Horizontal(g3)
    c: Distance(g0,g2) = 10
    c: Distance(g1,g3) = 10
    c: Coincident(g0,g-4)
    c: Coincident(g4,g5)
    c: Coincident(g5,g6)
    c: Coincident(g6,g7)
    c: Coincident(g7,g4)
    c: Horizontal(g4)
    c: Horizontal(g6)
    c: Vertical(g5)
    c: Vertical(g7)
    c: Distance(g5,g7) = 10
    c: Distance(g4,g6) = 10
    c: Coincident(g4,g-3)
    c: Coincident(g8,g4)
    c: Coincident(g8,g2)
    c: Coincident(g9,g10)
    c: Coincident(g10,g11)
    c: Coincident(g11,g12)
    c: Coincident(g12,g9)
    c: Horizontal(g9)
    c: Horizontal(g11)
    c: Vertical(g10)
    c: Vertical(g12)
    c: Distance(g10,g12) = 10
    c: Distance(g9,g11) = 10
    c: Symmetric(g8,g8,g9)
    c: Coincident(g13,g11)
FEATURE [PartDesign::Pocket] Pocket037
  BaseFeature = -> Pocket036
  Direction = (0,1,-2e-16)
  Length = 5
  Length2 = 5
  Profile = -> Sketch060
  ReferenceAxis = -> Sketch060 [N_Axis]
  Refine = true
  Suppressed = false
  Type = 0
FEATURE [Sketcher::SketchObject] Sketch061
  ArcFitTolerance = 1e-06
  AttachmentSupport = -> [Pocket037]
  ExternalGeometry = -> [Pocket037]
  FullyConstrained = true
  MakeInternals = false
  MapMode = 5
  Placement = pos=(0,1.9,0) rot=(0,0.707107,0.707107;3.14159rad)
  sketch-geometry (8):
    g0: LineSegment StartX=278 StartY=-203.2 StartZ=0 EndX=278 EndY=-221.2 EndZ=0
    g1: LineSegment StartX=278 StartY=-221.2 StartZ=0 EndX=276 EndY=-221.2 EndZ=0
    g2: LineSegment StartX=276 StartY=-221.2 StartZ=0 EndX=276 EndY=-203.2 EndZ=0
    g3: LineSegment StartX=278 StartY=-203.2 StartZ=0 EndX=276 EndY=-203.2 EndZ=0
    g4: LineSegment StartX=122 StartY=-203.2 StartZ=0 EndX=122 EndY=-221.2 EndZ=0
    g5: LineSegment StartX=122 StartY=-221.2 StartZ=0 EndX=124 EndY=-221.2 EndZ=0
    g6: LineSegment StartX=124 StartY=-221.2 StartZ=0 EndX=124 EndY=-203.2 EndZ=0
    g7: LineSegment StartX=124 StartY=-203.2 StartZ=0 EndX=122 EndY=-203.2 EndZ=0
  constraints (20):
    c: Coincident(g0,g-4)
    c: Coincident(g0,g-4)
    c: Distance(g1) = 2
    c: Coincident(g1,g0)
    c: Horizontal(g1)
    c: Coincident(g2,g1)
    c: Vertical(g2)
    c: Coincident(g3,g0)
    c: Horizontal(g3)
    c: Coincident(g3,g2)
    c: Coincident(g4,g-3)
    c: Coincident(g4,g-3)
    c: Distance(g5) = 2
    c: Horizontal(g5)
    c: Coincident(g6,g5)
    c: Vertical(g6)
    c: Coincident(g7,g6)
    c: Horizontal(g7)
    c: Coincident(g7,g4)
    c: Coincident(g5,g4)
FEATURE [PartDesign::Pad] Pad018
  BaseFeature = -> Pocket037
  Direction = (0,1,-2e-16)
  Length = 348
  Length2 = 10
  Profile = -> Sketch061
  ReferenceAxis = -> Sketch061 [N_Axis]
  Refine = true
  Suppressed = false
  Type = 0
FEATURE [Sketcher::SketchObject] Sketch062
  ArcFitTolerance = 1e-06
  AttachmentSupport = -> [Pad018]
  ExternalGeometry = -> [Pad018]
  FullyConstrained = false
  MakeInternals = false
  MapMode = 5
  Placement = pos=(-122,0,8.467e-13) rot=(0.57735,0.57735,0.57735;2.0944rad)
  sketch-geometry (28):
    g0: LineSegment [constr] StartX=349.9 StartY=-203.2 StartZ=0 EndX=339.9 EndY=-203.2 EndZ=0
    g1: LineSegment [constr] StartX=339.9 StartY=-203.2 StartZ=0 EndX=339.9 EndY=-213.2 EndZ=0
    g2: LineSegment [constr] StartX=339.9 StartY=-213.2 StartZ=0 EndX=349.9 EndY=-213.2 EndZ=0
    g3: LineSegment [constr] StartX=349.9 StartY=-213.2 StartZ=0 EndX=349.9 EndY=-203.2 EndZ=0
    g4: LineSegment [constr] StartX=1.9 StartY=-203.2 StartZ=0 EndX=1.9 EndY=-213.2 EndZ=0
    g5: LineSegment [constr] StartX=1.9 StartY=-213.2 StartZ=0 EndX=11.9 EndY=-213.2 EndZ=0
    g6: LineSegment [constr] StartX=11.9 StartY=-213.2 StartZ=0 EndX=11.9 EndY=-203.2 EndZ=0
    g7: LineSegment [constr] StartX=11.9 StartY=-203.2 StartZ=0 EndX=1.9 EndY=-203.2 EndZ=0
    g8: LineSegment [constr] StartX=11.9 StartY=-213.2 StartZ=0 EndX=339.9 EndY=-213.2 EndZ=0
    g9: LineSegment [constr] StartX=175.9 StartY=-213.2 StartZ=0 EndX=185.9 EndY=-213.2 EndZ=0
    g10: LineSegment [constr] StartX=185.9 StartY=-213.2 StartZ=0 EndX=185.9 EndY=-203.2 EndZ=0
    g11: LineSegment [constr] StartX=185.9 StartY=-203.2 StartZ=0 EndX=175.9 EndY=-203.2 EndZ=0
    g12: LineSegment [constr] StartX=175.9 StartY=-203.2 StartZ=0 EndX=175.9 EndY=-213.2 EndZ=0
    g13: LineSegment [constr] StartX=175.9 StartY=-203.2 StartZ=0 EndX=339.9 EndY=-203.2 EndZ=0
    g14: LineSegment [constr] StartX=175.9 StartY=-203.2 StartZ=0 EndX=11.9 EndY=-203.2 EndZ=0
    g15: LineSegment [constr] StartX=257.9 StartY=-203.2 StartZ=0 EndX=257.9 EndY=-213.2 EndZ=0
    g16: LineSegment [constr] StartX=257.9 StartY=-213.2 StartZ=0 EndX=267.9 EndY=-213.2 EndZ=0
    g17: LineSegment [constr] StartX=267.9 StartY=-213.2 StartZ=0 EndX=267.9 EndY=-203.2 EndZ=0
    g18: LineSegment [constr] StartX=267.9 StartY=-203.2 StartZ=0 EndX=257.9 EndY=-203.2 EndZ=0
    g19: LineSegment [constr] StartX=93.9 StartY=-203.2 StartZ=0 EndX=83.9 EndY=-203.2 EndZ=0
    g20: LineSegment [constr] StartX=83.9 StartY=-203.2 StartZ=0 EndX=83.9 EndY=-213.2 EndZ=0
    g21: LineSegment [constr] StartX=83.9 StartY=-213.2 StartZ=0 EndX=93.9 EndY=-213.2 EndZ=0
    g22: LineSegment [constr] StartX=93.9 StartY=-213.2 StartZ=0 EndX=93.9 EndY=-203.2 EndZ=0
    g23: Circle CenterX=257.9 CenterY=-213.2 CenterZ=0 NormalX=0 NormalY=0 NormalZ=1 AngleXU=0 Radius=1.5
    g24: Circle CenterX=339.9 CenterY=-213.2 CenterZ=0 NormalX=0 NormalY=0 NormalZ=1 AngleXU=0 Radius=1.5
    g25: Circle CenterX=175.9 CenterY=-213.2 CenterZ=0 NormalX=0 NormalY=0 NormalZ=1 AngleXU=0 Radius=1.5
    g26: Circle CenterX=93.9 CenterY=-213.2 CenterZ=0 NormalX=0 NormalY=0 NormalZ=1 AngleXU=0 Radius=1.5
    g27: Circle CenterX=11.9 CenterY=-213.2 CenterZ=0 NormalX=0 NormalY=0 NormalZ=1 AngleXU=0 Radius=1.5
  constraints (60):
    c: Coincident(g0,g1)
    c: Coincident(g1,g2)
    c: Coincident(g2,g3)
    c: Coincident(g3,g0)
    c: Horizontal(g0)
    c: Horizontal(g2)
    c: Vertical(g1)
    c: Vertical(g3)
    c: Distance(g1,g3) = 10
    c: Distance(g0,g2) = 10
    c: Coincident(g0,g-4)
    c: Coincident(g4,g5)
    c: Coincident(g5,g6)
    c: Coincident(g6,g7)
    c: Coincident(g7,g4)
    c: Vertical(g4)
    c: Vertical(g6)
    c: Horizontal(g5)
    c: Horizontal(g7)
    c: Distance(g4,g6) = 10
    c: Distance(g5,g7) = 10
    c: Coincident(g4,g-3)
    c: Coincident(g8,g5)
    c: Coincident(g8,g1)
    c: Coincident(g9,g10)
    c: Coincident(g10,g11)
    c: Coincident(g11,g12)
    c: Coincident(g12,g9)
    c: Horizontal(g9)
    c: Horizontal(g11)
    c: Vertical(g10)
    c: Vertical(g12)
    c: Distance(g10,g12) = 10
    c: Distance(g9,g11) = 10
    c: Symmetric(g8,g8,g9)
    c: Coincident(g13,g11)
    c: Coincident(g13,g0)
    c: Coincident(g14,g11)
    c: Coincident(g14,g6)
    c: Coincident(g15,g16)
    c: Coincident(g16,g17)
    c: Coincident(g17,g18)
    c: Coincident(g18,g15)
    c: Vertical(g15)
    c: Vertical(g17)
    c: Horizontal(g16)
    c: Horizontal(g18)
    c: Distance(g15,g17) = 10
    c: Symmetric(g13,g13,g15)
    c: PointOnObject(g16,g8)
    c: Coincident(g19,g20)
    c: Coincident(g20,g21)
    c: Coincident(g21,g22)
    c: Coincident(g22,g19)
    c: Horizontal(g19)
    c: Horizontal(g21)
    c: Vertical(g20)
    c: Vertical(g22)
    c: Distance(g20,g22) = 10
    c: Symmetric(g14,g14,g19)
FEATURE [PartDesign::Pocket] Pocket038
  BaseFeature = -> Pad018
  Direction = (-1,-1e-16,6.8e-15)
  Length = 5
  Length2 = 5
  Profile = -> Sketch062
  ReferenceAxis = -> Sketch062 [N_Axis]
  Refine = true
  Suppressed = false
  Type = 1
FEATURE [PartDesign::Body] Body011  label="SpHr2"
  AllowCompound = false
  Group = -> [Binder015,Sketch057,Pad017,Sketch058,Pocket035,Sketch059,Pocket036,Sketch060,Pocket037,Sketch061,Pad018,Sketch062,Pocket038]
  Origin = -> Origin012
  Tip = -> Pocket038
FEATURE [PartDesign::SubShapeBinder] Binder016
  BindCopyOnChange = 0
  BindMode = 0
  ClaimChildren = false
  Context = -> Part [Body002.Binder016.]
  Fuse = false
  MakeFace = true
  OffsetFill = false
  OffsetIntersection = false
  OffsetJoinType = 0
  OffsetOpenResult = false
  PartialLoad = false
  Refine = true
  Relative = true
  Support = -> [Body011[Pocket038.Face21,Pocket038.Face5]]
  _Version = 2
FEATURE [Sketcher::SketchObject] Sketch063
  ArcFitTolerance = 1e-06
  AttachmentSupport = -> [Pocket034]
  ExternalGeometry = -> [Binder016]
  FullyConstrained = true
  MakeInternals = false
  MapMode = 5
  Placement = pos=(0,2,0) rot=(-1,0,0;1.5708rad)
  sketch-geometry (3):
    g0: Circle CenterX=-132 CenterY=190 CenterZ=0 NormalX=0 NormalY=0 NormalZ=1 AngleXU=0 Radius=1.5
    g1: Circle CenterX=-200 CenterY=190 CenterZ=0 NormalX=0 NormalY=0 NormalZ=1 AngleXU=0 Radius=1.5
    g2: Circle CenterX=-268 CenterY=190 CenterZ=0 NormalX=0 NormalY=0 NormalZ=1 AngleXU=0 Radius=1.5
  constraints (6):
    c: Coincident(g0,g-5)
    c: Equal(g0,g-5)
    c: Coincident(g1,g-4)
    c: Equal(g1,g-4)
    c: Coincident(g2,g-3)
    c: Equal(g2,g-3)
FEATURE [PartDesign::Pocket] Pocket039
  BaseFeature = -> Pocket034
  Direction = (0,-1,-2e-16)
  Length = 5
  Length2 = 5
  Placement = pos=(0,0,0) rot=(1,0,0;1.5708rad)
  Profile = -> Sketch063
  ReferenceAxis = -> Sketch063 [N_Axis]
  Refine = true
  Suppressed = false
  Type = 0
FEATURE [PartDesign::Body] Body002  label="MainPt1"
  AllowCompound = false
  Group = -> [Sketch009,Pad003,Binder014,Sketch056,Pocket034,Binder016,Sketch063,Pocket039]
  Origin = -> Origin003
  Placement = pos=(0,98.1679,-28.9949) rot=(1,0,0;5.75959rad)
  Tip = -> Pocket039
FEATURE [PartDesign::SubShapeBinder] Binder017
  BindCopyOnChange = 0
  BindMode = 0
  ClaimChildren = false
  Context = -> Part [Body.Binder017.]
  Fuse = false
  MakeFace = true
  OffsetFill = false
  OffsetIntersection = false
  OffsetJoinType = 0
  OffsetOpenResult = false
  PartialLoad = false
  Refine = true
  Relative = true
  Support = -> [Body011[Pocket038.Face5]]
  _Version = 2
FEATURE [Sketcher::SketchObject] Sketch064
  ArcFitTolerance = 1e-06
  AttachmentSupport = -> [Pocket]
  ExternalGeometry = -> [Binder017]
  FullyConstrained = true
  MakeInternals = false
  MapMode = 5
  Placement = pos=(0,0,0) rot=(0.57735,0.57735,-0.57735;2.0944rad)
  sketch-geometry (3):
    g0: Circle CenterX=-130 CenterY=32 CenterZ=0 NormalX=0 NormalY=0 NormalZ=1 AngleXU=0 Radius=1.5
    g1: Circle CenterX=-130 CenterY=100 CenterZ=0 NormalX=0 NormalY=0 NormalZ=1 AngleXU=0 Radius=1.5
    g2: Circle CenterX=-130 CenterY=168 CenterZ=0 NormalX=0 NormalY=0 NormalZ=1 AngleXU=0 Radius=1.5
  constraints (6):
    c: Coincident(g0,g-5)
    c: Equal(g0,g-5)
    c: Coincident(g1,g-4)
    c: Equal(g1,g-4)
    c: Coincident(g2,g-3)
    c: Equal(g2,g-3)
FEATURE [PartDesign::Pocket] Pocket040
  BaseFeature = -> Pocket
  Direction = (0,1,0)
  Length = 5
  Length2 = 5
  Placement = pos=(0,0,0) rot=(1,1,1;2.0944rad)
  Profile = -> Sketch064
  ReferenceAxis = -> Sketch064 [N_Axis]
  Refine = true
  Suppressed = false
  Type = 0
FEATURE [PartDesign::Body] Body  label="PzDelantera2"
  AllowCompound = false
  Group = -> [Sketch,Pad,Sketch040,Pocket,Binder017,Sketch064,Pocket040]
  Origin = -> Origin001
  Placement = pos=(-300,-2.1,-343.2) rot=(0,0,1;0rad)
  Tip = -> Pocket040
FEATURE [PartDesign::SubShapeBinder] Binder018
  BindCopyOnChange = 0
  BindMode = 0
  ClaimChildren = false
  Context = -> Part [Body010.Binder018.]
  Fuse = false
  MakeFace = true
  OffsetFill = false
  OffsetIntersection = false
  OffsetJoinType = 0
  OffsetOpenResult = false
  PartialLoad = false
  Refine = true
  Relative = true
  Support = -> [Body011[Pocket038.Face2]]
  _Version = 2
FEATURE [Sketcher::SketchObject] Sketch065
  ArcFitTolerance = 1e-06
  AttachmentSupport = -> [Binder018]
  ExternalGeometry = -> [Binder018]
  FullyConstrained = true
  MakeInternals = false
  MapMode = 5
  Placement = pos=(-124,0,0) rot=(0.57735,-0.57735,-0.57735;2.0944rad)
  sketch-geometry (5):
    g0: Circle CenterX=-339.9 CenterY=-213.2 CenterZ=0 NormalX=0 NormalY=0 NormalZ=1 AngleXU=0 Radius=1.5
    g1: Circle CenterX=-257.9 CenterY=-213.2 CenterZ=0 NormalX=0 NormalY=0 NormalZ=1 AngleXU=0 Radius=1.5
    g2: Circle CenterX=-175.9 CenterY=-213.2 CenterZ=0 NormalX=0 NormalY=0 NormalZ=1 AngleXU=0 Radius=1.5
    g3: Circle CenterX=-93.9 CenterY=-213.2 CenterZ=0 NormalX=0 NormalY=0 NormalZ=1 AngleXU=0 Radius=1.5
    g4: Circle CenterX=-11.9 CenterY=-213.2 CenterZ=0 NormalX=0 NormalY=0 NormalZ=1 AngleXU=0 Radius=1.5
  constraints (10):
    c: Coincident(g0,g-3)
    c: Equal(g0,g-3)
    c: Coincident(g1,g-4)
    c: Equal(g1,g-4)
    c: Coincident(g2,g-5)
    c: Equal(g2,g-5)
    c: Coincident(g3,g-6)
    c: Equal(g3,g-6)
    c: Coincident(g4,g-7)
    c: Equal(g4,g-7)
FEATURE [PartDesign::Pocket] Pocket041
  BaseFeature = -> Pocket033
  Direction = (1,0,0)
  Length = 5
  Length2 = 5
  Profile = -> Sketch065
  ReferenceAxis = -> Sketch065 [N_Axis]
  Refine = true
  Suppressed = false
  Type = 1
FEATURE [PartDesign::Body] Body010  label="SpVr4"
  AllowCompound = false
  Group = -> [Binder013,Sketch044,Pad015,Sketch045,Pocket024,Sketch046,Pad016,Sketch051,Pocket029,Sketch052,Pocket030,Sketch053,Pocket031,Sketch054,Pocket032,Sketch055,Pocket033,Binder018,Sketch065,Pocket041]
  Origin = -> Origin011
  Tip = -> Pocket041
FEATURE [PartDesign::SubShapeBinder] Binder019
  BindCopyOnChange = 0
  BindMode = 0
  ClaimChildren = false
  Context = -> Part [Body009.Binder019.]
  Fuse = false
  MakeFace = true
  OffsetFill = false
  OffsetIntersection = false
  OffsetJoinType = 0
  OffsetOpenResult = false
  PartialLoad = false
  Refine = true
  Relative = true
  Support = -> [Body011[Pocket038.Face4]]
  _Version = 2
FEATURE [Sketcher::SketchObject] Sketch066
  ArcFitTolerance = 1e-06
  AttachmentSupport = -> [Binder019]
  ExternalGeometry = -> [Binder019]
  FullyConstrained = true
  MakeInternals = false
  MapMode = 5
  Placement = pos=(-276,0,0) rot=(0.57735,0.57735,0.57735;2.0944rad)
  sketch-geometry (5):
    g0: Circle CenterX=339.9 CenterY=-213.2 CenterZ=0 NormalX=0 NormalY=0 NormalZ=1 AngleXU=0 Radius=1.5
    g1: Circle CenterX=257.9 CenterY=-213.2 CenterZ=0 NormalX=0 NormalY=0 NormalZ=1 AngleXU=0 Radius=1.5
    g2: Circle CenterX=175.9 CenterY=-213.2 CenterZ=0 NormalX=0 NormalY=0 NormalZ=1 AngleXU=0 Radius=1.5
    g3: Circle CenterX=93.9 CenterY=-213.2 CenterZ=0 NormalX=0 NormalY=0 NormalZ=1 AngleXU=0 Radius=1.5
    g4: Circle CenterX=11.9 CenterY=-213.2 CenterZ=0 NormalX=0 NormalY=0 NormalZ=1 AngleXU=0 Radius=1.5
  constraints (10):
    c: Coincident(g0,g-7)
    c: Equal(g0,g-7)
    c: Coincident(g1,g-6)
    c: Equal(g1,g-6)
    c: Coincident(g2,g-5)
    c: Equal(g2,g-5)
    c: Coincident(g3,g-4)
    c: Equal(g3,g-4)
    c: Coincident(g4,g-3)
    c: Equal(g4,g-3)
FEATURE [PartDesign::Pocket] Pocket042
  BaseFeature = -> Pocket028
  Direction = (-1,0,0)
  Length = 5
  Length2 = 5
  Profile = -> Sketch066
  ReferenceAxis = -> Sketch066 [N_Axis]
  Refine = true
  Suppressed = false
  Type = 0
FEATURE [PartDesign::Body] Body009  label="SpVr3"
  AllowCompound = false
  Group = -> [Binder012,Sketch041,Pad013,Sketch042,Pocket023,Sketch043,Pad014,Sketch047,Pocket025,Sketch048,Pocket026,Sketch049,Pocket027,Sketch050,Pocket028,Binder019,Sketch066,Pocket042]
  Origin = -> Origin010
  Tip = -> Pocket042
FEATURE [App::DocumentObjectGroup] Group001  label="LEFT"
  Group = -> [Body,Body002,Body005,Body009,Body010,Body011]
FEATURE [Sketcher::SketchObject] Sketch067
  ArcFitTolerance = 1e-06
  AttachmentSupport = -> [Pad012]
  ExternalGeometry = -> [Pad012]
  FullyConstrained = false
  MakeInternals = false
  MapMode = 5
  Placement = pos=(0,87.9131,-50.7566) rot=(1,0,0;1.0472rad)
  sketch-geometry (28):
    g0: LineSegment [constr] StartX=627 StartY=-176.026 StartZ=0 EndX=637 EndY=-176.026 EndZ=0
    g1: LineSegment [constr] StartX=637 StartY=-176.026 StartZ=0 EndX=637 EndY=-166.026 EndZ=0
    g2: LineSegment [constr] StartX=637 StartY=-166.026 StartZ=0 EndX=627 EndY=-166.026 EndZ=0
    g3: LineSegment [constr] StartX=627 StartY=-166.026 StartZ=0 EndX=627 EndY=-176.026 EndZ=0
    g4: LineSegment [constr] StartX=878 StartY=-176.026 StartZ=0 EndX=878 EndY=-166.026 EndZ=0
    g5: LineSegment [constr] StartX=878 StartY=-166.026 StartZ=0 EndX=868 EndY=-166.026 EndZ=0
    g6: LineSegment [constr] StartX=868 StartY=-166.026 StartZ=0 EndX=868 EndY=-176.026 EndZ=0
    g7: LineSegment [constr] StartX=868 StartY=-176.026 StartZ=0 EndX=878 EndY=-176.026 EndZ=0
    g8: LineSegment [constr] StartX=868 StartY=-176.026 StartZ=0 EndX=637 EndY=-176.026 EndZ=0
    g9: LineSegment [constr] StartX=752.5 StartY=-176.026 StartZ=0 EndX=762.5 EndY=-176.026 EndZ=0
    g10: LineSegment [constr] StartX=762.5 StartY=-176.026 StartZ=0 EndX=762.5 EndY=-166.026 EndZ=0
    g11: LineSegment [constr] StartX=762.5 StartY=-166.026 StartZ=0 EndX=752.5 EndY=-166.026 EndZ=0
    g12: LineSegment [constr] StartX=752.5 StartY=-166.026 StartZ=0 EndX=752.5 EndY=-176.026 EndZ=0
    g13: LineSegment [constr] StartX=752.5 StartY=-166.026 StartZ=0 EndX=868 EndY=-166.026 EndZ=0
    g14: LineSegment [constr] StartX=752.5 StartY=-166.026 StartZ=0 EndX=637 EndY=-166.026 EndZ=0
    g15: LineSegment [constr] StartX=810.25 StartY=-166.026 StartZ=0 EndX=810.25 EndY=-176.026 EndZ=0
    g16: LineSegment [constr] StartX=810.25 StartY=-176.026 StartZ=0 EndX=820.25 EndY=-176.026 EndZ=0
    g17: LineSegment [constr] StartX=820.25 StartY=-176.026 StartZ=0 EndX=820.25 EndY=-166.026 EndZ=0
    g18: LineSegment [constr] StartX=820.25 StartY=-166.026 StartZ=0 EndX=810.25 EndY=-166.026 EndZ=0
    g19: LineSegment [constr] StartX=694.75 StartY=-166.026 StartZ=0 EndX=694.75 EndY=-176.026 EndZ=0
    g20: LineSegment [constr] StartX=694.75 StartY=-176.026 StartZ=0 EndX=704.75 EndY=-176.026 EndZ=0
    g21: LineSegment [constr] StartX=704.75 StartY=-176.026 StartZ=0 EndX=704.75 EndY=-166.026 EndZ=0
    g22: LineSegment [constr] StartX=704.75 StartY=-166.026 StartZ=0 EndX=694.75 EndY=-166.026 EndZ=0
    g23: Circle CenterX=868 CenterY=-166.026 CenterZ=0 NormalX=0 NormalY=0 NormalZ=1 AngleXU=0 Radius=1.5
    g24: Circle CenterX=810.25 CenterY=-166.026 CenterZ=0 NormalX=0 NormalY=0 NormalZ=1 AngleXU=0 Radius=1.5
    g25: Circle CenterX=752.5 CenterY=-166.026 CenterZ=0 NormalX=0 NormalY=0 NormalZ=1 AngleXU=0 Radius=1.5
    g26: Circle CenterX=694.75 CenterY=-166.026 CenterZ=0 NormalX=0 NormalY=0 NormalZ=1 AngleXU=0 Radius=1.5
    g27: Circle CenterX=637 CenterY=-166.026 CenterZ=0 NormalX=0 NormalY=0 NormalZ=1 AngleXU=0 Radius=1.5
  constraints (62):
    c: Coincident(g0,g1)
    c: Coincident(g1,g2)
    c: Coincident(g2,g3)
    c: Coincident(g3,g0)
    c: Horizontal(g0)
    c: Horizontal(g2)
    c: Vertical(g1)
    c: Vertical(g3)
    c: Distance(g1,g3) = 10
    c: Distance(g0,g2) = 10
    c: Coincident(g0,g-3)
    c: Coincident(g4,g5)
    c: Coincident(g5,g6)
    c: Coincident(g6,g7)
    c: Coincident(g7,g4)
    c: Vertical(g4)
    c: Vertical(g6)
    c: Horizontal(g5)
    c: Horizontal(g7)
    c: Distance(g4,g6) = 10
    c: Distance(g5,g7) = 10
    c: Coincident(g4,g-4)
    c: Coincident(g8,g6)
    c: Coincident(g8,g0)
    c: Coincident(g9,g10)
    c: Coincident(g10,g11)
    c: Coincident(g11,g12)
    c: Coincident(g12,g9)
    c: Horizontal(g9)
    c: Horizontal(g11)
    c: Vertical(g10)
    c: Vertical(g12)
    c: Distance(g10,g12) = 10
    c: Distance(g9,g11) = 10
    c: Symmetric(g8,g8,g9)
    c: Coincident(g13,g11)
    c: Coincident(g13,g5)
    c: Coincident(g14,g11)
    c: Coincident(g14,g1)
    c: Coincident(g15,g16)
    c: Coincident(g16,g17)
    c: Coincident(g17,g18)
    c: Coincident(g18,g15)
    c: Vertical(g15)
    c: Vertical(g17)
    c: Horizontal(g16)
    c: Horizontal(g18)
    c: Distance(g15,g17) = 10
    c: Symmetric(g13,g13,g15)
    c: PointOnObject(g16,g8)
    c: Coincident(g19,g20)
    c: Coincident(g20,g21)
    c: Coincident(g21,g22)
    c: Coincident(g22,g19)
    c: Vertical(g19)
    c: Vertical(g21)
    c: Horizontal(g20)
    c: Horizontal(g22)
    c: Distance(g19,g21) = 10
    c: Symmetric(g14,g14,g19)
    c: PointOnObject(g20,g8)
    c: Coincident(g23,g5)
FEATURE [PartDesign::Pocket] Pocket043
  BaseFeature = -> Pad012
  Direction = (0,0.866026,-0.5)
  Length = 5
  Length2 = 5
  Profile = -> Sketch067
  ReferenceAxis = -> Sketch067 [N_Axis]
  Refine = true
  Suppressed = false
  Type = 0
FEATURE [Sketcher::SketchObject] Sketch068
  ArcFitTolerance = 1e-06
  AttachmentSupport = -> [Pocket043]
  ExternalGeometry = -> [Pocket043]
  FullyConstrained = false
  MakeInternals = false
  MapMode = 5
  Placement = pos=(0,-0.1,0) rot=(1,0,0;1.5708rad)
  sketch-geometry (28):
    g0: LineSegment [constr] StartX=627 StartY=-225.17 StartZ=0 EndX=637 EndY=-225.17 EndZ=0
    g1: LineSegment [constr] StartX=637 StartY=-225.17 StartZ=0 EndX=637 EndY=-215.17 EndZ=0
    g2: LineSegment [constr] StartX=637 StartY=-215.17 StartZ=0 EndX=627 EndY=-215.17 EndZ=0
    g3: LineSegment [constr] StartX=627 StartY=-215.17 StartZ=0 EndX=627 EndY=-225.17 EndZ=0
    g4: LineSegment [constr] StartX=878 StartY=-225.17 StartZ=0 EndX=878 EndY=-215.17 EndZ=0
    g5: LineSegment [constr] StartX=878 StartY=-215.17 StartZ=0 EndX=868 EndY=-215.17 EndZ=0
    g6: LineSegment [constr] StartX=868 StartY=-215.17 StartZ=0 EndX=868 EndY=-225.17 EndZ=0
    g7: LineSegment [constr] StartX=868 StartY=-225.17 StartZ=0 EndX=878 EndY=-225.17 EndZ=0
    g8: LineSegment [constr] StartX=637 StartY=-225.17 StartZ=0 EndX=868 EndY=-225.17 EndZ=0
    g9: LineSegment [constr] StartX=752.5 StartY=-225.17 StartZ=0 EndX=762.5 EndY=-225.17 EndZ=0
    g10: LineSegment [constr] StartX=762.5 StartY=-225.17 StartZ=0 EndX=762.5 EndY=-215.17 EndZ=0
    g11: LineSegment [constr] StartX=762.5 StartY=-215.17 StartZ=0 EndX=752.5 EndY=-215.17 EndZ=0
    g12: LineSegment [constr] StartX=752.5 StartY=-215.17 StartZ=0 EndX=752.5 EndY=-225.17 EndZ=0
    g13: LineSegment [constr] StartX=752.5 StartY=-215.17 StartZ=0 EndX=868 EndY=-215.17 EndZ=0
    g14: LineSegment [constr] StartX=752.5 StartY=-215.17 StartZ=0 EndX=637 EndY=-215.17 EndZ=0
    g15: LineSegment [constr] StartX=810.25 StartY=-215.17 StartZ=0 EndX=800.25 EndY=-215.17 EndZ=0
    g16: LineSegment [constr] StartX=800.25 StartY=-215.17 StartZ=0 EndX=800.25 EndY=-225.17 EndZ=0
    g17: LineSegment [constr] StartX=800.25 StartY=-225.17 StartZ=0 EndX=810.25 EndY=-225.17 EndZ=0
    g18: LineSegment [constr] StartX=810.25 StartY=-225.17 StartZ=0 EndX=810.25 EndY=-215.17 EndZ=0
    g19: LineSegment [constr] StartX=694.75 StartY=-215.17 StartZ=0 EndX=684.75 EndY=-215.17 EndZ=0
    g20: LineSegment [constr] StartX=684.75 StartY=-215.17 StartZ=0 EndX=684.75 EndY=-225.17 EndZ=0
    g21: LineSegment [constr] StartX=684.75 StartY=-225.17 StartZ=0 EndX=694.75 EndY=-225.17 EndZ=0
    g22: LineSegment [constr] StartX=694.75 StartY=-225.17 StartZ=0 EndX=694.75 EndY=-215.17 EndZ=0
    g23: Circle CenterX=868 CenterY=-215.17 CenterZ=0 NormalX=0 NormalY=0 NormalZ=1 AngleXU=0 Radius=1.5
    g24: Circle CenterX=810.25 CenterY=-215.17 CenterZ=0 NormalX=0 NormalY=0 NormalZ=1 AngleXU=0 Radius=1.5
    g25: Circle CenterX=752.5 CenterY=-215.17 CenterZ=0 NormalX=0 NormalY=0 NormalZ=1 AngleXU=0 Radius=1.5
    g26: Circle CenterX=694.75 CenterY=-215.17 CenterZ=0 NormalX=0 NormalY=0 NormalZ=1 AngleXU=0 Radius=1.5
    g27: Circle CenterX=637 CenterY=-215.17 CenterZ=0 NormalX=0 NormalY=0 NormalZ=1 AngleXU=0 Radius=1.5
  constraints (60):
    c: Coincident(g0,g1)
    c: Coincident(g1,g2)
    c: Coincident(g2,g3)
    c: Coincident(g3,g0)
    c: Horizontal(g0)
    c: Horizontal(g2)
    c: Vertical(g1)
    c: Vertical(g3)
    c: Distance(g1,g3) = 10
    c: Distance(g0,g2) = 10
    c: Coincident(g0,g-3)
    c: Coincident(g4,g5)
    c: Coincident(g5,g6)
    c: Coincident(g6,g7)
    c: Coincident(g7,g4)
    c: Vertical(g4)
    c: Vertical(g6)
    c: Horizontal(g5)
    c: Horizontal(g7)
    c: Distance(g4,g6) = 10
    c: Distance(g5,g7) = 10
    c: Coincident(g4,g-4)
    c: Coincident(g8,g0)
    c: Coincident(g8,g6)
    c: Coincident(g9,g10)
    c: Coincident(g10,g11)
    c: Coincident(g11,g12)
    c: Coincident(g12,g9)
    c: Horizontal(g9)
    c: Horizontal(g11)
    c: Vertical(g10)
    c: Vertical(g12)
    c: Distance(g10,g12) = 10
    c: Distance(g9,g11) = 10
    c: Symmetric(g8,g8,g9)
    c: Coincident(g13,g11)
    c: Coincident(g13,g5)
    c: Coincident(g14,g11)
    c: Coincident(g14,g1)
    c: Coincident(g15,g16)
    c: Coincident(g16,g17)
    c: Coincident(g17,g18)
    c: Coincident(g18,g15)
    c: Horizontal(g15)
    c: Horizontal(g17)
    c: Vertical(g16)
    c: Vertical(g18)
    c: Distance(g16,g18) = 10
    c: Symmetric(g13,g13,g15)
    c: PointOnObject(g16,g8)
    c: Coincident(g19,g20)
    c: Coincident(g20,g21)
    c: Coincident(g21,g22)
    c: Coincident(g22,g19)
    c: Horizontal(g19)
    c: Horizontal(g21)
    c: Vertical(g20)
    c: Vertical(g22)
    c: Distance(g20,g22) = 10
    c: Symmetric(g14,g14,g19)
FEATURE [PartDesign::Pocket] Pocket044
  BaseFeature = -> Pocket043
  Direction = (0,1,-2e-16)
  Length = 5
  Length2 = 5
  Profile = -> Sketch068
  ReferenceAxis = -> Sketch068 [N_Axis]
  Refine = true
  Suppressed = false
  Type = 0
FEATURE [Sketcher::SketchObject] Sketch069
  ArcFitTolerance = 1e-06
  AttachmentSupport = -> [Pocket044]
  ExternalGeometry = -> [Pocket044]
  FullyConstrained = false
  MakeInternals = false
  MapMode = 5
  Placement = pos=(627,0,0) rot=(0.57735,-0.57735,-0.57735;2.0944rad)
  sketch-geometry (28):
    g0: LineSegment [constr] StartX=-1.91705 StartY=-203.17 StartZ=0 EndX=-11.917 EndY=-203.17 EndZ=0
    g1: LineSegment [constr] StartX=-11.917 StartY=-203.17 StartZ=0 EndX=-11.917 EndY=-213.17 EndZ=0
    g2: LineSegment [constr] StartX=-11.917 StartY=-213.17 StartZ=0 EndX=-1.91705 EndY=-213.17 EndZ=0
    g3: LineSegment [constr] StartX=-1.91705 StartY=-213.17 StartZ=0 EndX=-1.91705 EndY=-203.17 EndZ=0
    g4: LineSegment [constr] StartX=-349.9 StartY=-203.17 StartZ=0 EndX=-349.9 EndY=-213.17 EndZ=0
    g5: LineSegment [constr] StartX=-349.9 StartY=-213.17 StartZ=0 EndX=-339.9 EndY=-213.17 EndZ=0
    g6: LineSegment [constr] StartX=-339.9 StartY=-213.17 StartZ=0 EndX=-339.9 EndY=-203.17 EndZ=0
    g7: LineSegment [constr] StartX=-339.9 StartY=-203.17 StartZ=0 EndX=-349.9 EndY=-203.17 EndZ=0
    g8: LineSegment [constr] StartX=-339.9 StartY=-203.17 StartZ=0 EndX=-11.917 EndY=-203.17 EndZ=0
    g9: LineSegment [constr] StartX=-175.909 StartY=-203.17 StartZ=0 EndX=-175.909 EndY=-213.17 EndZ=0
    g10: LineSegment [constr] StartX=-175.909 StartY=-213.17 StartZ=0 EndX=-165.909 EndY=-213.17 EndZ=0
    g11: LineSegment [constr] StartX=-165.909 StartY=-213.17 StartZ=0 EndX=-165.909 EndY=-203.17 EndZ=0
    g12: LineSegment [constr] StartX=-165.909 StartY=-203.17 StartZ=0 EndX=-175.909 EndY=-203.17 EndZ=0
    g13: LineSegment [constr] StartX=-175.909 StartY=-213.17 StartZ=0 EndX=-339.9 EndY=-213.17 EndZ=0
    g14: LineSegment [constr] StartX=-175.909 StartY=-213.17 StartZ=0 EndX=-11.917 EndY=-213.17 EndZ=0
    g15: LineSegment [constr] StartX=-93.9128 StartY=-213.17 StartZ=0 EndX=-83.9128 EndY=-213.17 EndZ=0
    g16: LineSegment [constr] StartX=-83.9128 StartY=-213.17 StartZ=0 EndX=-83.9128 EndY=-203.17 EndZ=0
    g17: LineSegment [constr] StartX=-83.9128 StartY=-203.17 StartZ=0 EndX=-93.9128 EndY=-203.17 EndZ=0
    g18: LineSegment [constr] StartX=-93.9128 StartY=-203.17 StartZ=0 EndX=-93.9128 EndY=-213.17 EndZ=0
    g19: LineSegment [constr] StartX=-257.904 StartY=-213.17 StartZ=0 EndX=-247.904 EndY=-213.17 EndZ=0
    g20: LineSegment [constr] StartX=-247.904 StartY=-213.17 StartZ=0 EndX=-247.904 EndY=-203.17 EndZ=0
    g21: LineSegment [constr] StartX=-247.904 StartY=-203.17 StartZ=0 EndX=-257.904 EndY=-203.17 EndZ=0
    g22: LineSegment [constr] StartX=-257.904 StartY=-203.17 StartZ=0 EndX=-257.904 EndY=-213.17 EndZ=0
    g23: Circle CenterX=-11.917 CenterY=-213.17 CenterZ=0 NormalX=0 NormalY=0 NormalZ=1 AngleXU=0 Radius=1.5
    g24: Circle CenterX=-93.9128 CenterY=-213.17 CenterZ=0 NormalX=0 NormalY=0 NormalZ=1 AngleXU=0 Radius=1.5
    g25: Circle CenterX=-175.909 CenterY=-213.17 CenterZ=0 NormalX=0 NormalY=0 NormalZ=1 AngleXU=0 Radius=1.5
    g26: Circle CenterX=-257.904 CenterY=-213.17 CenterZ=0 NormalX=0 NormalY=0 NormalZ=1 AngleXU=0 Radius=1.5
    g27: Circle CenterX=-339.9 CenterY=-213.17 CenterZ=0 NormalX=0 NormalY=0 NormalZ=1 AngleXU=0 Radius=1.5
  constraints (61):
    c: Coincident(g0,g1)
    c: Coincident(g1,g2)
    c: Coincident(g2,g3)
    c: Coincident(g3,g0)
    c: Horizontal(g0)
    c: Horizontal(g2)
    c: Vertical(g1)
    c: Vertical(g3)
    c: Distance(g1,g3) = 10
    c: Distance(g0,g2) = 10
    c: Coincident(g0,g-3)
    c: Coincident(g4,g5)
    c: Coincident(g5,g6)
    c: Coincident(g6,g7)
    c: Coincident(g7,g4)
    c: Vertical(g4)
    c: Vertical(g6)
    c: Horizontal(g5)
    c: Horizontal(g7)
    c: Distance(g4,g6) = 10
    c: Distance(g5,g7) = 10
    c: Coincident(g4,g-4)
    c: Coincident(g8,g6)
    c: Coincident(g8,g0)
    c: Coincident(g9,g10)
    c: Coincident(g10,g11)
    c: Coincident(g11,g12)
    c: Coincident(g12,g9)
    c: Vertical(g9)
    c: Vertical(g11)
    c: Horizontal(g10)
    c: Horizontal(g12)
    c: Distance(g9,g11) = 10
    c: Distance(g10,g12) = 10
    c: Symmetric(g8,g8,g9)
    c: Coincident(g13,g9)
    c: Coincident(g13,g5)
    c: Coincident(g14,g9)
    c: Coincident(g14,g1)
    c: Coincident(g15,g16)
    c: Coincident(g16,g17)
    c: Coincident(g17,g18)
    c: Coincident(g18,g15)
    c: Horizontal(g15)
    c: Horizontal(g17)
    c: Vertical(g16)
    c: Vertical(g18)
    c: Distance(g16,g18) = 10
    c: Symmetric(g14,g14,g15)
    c: PointOnObject(g16,g8)
    c: Coincident(g19,g20)
    c: Coincident(g20,g21)
    c: Coincident(g21,g22)
    c: Coincident(g22,g19)
    c: Horizontal(g19)
    c: Horizontal(g21)
    c: Vertical(g20)
    c: Vertical(g22)
    c: Distance(g20,g22) = 10
    c: Symmetric(g13,g13,g19)
    c: PointOnObject(g20,g8)
FEATURE [PartDesign::Pocket] Pocket045
  BaseFeature = -> Pocket044
  Direction = (1,0,0)
  Length = 5
  Length2 = 5
  Profile = -> Sketch069
  ReferenceAxis = -> Sketch069 [N_Axis]
  Refine = true
  Suppressed = false
  Type = 1
FEATURE [PartDesign::Body] Body008  label="SpHr1"
  AllowCompound = false
  Group = -> [Binder010,Sketch036,Pad011,Sketch037,Pocket021,Sketch038,Pocket022,Sketch039,Pad012,Sketch067,Pocket043,Sketch068,Pocket044,Sketch069,Pocket045]
  Origin = -> Origin009
  Tip = -> Pocket045
FEATURE [PartDesign::SubShapeBinder] Binder020
  BindCopyOnChange = 0
  BindMode = 0
  ClaimChildren = false
  Context = -> Part [Body004.Binder020.]
  Fuse = false
  MakeFace = true
  OffsetFill = false
  OffsetIntersection = false
  OffsetJoinType = 0
  OffsetOpenResult = false
  PartialLoad = false
  Refine = true
  Relative = true
  Support = -> [Body008[Pocket045.Face2]]
  _Version = 2
FEATURE [Sketcher::SketchObject] Sketch070
  ArcFitTolerance = 1e-06
  AttachmentSupport = -> [Binder020]
  ExternalGeometry = -> [Binder020]
  FullyConstrained = true
  MakeInternals = false
  MapMode = 5
  Placement = pos=(1156,0,0) rot=(0.57735,-0.57735,-0.57735;2.0944rad)
  sketch-geometry (5):
    g0: Circle CenterX=-7.91705 CenterY=-213.17 CenterZ=0 NormalX=0 NormalY=0 NormalZ=1 AngleXU=0 Radius=1.5
    g1: Circle CenterX=-89.9128 CenterY=-213.17 CenterZ=0 NormalX=0 NormalY=0 NormalZ=1 AngleXU=0 Radius=1.5
    g2: Circle CenterX=-171.909 CenterY=-213.17 CenterZ=0 NormalX=0 NormalY=0 NormalZ=1 AngleXU=0 Radius=1.5
    g3: Circle CenterX=-253.904 CenterY=-213.17 CenterZ=0 NormalX=0 NormalY=0 NormalZ=1 AngleXU=0 Radius=1.5
    g4: Circle CenterX=-335.9 CenterY=-213.17 CenterZ=0 NormalX=0 NormalY=0 NormalZ=1 AngleXU=0 Radius=1.5
  constraints (10):
    c: Coincident(g0,g-7)
    c: Equal(g0,g-7)
    c: Coincident(g1,g-6)
    c: Equal(g1,g-6)
    c: Coincident(g2,g-5)
    c: Equal(g2,g-5)
    c: Coincident(g3,g-4)
    c: Equal(g3,g-4)
    c: Coincident(g4,g-3)
    c: Equal(g4,g-3)
FEATURE [PartDesign::Pocket] Pocket046
  BaseFeature = -> Pocket013
  Direction = (1,0,0)
  Length = 5
  Length2 = 5
  Profile = -> Sketch070
  ReferenceAxis = -> Sketch070 [N_Axis]
  Refine = true
  Suppressed = false
  Type = 0
FEATURE [PartDesign::Body] Body004  label="SpVr1"
  AllowCompound = false
  Group = -> [Binder004,Sketch020,Pad007,Sketch021,Pocket009,Sketch022,Pad008,Sketch023,Pocket010,Sketch024,Pocket011,Sketch025,Pocket012,Sketch026,Pocket013,Binder020,Sketch070,Pocket046]
  Origin = -> Origin005
  Placement = pos=(-280,4,0) rot=(0,0,1;0rad)
  Tip = -> Pocket046
FEATURE [PartDesign::SubShapeBinder] Binder021
  BindCopyOnChange = 0
  BindMode = 0
  ClaimChildren = false
  Context = -> Part [Body007.Binder021.]
  Fuse = false
  MakeFace = true
  OffsetFill = false
  OffsetIntersection = false
  OffsetJoinType = 0
  OffsetOpenResult = false
  PartialLoad = false
  Refine = true
  Relative = true
  Support = -> [Body008[Pocket045.Face4]]
  _Version = 2
FEATURE [Sketcher::SketchObject] Sketch071
  ArcFitTolerance = 1e-06
  AttachmentSupport = -> [Binder021]
  ExternalGeometry = -> [Binder021]
  FullyConstrained = true
  MakeInternals = false
  MapMode = 5
  Placement = pos=(629,0,0) rot=(0.57735,0.57735,0.57735;2.0944rad)
  sketch-geometry (5):
    g0: Circle CenterX=339.9 CenterY=-213.17 CenterZ=0 NormalX=0 NormalY=0 NormalZ=1 AngleXU=0 Radius=1.5
    g1: Circle CenterX=257.904 CenterY=-213.17 CenterZ=0 NormalX=0 NormalY=0 NormalZ=1 AngleXU=0 Radius=1.5
    g2: Circle CenterX=175.909 CenterY=-213.17 CenterZ=0 NormalX=0 NormalY=0 NormalZ=1 AngleXU=0 Radius=1.5
    g3: Circle CenterX=93.9128 CenterY=-213.17 CenterZ=0 NormalX=0 NormalY=0 NormalZ=1 AngleXU=0 Radius=1.5
    g4: Circle CenterX=11.917 CenterY=-213.17 CenterZ=0 NormalX=0 NormalY=0 NormalZ=1 AngleXU=0 Radius=1.5
  constraints (10):
    c: Coincident(g0,g-7)
    c: Equal(g0,g-7)
    c: Coincident(g1,g-6)
    c: Equal(g1,g-6)
    c: Coincident(g2,g-5)
    c: Equal(g2,g-5)
    c: Coincident(g3,g-4)
    c: Equal(g3,g-4)
    c: Coincident(g4,g-3)
    c: Equal(g4,g-3)
FEATURE [PartDesign::Pocket] Pocket047
  BaseFeature = -> Pocket020
  Direction = (-1,0,0)
  Length = 5
  Length2 = 5
  Profile = -> Sketch071
  ReferenceAxis = -> Sketch071 [N_Axis]
  Refine = true
  Suppressed = false
  Type = 0
FEATURE [PartDesign::Body] Body007  label="SpVr2"
  AllowCompound = false
  Group = -> [Binder006,Sketch028,Pad009,Sketch029,Pocket015,Sketch030,Pad010,Sketch031,Pocket016,Sketch032,Pocket017,Sketch033,Pocket018,Sketch035,Pocket020,Binder021,Sketch071,Pocket047]
  Origin = -> Origin008
  Tip = -> Pocket047
FEATURE [PartDesign::SubShapeBinder] Binder022
  BindCopyOnChange = 0
  BindMode = 0
  ClaimChildren = false
  Context = -> Part [Body003.Binder022.]
  Fuse = false
  MakeFace = true
  OffsetFill = false
  OffsetIntersection = false
  OffsetJoinType = 0
  OffsetOpenResult = false
  PartialLoad = false
  Refine = true
  Relative = true
  Support = -> [Body008[Pocket045.Face34]]
  _Version = 2
FEATURE [Sketcher::SketchObject] Sketch072
  ArcFitTolerance = 1e-06
  AttachmentSupport = -> [Binder022]
  ExternalGeometry = -> [Binder022]
  FullyConstrained = true
  MakeInternals = false
  MapMode = 5
  Placement = pos=(0,87.9015,-50.7499) rot=(1,0,0;1.0472rad)
  sketch-geometry (5):
    g0: Circle CenterX=868 CenterY=-166 CenterZ=0 NormalX=0 NormalY=0 NormalZ=1 AngleXU=0 Radius=1.5
    g1: Circle CenterX=810.25 CenterY=-166 CenterZ=0 NormalX=0 NormalY=0 NormalZ=1 AngleXU=0 Radius=1.5
    g2: Circle CenterX=752.5 CenterY=-166 CenterZ=0 NormalX=0 NormalY=0 NormalZ=1 AngleXU=0 Radius=1.5
    g3: Circle CenterX=694.75 CenterY=-166 CenterZ=0 NormalX=0 NormalY=0 NormalZ=1 AngleXU=0 Radius=1.5
    g4: Circle CenterX=637 CenterY=-166 CenterZ=0 NormalX=0 NormalY=0 NormalZ=1 AngleXU=0 Radius=1.5
  constraints (10):
    c: Coincident(g0,g-7)
    c: Equal(g0,g-7)
    c: Coincident(g1,g-6)
    c: Equal(g1,g-6)
    c: Coincident(g2,g-5)
    c: Equal(g2,g-5)
    c: Coincident(g3,g-4)
    c: Equal(g3,g-4)
    c: Coincident(g4,g-3)
    c: Equal(g4,g-3)
FEATURE [PartDesign::Pocket] Pocket048
  BaseFeature = -> Pocket019
  Direction = (0,0.866026,-0.5)
  Length = 5
  Length2 = 5
  Profile = -> Sketch072
  ReferenceAxis = -> Sketch072 [N_Axis]
  Refine = true
  Reversed = true
  Suppressed = false
  Type = 0
FEATURE [PartDesign::Body] Body003  label="MainPt2"
  AllowCompound = false
  Group = -> [Binder,Sketch012,Pad004,Binder005,Sketch027,Pocket014,Binder007,Sketch034,Pocket019,Binder022,Sketch072,Pocket048]
  Origin = -> Origin004
  Placement = pos=(0,-0.00157848,-0.0295289) rot=(0,0,1;0rad)
  Tip = -> Pocket048
FEATURE [PartDesign::SubShapeBinder] Binder023
  BindCopyOnChange = 0
  BindMode = 0
  ClaimChildren = false
  Context = -> Part [Body001.Binder023.]
  Fuse = false
  MakeFace = true
  OffsetFill = false
  OffsetIntersection = false
  OffsetJoinType = 0
  OffsetOpenResult = false
  PartialLoad = false
  Refine = true
  Relative = true
  Support = -> [Body008[Pocket045.Face5]]
  _Version = 2
FEATURE [Sketcher::SketchObject] Sketch073
  ArcFitTolerance = 1e-06
  AttachmentSupport = -> [Binder023]
  ExternalGeometry = -> [Binder023]
  FullyConstrained = true
  MakeInternals = false
  MapMode = 5
  Placement = pos=(0,4,0) rot=(0,0.707107,0.707107;3.14159rad)
  sketch-geometry (5):
    g0: Circle CenterX=-32 CenterY=128.03 CenterZ=0 NormalX=0 NormalY=0 NormalZ=1 AngleXU=0 Radius=1.5
    g1: Circle CenterX=-89.75 CenterY=128.03 CenterZ=0 NormalX=0 NormalY=0 NormalZ=1 AngleXU=0 Radius=1.5
    g2: Circle CenterX=-147.5 CenterY=128.03 CenterZ=0 NormalX=0 NormalY=0 NormalZ=1 AngleXU=0 Radius=1.5
    g3: Circle CenterX=-205.25 CenterY=128.03 CenterZ=0 NormalX=0 NormalY=0 NormalZ=1 AngleXU=0 Radius=1.5
    g4: Circle CenterX=-263 CenterY=128.03 CenterZ=0 NormalX=0 NormalY=0 NormalZ=1 AngleXU=0 Radius=1.5
  constraints (10):
    c: Coincident(g0,g-7)
    c: Equal(g0,g-7)
    c: Coincident(g1,g-6)
    c: Equal(g1,g-6)
    c: Coincident(g2,g-5)
    c: Equal(g2,g-5)
    c: Coincident(g3,g-4)
    c: Equal(g3,g-4)
    c: Coincident(g4,g-3)
    c: Equal(g4,g-3)
FEATURE [PartDesign::Pocket] Pocket049
  BaseFeature = -> Pocket008
  Direction = (0,-1,2e-16)
  Length = 5
  Length2 = 5
  Placement = pos=(0,0,0) rot=(1,1,1;2.0944rad)
  Profile = -> Sketch073
  ReferenceAxis = -> Sketch073 [N_Axis]
  Refine = true
  Suppressed = false
  Type = 0
FEATURE [PartDesign::Body] Body001  label="PzDelantera"
  AllowCompound = false
  Group = -> [Sketch005,Pad002,Sketch019,Pocket008,Binder023,Sketch073,Pocket049]
  Origin = -> Origin002
  Placement = pos=(605,-2.1,-343.2) rot=(0,0,1;0rad)
  Tip = -> Pocket049
FEATURE [App::DocumentObjectGroup] Group  label="RIGHT"
  Group = -> [Body006,Body003,Body001,Body004,Body007,Body008]
FEATURE [App::DocumentObjectGroup] Group002  label="CENTER"
FEATURE [App::Part] Part  label="Recubrimiento"
  Group = -> [Body001,Body006,Body003,Body004,Group,Body002,Body,Body005,Group001,Body007,Body008,Body009,Body010,Body011,Group002]
  Origin = -> Origin
FEATURE [PartDesign::SubShapeBinder] Binder024
  BindCopyOnChange = 0
  BindMode = 0
  ClaimChildren = false
  Context = -> Part001 [Body012.Binder024.]
  Fuse = false
  MakeFace = true
  OffsetFill = false
  OffsetIntersection = false
  OffsetJoinType = 0
  OffsetOpenResult = false
  PartialLoad = false
  Refine = true
  Relative = true
  Support = -> [Part[Body.Pocket040.Face1,Body001.Pocket049.Face1]]
  _Version = 2
FEATURE [Sketcher::SketchObject] Sketch074
  ArcFitTolerance = 1e-06
  AttachmentSupport = -> [Binder024]
  ExternalGeometry = -> [Binder024]
  FullyConstrained = true
  MakeInternals = false
  MapMode = 5
  Placement = pos=(-5e-16,-2.1,0) rot=(1,0,0;1.5708rad)
  sketch-geometry (8):
    g0: LineSegment StartX=-300 StartY=-343.2 StartZ=0 EndX=900 EndY=-343.2 EndZ=0
    g1: LineSegment StartX=860 StartY=-383.2 StartZ=0 EndX=-260 EndY=-383.2 EndZ=0
    g2: LineSegment StartX=900 StartY=-343.2 StartZ=0 EndX=900 EndY=-943.2 EndZ=0
    g3: LineSegment StartX=900 StartY=-943.2 StartZ=0 EndX=860 EndY=-943.2 EndZ=0
    g4: LineSegment StartX=860 StartY=-943.2 StartZ=0 EndX=860 EndY=-383.2 EndZ=0
    g5: LineSegment StartX=-300 StartY=-343.2 StartZ=0 EndX=-300 EndY=-943.2 EndZ=0
    g6: LineSegment StartX=-300 StartY=-943.2 StartZ=0 EndX=-260 EndY=-943.2 EndZ=0
    g7: LineSegment StartX=-260 StartY=-943.2 StartZ=0 EndX=-260 EndY=-383.2 EndZ=0
  constraints (23):
    c: Coincident(g0,g-4)
    c: Coincident(g0,g-3)
    c: Horizontal(g1)
    c: Vertical(g2)
    c: Distance(g3) = 40
    c: Coincident(g3,g2)
    c: Horizontal(g3)
    c: Coincident(g4,g3)
    c: Vertical(g4)
    c: Vertical(g5)
    c: Distance(g6) = 40
    c: Coincident(g6,g5)
    c: Coincident(g7,g6)
    c: Vertical(g7)
    c: Coincident(g1,g7)
    c: Coincident(g1,g4)
    c: Coincident(g5,g0)
    c: Coincident(g2,g0)
    c: DistanceY(g2,g2) = 600
    c: DistanceY(g1,g0) = 40
    c: DistanceY(g4,g4) = 560
    c: Horizontal(g6)
    c: Equal(g5,g2)
FEATURE [PartDesign::Pad] Pad019
  Direction = (0,-1,2e-16)
  Length = 40
  Length2 = 10
  Profile = -> Sketch074
  ReferenceAxis = -> Sketch074 [N_Axis]
  Refine = true
  Reversed = true
  Suppressed = false
  Type = 0
FEATURE [Sketcher::SketchObject] Sketch075
  ArcFitTolerance = 1e-06
  AttachmentSupport = -> [Pad019]
  ExternalGeometry = -> [Pad019]
  FullyConstrained = true
  MakeInternals = false
  MapMode = 5
  Placement = pos=(900,0,0) rot=(0.57735,0.57735,0.57735;2.0944rad)
  sketch-geometry (8):
    g0: LineSegment StartX=37.9 StartY=-343.2 StartZ=0 EndX=357.9 EndY=-343.2 EndZ=0
    g1: LineSegment StartX=357.9 StartY=-343.2 StartZ=0 EndX=357.9 EndY=-383.2 EndZ=0
    g2: LineSegment StartX=357.9 StartY=-383.2 StartZ=0 EndX=37.9 EndY=-383.2 EndZ=0
    g3: LineSegment StartX=37.9 StartY=-343.2 StartZ=0 EndX=37.9 EndY=-383.2 EndZ=0
    g4: LineSegment StartX=37.9 StartY=-943.2 StartZ=0 EndX=357.9 EndY=-943.2 EndZ=0
    g5: LineSegment StartX=357.9 StartY=-943.2 StartZ=0 EndX=357.9 EndY=-903.2 EndZ=0
    g6: LineSegment StartX=357.9 StartY=-903.2 StartZ=0 EndX=37.9 EndY=-903.2 EndZ=0
    g7: LineSegment StartX=37.9 StartY=-903.2 StartZ=0 EndX=37.9 EndY=-943.2 EndZ=0
  constraints (22):
    c: Distance(g0) = 320
    c: Coincident(g0,g-3)
    c: Horizontal(g0)
    c: Distance(g1) = 40
    c: Coincident(g1,g0)
    c: Vertical(g1)
    c: Coincident(g2,g1)
    c: PointOnObject(g2,g-3)
    c: Horizontal(g2)
    c: Coincident(g3,g0)
    c: Coincident(g3,g2)
    c: Distance(g4) = 320
    c: Coincident(g4,g-3)
    c: Horizontal(g4)
    c: Distance(g5) = 40
    c: Coincident(g5,g4)
    c: Vertical(g5)
    c: Coincident(g6,g5)
    c: PointOnObject(g6,g-3)
    c: Horizontal(g6)
    c: Coincident(g7,g6)
    c: Coincident(g7,g4)
FEATURE [PartDesign::Pad] Pad020
  BaseFeature = -> Pad019
  Direction = (1,0,0)
  Length = 40
  Length2 = 10
  Profile = -> Sketch075
  ReferenceAxis = -> Sketch075 [N_Axis]
  Refine = true
  Reversed = true
  Suppressed = false
  Type = 0
FEATURE [Sketcher::SketchObject] Sketch076
  ArcFitTolerance = 1e-06
  AttachmentSupport = -> [Pad020]
  ExternalGeometry = -> [Pad020]
  FullyConstrained = false
  MakeInternals = false
  MapMode = 5
  Placement = pos=(-300,0,0) rot=(0.57735,-0.57735,-0.57735;2.0944rad)
  sketch-geometry (8):
    g0: LineSegment StartX=-37.9 StartY=-343.2 StartZ=0 EndX=-357.9 EndY=-343.2 EndZ=0
    g1: LineSegment StartX=-357.9 StartY=-343.2 StartZ=0 EndX=-357.9 EndY=-383.2 EndZ=0
    g2: LineSegment StartX=-357.9 StartY=-383.2 StartZ=0 EndX=-37.9 EndY=-383.2 EndZ=0
    g3: LineSegment StartX=-37.9 StartY=-383.2 StartZ=0 EndX=-37.9 EndY=-343.2 EndZ=0
    g4: LineSegment StartX=-37.9 StartY=-943.2 StartZ=0 EndX=-357.9 EndY=-943.2 EndZ=0
    g5: LineSegment StartX=-357.9 StartY=-943.2 StartZ=0 EndX=-357.9 EndY=-903.2 EndZ=0
    g6: LineSegment StartX=-357.9 StartY=-903.2 StartZ=0 EndX=-37.9 EndY=-903.2 EndZ=0
    g7: LineSegment StartX=-37.9 StartY=-903.2 StartZ=0 EndX=-37.9 EndY=-943.2 EndZ=0
  constraints (18):
    c: Coincident(g0,g-3)
    c: Coincident(g0,g-4)
    c: Coincident(g1,g0)
    c: Coincident(g1,g-4)
    c: Coincident(g2,g1)
    c: PointOnObject(g2,g-3)
    c: Horizontal(g2)
    c: Coincident(g3,g2)
    c: Coincident(g3,g0)
    c: Coincident(g4,g-3)
    c: Coincident(g4,g-5)
    c: Coincident(g5,g4)
    c: Coincident(g5,g-5)
    c: Coincident(g6,g5)
    c: Horizontal(g6)
    c: Coincident(g7,g4)
    c: Coincident(g7,g6)
    c: DistanceX(g2,g2) = 320
FEATURE [PartDesign::Pad] Pad021
  BaseFeature = -> Pad020
  Direction = (-1,0,0)
  Length = 40
  Length2 = 10
  Profile = -> Sketch076
  ReferenceAxis = -> Sketch076 [N_Axis]
  Refine = true
  Reversed = true
  Suppressed = false
  Type = 0
FEATURE [Sketcher::SketchObject] Sketch077
  ArcFitTolerance = 1e-06
  AttachmentSupport = -> [Pad021]
  ExternalGeometry = -> [Pad021]
  FullyConstrained = true
  MakeInternals = false
  MapMode = 5
  Placement = pos=(0,357.9,0) rot=(0,0.707107,0.707107;3.14159rad)
  sketch-geometry (8):
    g0: LineSegment StartX=-900 StartY=-943.2 StartZ=0 EndX=-900 EndY=-343.2 EndZ=0
    g1: LineSegment StartX=-900 StartY=-943.2 StartZ=0 EndX=-860 EndY=-943.2 EndZ=0
    g2: LineSegment StartX=-860 StartY=-943.2 StartZ=0 EndX=-860 EndY=-383.2 EndZ=0
    g3: LineSegment StartX=-860 StartY=-383.2 StartZ=0 EndX=260 EndY=-383.2 EndZ=0
    g4: LineSegment StartX=260 StartY=-383.2 StartZ=0 EndX=260 EndY=-943.2 EndZ=0
    g5: LineSegment StartX=260 StartY=-943.2 StartZ=0 EndX=300 EndY=-943.2 EndZ=0
    g6: LineSegment StartX=300 StartY=-943.2 StartZ=0 EndX=300 EndY=-343.2 EndZ=0
    g7: LineSegment StartX=300 StartY=-343.2 StartZ=0 EndX=-900 EndY=-343.2 EndZ=0
  constraints (16):
    c: Coincident(g0,g-3)
    c: Coincident(g0,g-6)
    c: Coincident(g1,g0)
    c: Coincident(g1,g-7)
    c: Coincident(g2,g1)
    c: Coincident(g2,g-9)
    c: Coincident(g3,g2)
    c: Coincident(g3,g-10)
    c: Coincident(g4,g3)
    c: Coincident(g4,g-11)
    c: Coincident(g5,g4)
    c: Coincident(g5,g-4)
    c: Coincident(g6,g5)
    c: Coincident(g6,g-5)
    c: Coincident(g7,g6)
    c: Coincident(g7,g0)
FEATURE [PartDesign::Pad] Pad022
  BaseFeature = -> Pad021
  Direction = (0,1,-2e-16)
  Length = 40
  Length2 = 10
  Profile = -> Sketch077
  ReferenceAxis = -> Sketch077 [N_Axis]
  Refine = true
  Reversed = true
  Suppressed = false
  Type = 0
FEATURE [Sketcher::SketchObject] Sketch078
  ArcFitTolerance = 1e-06
  AttachmentSupport = -> [Pad022]
  ExternalGeometry = -> [Pad022]
  FullyConstrained = true
  MakeInternals = false
  MapMode = 5
  Placement = pos=(0,-8.43e-14,-383.2) rot=(1,0,0;3.14159rad)
  sketch-geometry (6):
    g0: LineSegment [constr] StartX=300 StartY=-37.9 StartZ=0 EndX=300 EndY=-317.9 EndZ=0
    g1: LineSegment StartX=-260 StartY=-197.9 StartZ=0 EndX=860 EndY=-197.9 EndZ=0
    g2: LineSegment StartX=860 StartY=-197.9 StartZ=0 EndX=860 EndY=-157.9 EndZ=0
    g3: LineSegment StartX=860 StartY=-157.9 StartZ=0 EndX=-260 EndY=-157.9 EndZ=0
    g4: LineSegment StartX=-260 StartY=-157.9 StartZ=0 EndX=-260 EndY=-197.9 EndZ=0
    g5: GeomPoint [constr] X=300 Y=-177.9 Z=0
  constraints (14):
    c: Symmetric(g-5,g-5,g0)
    c: Symmetric(g-6,g-6,g0)
    c: Coincident(g1,g2)
    c: Coincident(g2,g3)
    c: Coincident(g3,g4)
    c: Coincident(g4,g1)
    c: Horizontal(g1)
    c: Horizontal(g3)
    c: Vertical(g2)
    c: Vertical(g4)
    c: Symmetric(g3,g1,g5)
    c: Symmetric(g0,g0,g5)
    c: PointOnObject(g2,g-4)
    c: DistanceY(g1,g2) = 40
FEATURE [PartDesign::Pad] Pad023
  BaseFeature = -> Pad022
  Direction = (0,0,-1)
  Length = 40
  Length2 = 10
  Profile = -> Sketch078
  ReferenceAxis = -> Sketch078 [N_Axis]
  Refine = true
  Reversed = true
  Suppressed = false
  Type = 0
FEATURE [PartDesign::Body] Body012  label="Cuerpo"
  AllowCompound = false
  Group = -> [Binder024,Sketch074,Pad019,Sketch075,Pad020,Sketch076,Pad021,Sketch077,Pad022,Sketch078,Pad023]
  Origin = -> Origin014
  Tip = -> Pad023
FEATURE [App::Part] Part001  label="Mesa"
  Group = -> [Body012]
  Origin = -> Origin013
FEATURE [Part::Part2DObjectPython] Line  # Draft 2D object (typed FeaturePython)
  Area = 0
  ChamferSize = 0
  Closed = false
  End = (900,-668.021,-943.2)
  FilletRadius = 0
  Length = 665.921
  MakeFace = true
  Placement = pos=(900,-2.1,-943.2) rot=(0,0,1;0rad)
  Points = (2) [(0,0,0),(0,-665.921,0)]
  Start = (900,-2.1,-943.2)
  Subdivisions = 0
FEATURE [App::Part] Part002  label="Estructura"
  Group = -> [Line]
  Origin = -> Origin015
